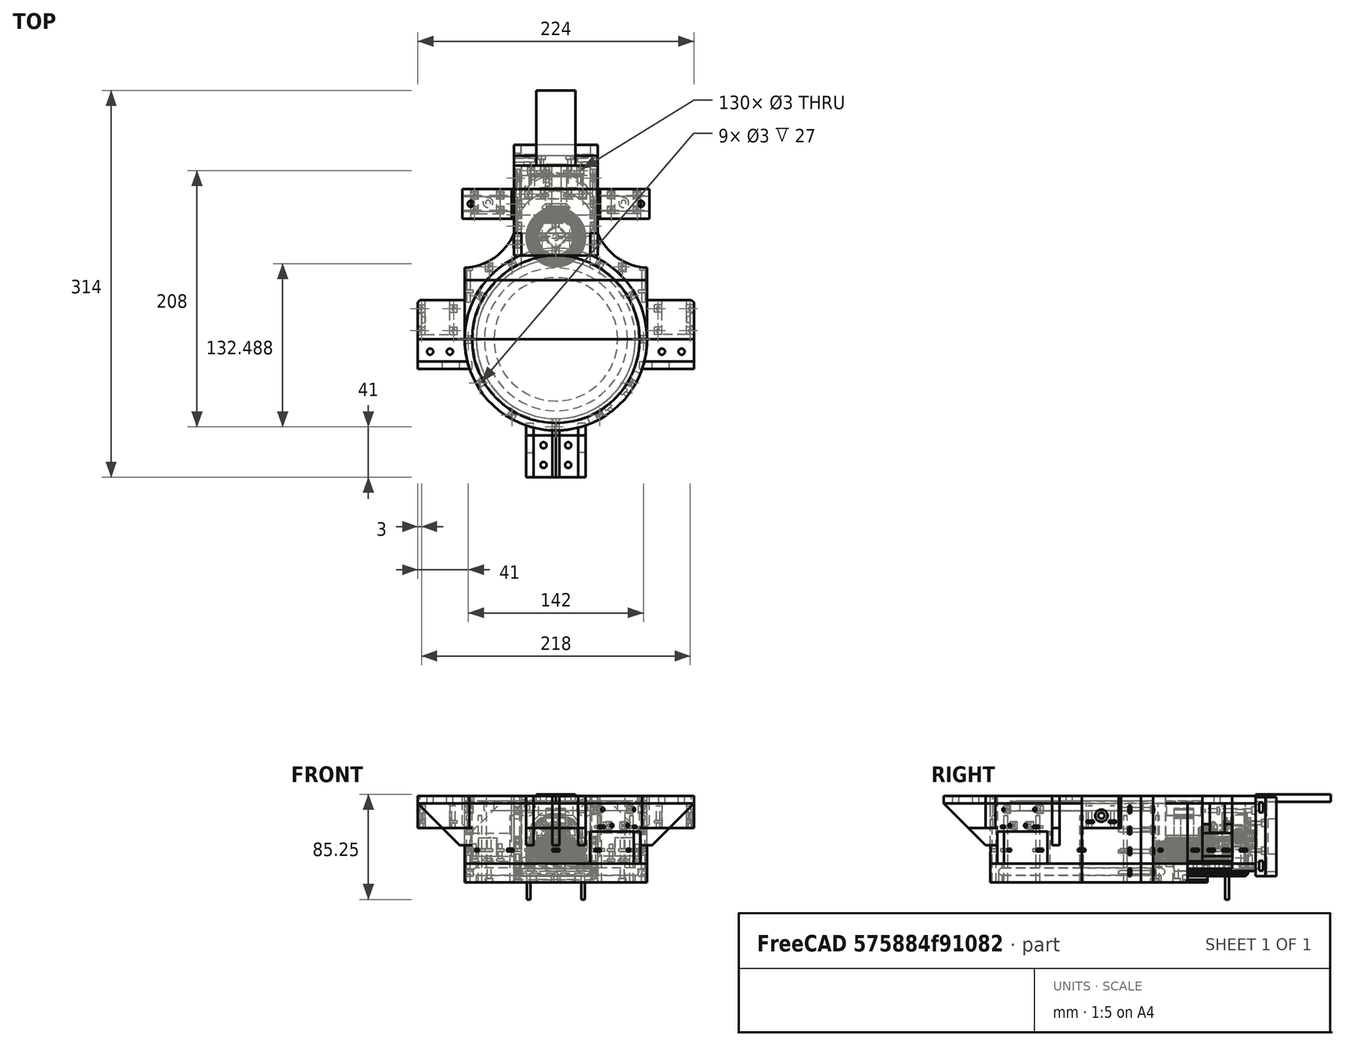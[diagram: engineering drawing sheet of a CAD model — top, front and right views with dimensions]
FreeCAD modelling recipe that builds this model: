
FCSTD DOCUMENT  (FreeCAD 0.19R24276 (Git))
Label: bazovina-part-I_rear-gearbox_027
License: All rights reserved
LicenseURL: http://en.wikipedia.org/wiki/All_rights_reserved
objects: Part::Cylinder×416, Part::Cut×219, Part::Box×206, Part::Compound×198, Part::FeaturePython×26, Part::Chamfer×25, Sketcher::SketchObject×8, PartDesign::Revolution×8, PartDesign::Body×8, Part::Common×6, Mesh::Feature×5, Part::Mirroring×4, Part::MultiFuse×3, Part::Torus×1
note: 1136 computed .brp shape members not serialized (recipe doc carries the construction recipe); baked Part::Feature solids carry a one-line shape summary decoded from their .brp

FEATURE [Part::Box] Box234  label="Krychle234"
  AttacherType = Attacher::AttachEngine3D
  Height = 2
  Length = 6
  Placement = pos=(-27,107,39) rot=(0,0,1;1.5708rad)
  Width = 8
FEATURE [Part::Box] Box235  label="Krychle235"
  AttacherType = Attacher::AttachEngine3D
  Height = 2
  Length = 6
  Placement = pos=(35,89,39) rot=(0,0,1;1.5708rad)
  Width = 8
FEATURE [Part::Box] Box236  label="Krychle236"
  AttacherType = Attacher::AttachEngine3D
  Height = 2
  Length = 6
  Placement = pos=(35,107,39) rot=(0,0,1;1.5708rad)
  Width = 8
FEATURE [Part::Box] Box233  label="Krychle233"
  AttacherType = Attacher::AttachEngine3D
  Height = 2
  Length = 6
  Placement = pos=(-27,89,39) rot=(0,0,1;1.5708rad)
  Width = 8
FEATURE [Part::Box] Box232  label="Krychle232"
  AttacherType = Attacher::AttachEngine3D
  Height = 6
  Length = 49
  Placement = pos=(28,86,78) rot=(0,1,0;1.5708rad)
  Width = 36
FEATURE [Part::Cylinder] Cylinder607  label="Válec607"
  Angle = 360
  AttacherType = Attacher::AttachEngine3D
  Height = 50
  Placement = pos=(-31,92,0) rot=(0,0,1;0.785398rad)
  Radius = 1.5
FEATURE [Part::Cylinder] Cylinder608  label="Válec608"
  Angle = 360
  AttacherType = Attacher::AttachEngine3D
  Height = 50
  Placement = pos=(-31,110,0) rot=(0,0,1;0.785398rad)
  Radius = 1.5
FEATURE [Part::Box] Box179  label="Krychle179"
  AttacherType = Attacher::AttachEngine3D
  Height = 55
  Length = 56
  Placement = pos=(-28,0,29) rot=(0,0,1;0rad)
  Width = 200
FEATURE [Part::Box] Box172  label="Krychle172"
  AttacherType = Attacher::AttachEngine3D
  Height = 55
  Length = 148
  Placement = pos=(-74,48,29) rot=(0,0,1;0rad)
  Width = 38
FEATURE [Part::Cylinder] Cylinder480  label="Válec480"
  Angle = 360
  AttacherType = Attacher::AttachEngine3D
  Height = 55
  Placement = pos=(-76.3,104,29) rot=(0,0,1;0rad)
  Radius = 46
FEATURE [Part::Cylinder] Cylinder481  label="Válec481"
  Angle = 360
  AttacherType = Attacher::AttachEngine3D
  Height = 55
  Placement = pos=(76.3,104,29) rot=(0,0,1;0rad)
  Radius = 46
FEATURE [Part::Cylinder] Cylinder487  label="Válec487"
  Angle = 360
  AttacherType = Attacher::AttachEngine3D
  Height = 55
  Placement = pos=(0,0,29) rot=(0,0,1;0rad)
  Radius = 74
FEATURE [Part::Cut] Cut179
  Base = -> Box172
  Tool = -> Cylinder480
FEATURE [Part::Cut] Cut180
  Base = -> Cut179
  Tool = -> Cylinder481
FEATURE [Part::Cut] Cut191
  Base = -> Cut180
  Tool = -> Box179
FEATURE [Part::Cut] Cut192
  Base = -> Cut191
  Tool = -> Cylinder487
FEATURE [Part::Box] Box240  label="Krychle240"
  AttacherType = Attacher::AttachEngine3D
  Height = 6
  Length = 8
  Placement = pos=(-19,116,46) rot=(0,0,1;0rad)
  Width = 2
FEATURE [Part::Cylinder] Cylinder543  label="Válec543"
  Angle = 360
  AttacherType = Attacher::AttachEngine3D
  Height = 50
  Placement = pos=(-71,80,39) rot=(1,0,0;1.5708rad)
  Radius = 1.5
FEATURE [Part::Cylinder] Cylinder544  label="Válec544"
  Angle = 360
  AttacherType = Attacher::AttachEngine3D
  Height = 50
  Placement = pos=(71,80,39) rot=(1,0,0;1.5708rad)
  Radius = 1.5
FEATURE [Part::Cylinder] Cylinder549  label="Válec549"
  Angle = 360
  AttacherType = Attacher::AttachEngine3D
  Height = 50
  Placement = pos=(71,106,73) rot=(1,0,0;1.5708rad)
  Radius = 3
FEATURE [Part::Cylinder] Cylinder547  label="Válec547"
  Angle = 360
  AttacherType = Attacher::AttachEngine3D
  Height = 50
  Placement = pos=(-71,106,39) rot=(1,0,0;1.5708rad)
  Radius = 3
FEATURE [Part::Cylinder] Cylinder548  label="Válec548"
  Angle = 360
  AttacherType = Attacher::AttachEngine3D
  Height = 50
  Placement = pos=(71,106,39) rot=(1,0,0;1.5708rad)
  Radius = 3
FEATURE [Part::Cylinder] Cylinder546  label="Válec546"
  Angle = 360
  AttacherType = Attacher::AttachEngine3D
  Height = 50
  Placement = pos=(71,80,73) rot=(1,0,0;1.5708rad)
  Radius = 1.5
FEATURE [Part::Cylinder] Cylinder545  label="Válec545"
  Angle = 360
  AttacherType = Attacher::AttachEngine3D
  Height = 50
  Placement = pos=(-71,80,73) rot=(1,0,0;1.5708rad)
  Radius = 1.5
FEATURE [Part::Cylinder] Cylinder550  label="Válec550"
  Angle = 360
  AttacherType = Attacher::AttachEngine3D
  Height = 50
  Placement = pos=(-71,106,73) rot=(1,0,0;1.5708rad)
  Radius = 3
FEATURE [Part::Box] Box241  label="Krychle241"
  AttacherType = Attacher::AttachEngine3D
  Height = 6
  Length = 8
  Placement = pos=(11,116,46) rot=(0,0,1;0rad)
  Width = 2
FEATURE [Part::Cylinder] Cylinder624  label="Válec624"
  Angle = 360
  AttacherType = Attacher::AttachEngine3D
  Height = 6
  Placement = pos=(0,83,68) rot=(0,0,1;0rad)
  Radius = 8
FEATURE [Part::Compound] Compound375
  Links = -> [Cylinder608,Cylinder607]
FEATURE [Part::Compound] Compound373
  Links = -> [Box235,Box236]
FEATURE [Part::Compound] Compound374
  Links = -> [Box233,Box234]
FEATURE [Part::Cylinder] Cylinder587  label="Válec587"
  Angle = 360
  AttacherType = Attacher::AttachEngine3D
  Height = 12
  Placement = pos=(0,83,68) rot=(0,0,1;0rad)
  Radius = 14
FEATURE [Part::Cut] Cut245
  Base = -> Cylinder587
  Tool = -> Cylinder624
FEATURE [Part::Cylinder] Cylinder615  label="Válec615"
  Angle = 360
  AttacherType = Attacher::AttachEngine3D
  Height = 40
  Placement = pos=(16,140,49) rot=(1,0,0;1.5708rad)
  Radius = 1.5
FEATURE [Part::Box] Box237  label="Krychle237"
  AttacherType = Attacher::AttachEngine3D
  Height = 49
  Length = 56
  Placement = pos=(-28,114,29) rot=(0,0,1;0rad)
  Width = 8
FEATURE [Part::Cylinder] Cylinder609  label="Válec609"
  Angle = 360
  AttacherType = Attacher::AttachEngine3D
  Height = 50
  Placement = pos=(31,110,0) rot=(0,0,1;0.785398rad)
  Radius = 1.5
FEATURE [Part::Cylinder] Cylinder610  label="Válec610"
  Angle = 360
  AttacherType = Attacher::AttachEngine3D
  Height = 50
  Placement = pos=(31,92,0) rot=(0,0,1;0.785398rad)
  Radius = 1.5
FEATURE [Part::Box] Box230  label="Krychle230"
  AttacherType = Attacher::AttachEngine3D
  Height = 6
  Length = 49
  Placement = pos=(-34,86,78) rot=(0,1,0;1.5708rad)
  Width = 36
FEATURE [Part::Cut] Cut238
  Base = -> Box230
  Tool = -> Compound374
FEATURE [Part::Cut] Cut239
  Base = -> Cut238
  Tool = -> Compound375
FEATURE [Part::Box] Box231  label="Krychle231"
  AttacherType = Attacher::AttachEngine3D
  Height = 6
  Length = 68
  Placement = pos=(-34,68,78) rot=(0,0,1;0rad)
  Width = 54
FEATURE [Part::Cylinder] Cylinder617  label="Válec617"
  Angle = 360
  AttacherType = Attacher::AttachEngine3D
  Height = 40
  Placement = pos=(-16,140,49) rot=(1,0,0;1.5708rad)
  Radius = 1.5
FEATURE [Part::Cylinder] Cylinder618  label="Válec618"
  Angle = 360
  AttacherType = Attacher::AttachEngine3D
  Height = 40
  Placement = pos=(0,140,33) rot=(1,0,0;1.5708rad)
  Radius = 1.5
FEATURE [Part::Cylinder] Cylinder619  label="Válec619"
  Angle = 360
  AttacherType = Attacher::AttachEngine3D
  Height = 20
  Placement = pos=(0,124,49) rot=(1,0,0;1.5708rad)
  Radius = 12
FEATURE [Part::Box] Box238  label="Krychle238"
  AttacherType = Attacher::AttachEngine3D
  Height = 8
  Length = 6
  Placement = pos=(-3,116,60) rot=(0,0,1;0rad)
  Width = 2
FEATURE [Part::Cylinder] Cylinder616  label="Válec616"
  Angle = 360
  AttacherType = Attacher::AttachEngine3D
  Height = 40
  Placement = pos=(0,140,65) rot=(1,0,0;1.5708rad)
  Radius = 1.5
FEATURE [Part::Box] Box239  label="Krychle239"
  AttacherType = Attacher::AttachEngine3D
  Height = 8
  Length = 6
  Placement = pos=(-3,116,30) rot=(0,0,1;0rad)
  Width = 2
FEATURE [Part::Compound] Compound378
  Links = -> [Box238,Box239,Box240,Box241]
  Placement = pos=(-34.6482,0,14.3518) rot=(0,1,0;0.785398rad)
FEATURE [Part::FeaturePython] Tube031  # WARN: FeaturePython — macro-defined, semantics opaque (R4)
  AttacherType = Attacher::AttachEngine3D
  Height = 1
  InnerRadius = 7
  OuterRadius = 8
  Placement = pos=(0,83,73) rot=(0,0,1;0rad)
FEATURE [Part::Compound] Compound383
  Links = -> [Cut245,Tube031]
FEATURE [Part::Compound] Compound377
  Links = -> [Cylinder616,Cylinder615,Cylinder617,Cylinder618]
  Placement = pos=(-34.6482,0,14.3518) rot=(0,1,0;0.785398rad)
FEATURE [Part::Cut] Cut242
  Base = -> Box237
  Tool = -> Compound377
FEATURE [Part::Cut] Cut243
  Base = -> Cut242
  Tool = -> Cylinder619
FEATURE [Part::Cut] Cut244
  Base = -> Cut243
  Tool = -> Compound378
FEATURE [Part::Compound] Compound372
  Links = -> [Cylinder609,Cylinder610]
FEATURE [Part::Cut] Cut240
  Base = -> Box232
  Tool = -> Compound372
FEATURE [Part::Cut] Cut241
  Base = -> Cut240
  Tool = -> Compound373
FEATURE [Part::Compound] Compound380
  Links = -> [Cut244,Cut239,Cut241]
FEATURE [Part::FeaturePython] Tube032  # WARN: FeaturePython — macro-defined, semantics opaque (R4)
  AttacherType = Attacher::AttachEngine3D
  Height = 1
  InnerRadius = 7
  OuterRadius = 8
  Placement = pos=(0,83,73) rot=(0,0,1;0rad)
FEATURE [Part::Torus] Torus004  label="Anuloid004"
  Angle1 = -180
  Angle2 = 180
  Angle3 = 360
  AttacherType = Attacher::AttachEngine3D
  Placement = pos=(0,0,24.5) rot=(0,0,1;0rad)
  Radius1 = 64.2
  Radius2 = 3.1
FEATURE [Part::FeaturePython] Tube026  # WARN: FeaturePython — macro-defined, semantics opaque (R4)
  AttacherType = Attacher::AttachEngine3D
  Height = 15
  InnerRadius = 64.5
  OuterRadius = 74
  Placement = pos=(0,0,16) rot=(0,0,1;0rad)
FEATURE [Part::Cylinder] Cylinder973  label="Válec973"
  Angle = 360
  AttacherType = Attacher::AttachEngine3D
  Height = 60
  Placement = pos=(0,-71,0) rot=(0,0,1;0rad)
  Radius = 1.5
FEATURE [Part::Cylinder] Cylinder974  label="Válec974"
  Angle = 360
  AttacherType = Attacher::AttachEngine3D
  Height = 60
  Placement = pos=(35.5,-61.4878,0) rot=(0,0,1;0.523599rad)
  Radius = 1.5
FEATURE [Part::Cylinder] Cylinder982  label="Válec982"
  Angle = 360
  AttacherType = Attacher::AttachEngine3D
  Height = 60
  Placement = pos=(-71,2.7e-14,0) rot=(0,0,-1;1.5708rad)
  Radius = 1.5
FEATURE [Part::Cylinder] Cylinder977  label="Válec977"
  Angle = 360
  AttacherType = Attacher::AttachEngine3D
  Height = 60
  Placement = pos=(61.4878,35.5,0) rot=(0,0,1;2.0944rad)
  Radius = 1.5
FEATURE [Part::Cylinder] Cylinder981  label="Válec981"
  Angle = 360
  AttacherType = Attacher::AttachEngine3D
  Height = 60
  Placement = pos=(-61.4878,35.5,0) rot=(0,0,1;4.18879rad)
  Radius = 1.5
FEATURE [Part::Cylinder] Cylinder551  label="Válec551"
  Angle = 360
  AttacherType = Attacher::AttachEngine3D
  Height = 50
  Placement = pos=(-71,80,24) rot=(1,0,0;1.5708rad)
  Radius = 1.5
FEATURE [Part::Cylinder] Cylinder983  label="Válec983"
  Angle = 360
  AttacherType = Attacher::AttachEngine3D
  Height = 15
  Placement = pos=(0,0,16) rot=(0,0,1;0rad)
  Radius = 74
FEATURE [Part::Box] Box176  label="Krychle176"
  AttacherType = Attacher::AttachEngine3D
  Height = 15
  Length = 148
  Placement = pos=(-74,0,16) rot=(0,0,1;0rad)
  Width = 48
FEATURE [Part::Cylinder] Cylinder984  label="Válec984"
  Angle = 360
  AttacherType = Attacher::AttachEngine3D
  Height = 20
  Placement = pos=(0,-63.8,4.5) rot=(0,0,1;0rad)
  Radius = 3.5
FEATURE [Part::Box] Box209  label="Krychle209"
  AttacherType = Attacher::AttachEngine3D
  Height = 6
  Length = 8
  Placement = pos=(-75,38,21) rot=(0,0,1;0rad)
  Width = 2
FEATURE [Part::Cylinder] Cylinder552  label="Válec552"
  Angle = 360
  AttacherType = Attacher::AttachEngine3D
  Height = 50
  Placement = pos=(71,80,24) rot=(1,0,0;1.5708rad)
  Radius = 1.5
FEATURE [Part::Compound] Compound339
  Links = -> [Cylinder552,Cylinder551]
FEATURE [Part::Box] Box208  label="Krychle208"
  AttacherType = Attacher::AttachEngine3D
  Height = 6
  Length = 8
  Placement = pos=(67,38,21) rot=(0,0,1;0rad)
  Width = 2
FEATURE [Part::Compound] Compound338
  Links = -> [Box208,Box209]
FEATURE [Part::Cylinder] Cylinder985  label="Válec985"
  Angle = 360
  AttacherType = Attacher::AttachEngine3D
  Height = 15
  Placement = pos=(0,0,16) rot=(0,0,1;0rad)
  Radius = 74
FEATURE [Part::Box] Box242  label="Krychle242"
  AttacherType = Attacher::AttachEngine3D
  Height = 47
  Length = 56
  Placement = pos=(-28,0,29) rot=(0,0,1;0rad)
  Width = 200
FEATURE [Part::Cylinder] Cylinder976  label="Válec976"
  Angle = 360
  AttacherType = Attacher::AttachEngine3D
  Height = 60
  Placement = pos=(71,-1.8e-14,0) rot=(0,0,1;1.5708rad)
  Radius = 1.5
FEATURE [Part::Cylinder] Cylinder975  label="Válec975"
  Angle = 360
  AttacherType = Attacher::AttachEngine3D
  Height = 60
  Placement = pos=(61.4878,-35.5,0) rot=(0,0,1;1.0472rad)
  Radius = 1.5
FEATURE [Part::Cylinder] Cylinder978  label="Válec978"
  Angle = 360
  AttacherType = Attacher::AttachEngine3D
  Height = 60
  Placement = pos=(35.5,61.4878,0) rot=(0,0,1;2.61799rad)
  Radius = 1.5
FEATURE [Part::Cylinder] Cylinder980  label="Válec980"
  Angle = 360
  AttacherType = Attacher::AttachEngine3D
  Height = 60
  Placement = pos=(-35.5,61.4878,0) rot=(0,0,1;3.66519rad)
  Radius = 1.5
FEATURE [Part::Cylinder] Cylinder986  label="Válec986"
  Angle = 360
  AttacherType = Attacher::AttachEngine3D
  Height = 60
  Placement = pos=(-35.5,-61.4878,0) rot=(0,0,-1;0.523599rad)
  Radius = 1.5
FEATURE [Part::Cylinder] Cylinder987  label="Válec987"
  Angle = 360
  AttacherType = Attacher::AttachEngine3D
  Height = 60
  Placement = pos=(-61.4878,-35.5,0) rot=(0,0,-1;1.0472rad)
  Radius = 1.5
FEATURE [Part::Compound] Compound525
  Links = -> [Cylinder973,Cylinder974,Cylinder975,Cylinder976,Cylinder977,Cylinder978,Cylinder980,Cylinder981,Cylinder982,Cylinder987,Cylinder986]
FEATURE [Part::Cut] Cut206
  Base = -> Tube026
  Tool = -> Torus004
FEATURE [Part::Cut] Cut202
  Base = -> Cut206
  Tool = -> Cylinder984
FEATURE [Part::Cut] Cut196
  Base = -> Box176
  Tool = -> Cylinder985
FEATURE [Part::Cut] Cut207
  Base = -> Cut196
  Tool = -> Cylinder983
FEATURE [Part::Compound] Compound340
  Links = -> [Cut207,Cut202]
FEATURE [Part::Cut] Cut201
  Base = -> Compound340
  Tool = -> Compound338
FEATURE [Part::Cut] Cut205
  Base = -> Cut201
  Tool = -> Compound339
FEATURE [Part::Cut] Cut203
  Base = -> Cut205
  Tool = -> Box242
FEATURE [Part::Cut] Cut204  label="bazovina_part-E_lozo-okruh-novo"
  Base = -> Cut203
  Placement = pos=(0,0,-2) rot=(0,0,1;0rad)
  Tool = -> Compound525
FEATURE [Part::Box] Box486  label="Krychle486"
  AttacherType = Attacher::AttachEngine3D
  Height = 55
  Length = 148
  Placement = pos=(-74,68,29) rot=(0,0,1;0rad)
  Width = 26
FEATURE [Part::Box] Box485  label="Krychle485"
  AttacherType = Attacher::AttachEngine3D
  Height = 49
  Length = 56
  Placement = pos=(-28,35,29) rot=(0,0,1;0rad)
  Width = 200
FEATURE [Part::FeaturePython] Tube035  # WARN: FeaturePython — macro-defined, semantics opaque (R4)
  AttacherType = Attacher::AttachEngine3D
  Height = 55
  InnerRadius = 68
  OuterRadius = 74
  Placement = pos=(0,0,29) rot=(0,0,1;0rad)
FEATURE [Part::FeaturePython] Tube036  # WARN: FeaturePython — macro-defined, semantics opaque (R4)
  AttacherType = Attacher::AttachEngine3D
  Height = 8
  InnerRadius = 50.1
  OuterRadius = 58
  Placement = pos=(0,0,72) rot=(0,0,1;0rad)
FEATURE [Part::Cut] Cut455
  Base = -> Tube035
  Tool = -> Box485
FEATURE [Part::Cut] Cut454
  Base = -> Cut455
  Tool = -> Box486
FEATURE [Part::Box] Box483  label="Krychle483"
  AttacherType = Attacher::AttachEngine3D
  Height = 34
  Length = 148
  Placement = pos=(-74,68,38) rot=(0,0,1;0rad)
  Width = 20
FEATURE [Part::Box] Box647  label="Krychle647"
  AttacherType = Attacher::AttachEngine3D
  Height = 60
  Length = 200
  Placement = pos=(70.7107,70.7107,-5) rot=(0,0,1;3.92699rad)
  Width = 120
FEATURE [Part::Cylinder] Cylinder971  label="Válec971"
  Angle = 360
  AttacherType = Attacher::AttachEngine3D
  Height = 6
  Placement = pos=(0,0,65) rot=(0,0,1;0rad)
  Radius = 74
FEATURE [Part::Cut] Cut453
  Base = -> Cylinder971
  Placement = pos=(0,0,13) rot=(0,0,1;0rad)
  Tool = -> Box483
FEATURE [Part::Box] Box648  label="Krychle648"
  AttacherType = Attacher::AttachEngine3D
  Height = 60
  Length = 200
  Placement = pos=(0,0,-5) rot=(0,0,-1;0.383972rad)
  Width = 200
FEATURE [Part::Cut] Cut464
  Base = -> Box647
  Tool = -> Box648
FEATURE [Part::Box] Box649  label="Krychle649"
  AttacherType = Attacher::AttachEngine3D
  Height = 60
  Length = 200
  Placement = pos=(0,0,-5) rot=(0,0,1;3.52556rad)
  Width = 200
FEATURE [Part::Cut] Cut465
  Base = -> Cut464
  Tool = -> Box649
FEATURE [Part::Cut] Cut
  Base = -> Cut454
  Tool = -> Cut465
FEATURE [Part::Box] Box491  label="Krychle491"
  AttacherType = Attacher::AttachEngine3D
  Height = 2
  Length = 6
  Placement = pos=(75,-3,39) rot=(0,0,1;1.5708rad)
  Width = 8
FEATURE [Part::Box] Box493  label="Krychle493"
  AttacherType = Attacher::AttachEngine3D
  Height = 2
  Length = 6
  Placement = pos=(40.0981,63.4519,39) rot=(0,0,1;2.61799rad)
  Width = 8
FEATURE [Part::Box] Box489  label="Krychle489"
  AttacherType = Attacher::AttachEngine3D
  Height = 2
  Length = 6
  Placement = pos=(34.9,-66.45,58) rot=(0,0,1;0.523599rad)
  Width = 8
FEATURE [Part::Box] Box488  label="Krychle488"
  AttacherType = Attacher::AttachEngine3D
  Height = 2
  Length = 6
  Placement = pos=(-3,-75,39) rot=(0,0,1;0rad)
  Width = 8
FEATURE [Part::Box] Box495  label="Krychle495"
  AttacherType = Attacher::AttachEngine3D
  Height = 2
  Length = 6
  Placement = pos=(-34.9019,66.4519,39) rot=(0,0,1;3.66519rad)
  Width = 8
FEATURE [Part::Box] Box497  label="Krychle497"
  AttacherType = Attacher::AttachEngine3D
  Height = 2
  Length = 6
  Placement = pos=(-75,3,39) rot=(0,0,-1;1.5708rad)
  Width = 8
FEATURE [Part::Box] Box490  label="Krychle490"
  AttacherType = Attacher::AttachEngine3D
  Height = 2
  Length = 6
  Placement = pos=(63.45,-40.1,58) rot=(0,0,1;1.0472rad)
  Width = 8
FEATURE [Part::Box] Box498  label="Krychle498"
  AttacherType = Attacher::AttachEngine3D
  Height = 2
  Length = 6
  Placement = pos=(-66.4519,-34.9019,39) rot=(0,0,-1;1.0472rad)
  Width = 8
FEATURE [Part::Box] Box499  label="Krychle499"
  AttacherType = Attacher::AttachEngine3D
  Height = 2
  Length = 6
  Placement = pos=(-40.0981,-63.4519,39) rot=(0,0,-1;0.523599rad)
  Width = 8
FEATURE [Part::Cylinder] Cylinder1629  label="Válec1629"
  Angle = 360
  AttacherType = Attacher::AttachEngine3D
  Height = 72
  Placement = pos=(71,-1.8e-14,0) rot=(0,0,1;1.5708rad)
  Radius = 1.5
FEATURE [Part::Cylinder] Cylinder1630  label="Válec1630"
  Angle = 360
  AttacherType = Attacher::AttachEngine3D
  Height = 72
  Placement = pos=(35.5,61.4878,0) rot=(0,0,1;2.61799rad)
  Radius = 1.5
FEATURE [Part::Box] Box496  label="Krychle496"
  AttacherType = Attacher::AttachEngine3D
  Height = 2
  Length = 6
  Placement = pos=(-63.4519,40.0981,39) rot=(0,0,1;4.18879rad)
  Width = 8
FEATURE [Part::Cylinder] Cylinder1631  label="Válec1631"
  Angle = 360
  AttacherType = Attacher::AttachEngine3D
  Height = 72
  Placement = pos=(61.4878,-35.5,0) rot=(0,0,1;1.0472rad)
  Radius = 1.5
FEATURE [Part::Box] Box492  label="Krychle492"
  AttacherType = Attacher::AttachEngine3D
  Height = 2
  Length = 6
  Placement = pos=(66.4519,34.9019,39) rot=(0,0,1;2.0944rad)
  Width = 8
FEATURE [Part::Box] Box494  label="Krychle494"
  AttacherType = Attacher::AttachEngine3D
  Height = 2
  Length = 6
  Placement = pos=(3,75,39) rot=(0,0,1;3.14159rad)
  Width = 8
FEATURE [Part::Compound] Compound528
  Links = -> [Box488,Box489,Box490,Box491,Box492,Box493,Box494,Box495,Box496,Box497,Box498,Box499]
FEATURE [Part::Cut] Cut467
  Base = -> Cut
  Tool = -> Compound528
FEATURE [Part::Cylinder] Cylinder1635  label="Válec1635"
  Angle = 360
  AttacherType = Attacher::AttachEngine3D
  Height = 72
  Placement = pos=(-61.4878,-35.5,0) rot=(0,0,-1;1.0472rad)
  Radius = 1.5
FEATURE [Part::Cylinder] Cylinder1637  label="Válec1637"
  Angle = 360
  AttacherType = Attacher::AttachEngine3D
  Height = 72
  Placement = pos=(0,-71,0) rot=(0,0,1;0rad)
  Radius = 1.5
FEATURE [Part::Cylinder] Cylinder1638  label="Válec1638"
  Angle = 360
  AttacherType = Attacher::AttachEngine3D
  Height = 72
  Placement = pos=(-35.5,61.4878,0) rot=(0,0,1;3.66519rad)
  Radius = 1.5
FEATURE [Part::Cylinder] Cylinder1633  label="Válec1633"
  Angle = 360
  AttacherType = Attacher::AttachEngine3D
  Height = 72
  Placement = pos=(-35.5,-61.4878,0) rot=(0,0,-1;0.523599rad)
  Radius = 1.5
FEATURE [Part::Cylinder] Cylinder1634  label="Válec1634"
  Angle = 360
  AttacherType = Attacher::AttachEngine3D
  Height = 72
  Placement = pos=(-71,2.7e-14,0) rot=(0,0,-1;1.5708rad)
  Radius = 1.5
FEATURE [Part::Cylinder] Cylinder1639  label="Válec1639"
  Angle = 360
  AttacherType = Attacher::AttachEngine3D
  Height = 72
  Placement = pos=(-61.4878,35.5,0) rot=(0,0,1;4.18879rad)
  Radius = 1.5
FEATURE [Part::Cylinder] Cylinder1632  label="Válec1632"
  Angle = 360
  AttacherType = Attacher::AttachEngine3D
  Height = 72
  Placement = pos=(35.5,-61.4878,0) rot=(0,0,1;0.523599rad)
  Radius = 1.5
FEATURE [Part::Cylinder] Cylinder1636  label="Válec1636"
  Angle = 360
  AttacherType = Attacher::AttachEngine3D
  Height = 72
  Placement = pos=(61.4878,35.5,0) rot=(0,0,1;2.0944rad)
  Radius = 1.5
FEATURE [Part::Cylinder] Cylinder1640  label="Válec1640"
  Angle = 360
  AttacherType = Attacher::AttachEngine3D
  Height = 72
  Placement = pos=(3.1e-14,71,0) rot=(0,0,1;3.14159rad)
  Radius = 1.5
FEATURE [Part::Compound] Compound529
  Links = -> [Cylinder1637,Cylinder1632,Cylinder1631,Cylinder1629,Cylinder1636,Cylinder1630,Cylinder1640,Cylinder1638,Cylinder1639,Cylinder1634,Cylinder1635,Cylinder1633]
  Placement = pos=(0,0,-4) rot=(0,0,1;0rad)
FEATURE [Part::Cut] Cut468
  Base = -> Cut467
  Tool = -> Compound529
FEATURE [Part::Box] Box687  label="Krychle687"
  AttacherType = Attacher::AttachEngine3D
  Height = 6
  Length = 6
  Placement = pos=(-21,64,-50) rot=(0,0,1;0rad)
  Width = 4
FEATURE [Part::Cylinder] Cylinder1722  label="Válec1722"
  Angle = 360
  AttacherType = Attacher::AttachEngine3D
  Height = 50
  Placement = pos=(-18,100,72) rot=(1,0,0;1.5708rad)
  Radius = 1.5
FEATURE [Part::Compound] Compound863
  Links = -> [Cylinder1722]
  Placement = pos=(0,0,0) rot=(0,0,1;3.92699rad)
FEATURE [Part::Box] Box686  label="Krychle686"
  AttacherType = Attacher::AttachEngine3D
  Height = 6
  Length = 6
  Placement = pos=(15,64,-50) rot=(0,0,1;0rad)
  Width = 4
FEATURE [Part::Compound] Compound866
  Links = -> [Box687,Box686]
  Placement = pos=(0,0,120) rot=(0,0,1;3.92699rad)
FEATURE [Part::Cylinder] Cylinder1723  label="Válec1723"
  Angle = 360
  AttacherType = Attacher::AttachEngine3D
  Height = 50
  Placement = pos=(18,100,72) rot=(1,0,0;1.5708rad)
  Radius = 1.5
FEATURE [Part::Compound] Compound864
  Links = -> [Cylinder1723]
  Placement = pos=(0,0,0) rot=(0,0,1;3.92699rad)
FEATURE [Part::Compound] Compound865
  Links = -> [Compound863,Compound864]
  Placement = pos=(0,0,1) rot=(0,0,1;0rad)
FEATURE [Part::Cut] Cut500
  Base = -> Cut468
  Tool = -> Compound865
FEATURE [Part::Cut] Cut501
  Base = -> Cut500
  Tool = -> Compound866
FEATURE [Part::Cylinder] Cylinder1738  label="Válec1738"
  Angle = 360
  AttacherType = Attacher::AttachEngine3D
  Height = 50
  Placement = pos=(9,100,59) rot=(1,0,0;1.5708rad)
  Radius = 1.5
FEATURE [Part::Compound] Compound878
  Links = -> [Cylinder1738]
  Placement = pos=(0,0,0) rot=(0,0,1;3.92699rad)
FEATURE [Part::Box] Box692  label="Krychle692"
  AttacherType = Attacher::AttachEngine3D
  Height = 6
  Length = 6
  Placement = pos=(-12,66,-63) rot=(0,0,1;0rad)
  Width = 4
FEATURE [Part::Box] Box691  label="Krychle691"
  AttacherType = Attacher::AttachEngine3D
  Height = 6
  Length = 6
  Placement = pos=(6,66,-63) rot=(0,0,1;0rad)
  Width = 4
FEATURE [Part::Cylinder] Cylinder1737  label="Válec1737"
  Angle = 360
  AttacherType = Attacher::AttachEngine3D
  Height = 50
  Placement = pos=(-9,100,59) rot=(1,0,0;1.5708rad)
  Radius = 1.5
FEATURE [Part::Compound] Compound879
  Links = -> [Cylinder1737]
  Placement = pos=(0,0,0) rot=(0,0,1;3.92699rad)
FEATURE [Part::Compound] Compound877
  Links = -> [Compound879,Compound878]
  Placement = pos=(0,0,1) rot=(0,0,1;0rad)
FEATURE [Part::Cut] Cut508
  Base = -> Cut501
  Tool = -> Compound877
FEATURE [Part::Compound] Compound880
  Links = -> [Box692,Box691]
  Placement = pos=(0,0,120) rot=(0,0,1;3.92699rad)
FEATURE [Part::Cut] Cut509
  Base = -> Cut508
  Tool = -> Compound880
FEATURE [Part::Box] Box482  label="Krychle482"
  AttacherType = Attacher::AttachEngine3D
  Height = 55
  Length = 148
  Placement = pos=(-74,0,29) rot=(0,0,1;0rad)
  Width = 74
FEATURE [Part::Cylinder] Cylinder1758  label="Válec1758"
  Angle = 360
  AttacherType = Attacher::AttachEngine3D
  Height = 50
  Placement = pos=(71,80,56) rot=(1,0,0;1.5708rad)
  Radius = 1.5
FEATURE [Part::Cylinder] Cylinder1757  label="Válec1757"
  Angle = 360
  AttacherType = Attacher::AttachEngine3D
  Height = 50
  Placement = pos=(-71,80,56) rot=(1,0,0;1.5708rad)
  Radius = 1.5
FEATURE [Part::Box] Box512  label="Krychle512"
  AttacherType = Attacher::AttachEngine3D
  Height = 6
  Length = 8
  Placement = pos=(-75,38,36) rot=(0,0,1;0rad)
  Width = 2
FEATURE [Part::Box] Box700  label="Krychle700"
  AttacherType = Attacher::AttachEngine3D
  Height = 2
  Length = 6
  Placement = pos=(34.9019,-66.4519,39) rot=(0,0,1;0.523599rad)
  Width = 8
FEATURE [Part::Box] Box702  label="Krychle702"
  AttacherType = Attacher::AttachEngine3D
  Height = 2
  Length = 6
  Placement = pos=(75,-3,39) rot=(0,0,1;1.5708rad)
  Width = 8
FEATURE [Part::Box] Box704  label="Krychle704"
  AttacherType = Attacher::AttachEngine3D
  Height = 2
  Length = 6
  Placement = pos=(40.0981,63.4519,39) rot=(0,0,1;2.61799rad)
  Width = 8
FEATURE [Part::Box] Box484  label="Krychle484"
  AttacherType = Attacher::AttachEngine3D
  Height = 55
  Length = 148
  Placement = pos=(-74,48,29) rot=(0,0,1;0rad)
  Width = 26
FEATURE [Part::Cylinder] Cylinder1755  label="Válec1755"
  Angle = 360
  AttacherType = Attacher::AttachEngine3D
  Height = 50
  Placement = pos=(-71,80,39) rot=(1,0,0;1.5708rad)
  Radius = 1.5
FEATURE [Part::Cylinder] Cylinder1754  label="Válec1754"
  Angle = 360
  AttacherType = Attacher::AttachEngine3D
  Height = 50
  Placement = pos=(71,80,39) rot=(1,0,0;1.5708rad)
  Radius = 1.5
FEATURE [Part::Cylinder] Cylinder1756  label="Válec1756"
  Angle = 360
  AttacherType = Attacher::AttachEngine3D
  Height = 50
  Placement = pos=(71,80,73) rot=(1,0,0;1.5708rad)
  Radius = 1.5
FEATURE [Part::Cylinder] Cylinder1753  label="Válec1753"
  Angle = 360
  AttacherType = Attacher::AttachEngine3D
  Height = 50
  Placement = pos=(-71,80,73) rot=(1,0,0;1.5708rad)
  Radius = 1.5
FEATURE [Part::Compound] Compound887
  Links = -> [Cylinder1753,Cylinder1754,Cylinder1755,Cylinder1756,Cylinder1757,Cylinder1758]
FEATURE [Part::Cylinder] Cylinder972  label="Válec972"
  Angle = 360
  AttacherType = Attacher::AttachEngine3D
  Height = 51
  Placement = pos=(0,0,29) rot=(0,0,1;0rad)
  Radius = 74
FEATURE [Part::Cut] Cut451
  Base = -> Box482
  Tool = -> Cylinder972
FEATURE [Part::Cut] Cut452
  Base = -> Cut451
  Tool = -> Box484
FEATURE [Part::Cut] Cut518
  Base = -> Cut452
  Tool = -> Compound887
FEATURE [Part::Box] Box514  label="Krychle514"
  AttacherType = Attacher::AttachEngine3D
  Height = 6
  Length = 8
  Placement = pos=(67,38,70) rot=(0,0,1;0rad)
  Width = 2
FEATURE [Part::Box] Box513  label="Krychle513"
  AttacherType = Attacher::AttachEngine3D
  Height = 6
  Length = 8
  Placement = pos=(67,38,36) rot=(0,0,1;0rad)
  Width = 2
FEATURE [Part::Box] Box515  label="Krychle515"
  AttacherType = Attacher::AttachEngine3D
  Height = 6
  Length = 8
  Placement = pos=(-75,38,70) rot=(0,0,1;0rad)
  Width = 2
FEATURE [Part::Box] Box516  label="Krychle516"
  AttacherType = Attacher::AttachEngine3D
  Height = 6
  Length = 8
  Placement = pos=(-75,38,53) rot=(0,0,1;0rad)
  Width = 2
FEATURE [Part::Box] Box517  label="Krychle517"
  AttacherType = Attacher::AttachEngine3D
  Height = 6
  Length = 8
  Placement = pos=(67,38,53) rot=(0,0,1;0rad)
  Width = 2
FEATURE [Part::Box] Box699  label="Krychle699"
  AttacherType = Attacher::AttachEngine3D
  Height = 2
  Length = 6
  Placement = pos=(-3,-75,39) rot=(0,0,1;0rad)
  Width = 8
FEATURE [Part::Box] Box701  label="Krychle701"
  AttacherType = Attacher::AttachEngine3D
  Height = 2
  Length = 6
  Placement = pos=(63.4519,-40.0981,39) rot=(0,0,1;1.0472rad)
  Width = 8
FEATURE [Part::Box] Box703  label="Krychle703"
  AttacherType = Attacher::AttachEngine3D
  Height = 2
  Length = 6
  Placement = pos=(66.4519,34.9019,39) rot=(0,0,1;2.0944rad)
  Width = 8
FEATURE [Part::Box] Box425  label="Krychle425"
  AttacherType = Attacher::AttachEngine3D
  Height = 2
  Length = 6
  Placement = pos=(-112,4,60) rot=(0,0,1;0rad)
  Width = 6
FEATURE [Part::Box] Box426  label="Krychle426"
  AttacherType = Attacher::AttachEngine3D
  Height = 20
  Length = 20
  Placement = pos=(-106,4,56) rot=(0,0,1;0rad)
  Width = 80
FEATURE [Part::Box] Box706  label="Krychle706"
  AttacherType = Attacher::AttachEngine3D
  Height = 2
  Length = 6
  Placement = pos=(-34.9019,66.4519,39) rot=(0,0,1;3.66519rad)
  Width = 8
FEATURE [Part::Box] Box707  label="Krychle707"
  AttacherType = Attacher::AttachEngine3D
  Height = 2
  Length = 6
  Placement = pos=(-63.4519,40.0981,39) rot=(0,0,1;4.18879rad)
  Width = 8
FEATURE [Part::Box] Box708  label="Krychle708"
  AttacherType = Attacher::AttachEngine3D
  Height = 2
  Length = 6
  Placement = pos=(-75,3,39) rot=(0,0,-1;1.5708rad)
  Width = 8
FEATURE [Part::Box] Box709  label="Krychle709"
  AttacherType = Attacher::AttachEngine3D
  Height = 2
  Length = 6
  Placement = pos=(-66.4519,-34.9019,39) rot=(0,0,-1;1.0472rad)
  Width = 8
FEATURE [Part::Box] Box710  label="Krychle710"
  AttacherType = Attacher::AttachEngine3D
  Height = 2
  Length = 6
  Placement = pos=(-40.0981,-63.4519,39) rot=(0,0,-1;0.523599rad)
  Width = 8
FEATURE [Part::Box] Box705  label="Krychle705"
  AttacherType = Attacher::AttachEngine3D
  Height = 2
  Length = 6
  Placement = pos=(3,75,39) rot=(0,0,1;3.14159rad)
  Width = 8
FEATURE [Part::Compound] Compound530
  Links = -> [Box512,Box513,Box514,Box515,Box516,Box517]
FEATURE [Part::Compound] Compound888
  Links = -> [Box699,Box700,Box701,Box702,Box703,Box704,Box705,Box706,Box707,Box708,Box709,Box710]
FEATURE [Part::Cut] Cut519
  Base = -> Cut518
  Tool = -> Compound530
FEATURE [Part::Cut] Cut520
  Base = -> Cut519
  Tool = -> Compound888
FEATURE [Part::Box] Box427  label="Krychle427"
  AttacherType = Attacher::AttachEngine3D
  Height = 2
  Length = 6
  Placement = pos=(-112,22,60) rot=(0,0,1;0rad)
  Width = 6
FEATURE [Part::Box] Box431  label="Krychle431"
  AttacherType = Attacher::AttachEngine3D
  Height = 6
  Length = 51
  Placement = pos=(-112,-24,76) rot=(0,0,1;0rad)
  Width = 24
FEATURE [Part::Box] Box521  label="Krychle521"
  AttacherType = Attacher::AttachEngine3D
  Height = 14
  Length = 24
  Placement = pos=(-92,-24,44) rot=(0,0,1;0rad)
  Width = 6
FEATURE [Part::Chamfer] Chamfer016
  Base = -> Box521
  Edges = 1 edges r=13.99: [Edge4]
FEATURE [Part::Box] Box417  label="Krychle417"
  AttacherType = Attacher::AttachEngine3D
  Height = 20
  Length = 20
  Placement = pos=(-106,4,56) rot=(0,0,1;0rad)
  Width = 80
FEATURE [Part::Cylinder] Cylinder899  label="Válec899"
  Angle = 360
  AttacherType = Attacher::AttachEngine3D
  Height = 20
  Placement = pos=(-83,25,54) rot=(0,0,1;0rad)
  Radius = 1.5
FEATURE [Part::Cylinder] Cylinder900  label="Válec900"
  Angle = 360
  AttacherType = Attacher::AttachEngine3D
  Height = 20
  Placement = pos=(-83,7,54) rot=(0,0,1;0rad)
  Radius = 1.5
FEATURE [Part::Box] Box429  label="Krychle429"
  AttacherType = Attacher::AttachEngine3D
  Height = 2
  Length = 6
  Placement = pos=(-86,4,60) rot=(0,0,1;0rad)
  Width = 6
FEATURE [Part::Cylinder] Cylinder901  label="Válec901"
  Angle = 360
  AttacherType = Attacher::AttachEngine3D
  Height = 20
  Placement = pos=(-109,7,54) rot=(0,0,1;0rad)
  Radius = 1.5
FEATURE [Part::Cylinder] Cylinder903  label="Válec903"
  Angle = 360
  AttacherType = Attacher::AttachEngine3D
  Height = 3
  Placement = pos=(-112,16,66) rot=(0,1,0;1.5708rad)
  Radius = 5
FEATURE [Part::Box] Box430  label="Krychle430"
  AttacherType = Attacher::AttachEngine3D
  Height = 26
  Length = 38
  Placement = pos=(-112,0,56) rot=(0,0,1;0rad)
  Width = 32
FEATURE [Part::Cut] Cut409
  Base = -> Box430
  Tool = -> Box426
FEATURE [Part::Cylinder] Cylinder904  label="Válec904"
  Angle = 360
  AttacherType = Attacher::AttachEngine3D
  Height = 20
  Placement = pos=(-117,16,66) rot=(0,1,0;1.5708rad)
  Radius = 2.5
FEATURE [Part::Cylinder] Cylinder905  label="Válec905"
  Angle = 360
  AttacherType = Attacher::AttachEngine3D
  Height = 10
  Placement = pos=(0,0,72) rot=(0,0,1;0rad)
  Radius = 74
FEATURE [Part::Cut] Cut408
  Base = -> Box431
  Tool = -> Cylinder905
FEATURE [Part::Cylinder] Cylinder906  label="Válec906"
  Angle = 360
  AttacherType = Attacher::AttachEngine3D
  Height = 32
  Placement = pos=(0,0,50) rot=(0,0,1;0rad)
  Radius = 74
FEATURE [Part::Box] Box432  label="Krychle432"
  AttacherType = Attacher::AttachEngine3D
  Height = 26
  Length = 50
  Placement = pos=(-112,-24,56) rot=(0,0,1;0rad)
  Width = 6
FEATURE [Part::Cut] Cut406
  Base = -> Box432
  Tool = -> Cylinder906
FEATURE [Part::Chamfer] Chamfer003
  Base = -> Cut406
  Edges = 1 edges r=20: [Edge4]
FEATURE [Part::Cylinder] Cylinder908  label="Válec908"
  Angle = 360
  AttacherType = Attacher::AttachEngine3D
  Height = 20
  Placement = pos=(-102,-10,66) rot=(0,0,1;0rad)
  Radius = 2.5
FEATURE [Part::Cylinder] Cylinder902  label="Válec902"
  Angle = 360
  AttacherType = Attacher::AttachEngine3D
  Height = 20
  Placement = pos=(-109,25,54) rot=(0,0,1;0rad)
  Radius = 1.5
FEATURE [Part::Compound] Compound496
  Links = -> [Cylinder900,Cylinder899,Cylinder901,Cylinder902]
FEATURE [Part::Box] Box428  label="Krychle428"
  AttacherType = Attacher::AttachEngine3D
  Height = 2
  Length = 6
  Placement = pos=(-86,22,60) rot=(0,0,1;0rad)
  Width = 6
FEATURE [Part::Compound] Compound495
  Links = -> [Box425,Box427,Box429,Box428]
FEATURE [Part::Cut] Cut410
  Base = -> Cut409
  Tool = -> Compound495
FEATURE [Part::Cut] Cut403
  Base = -> Cut410
  Tool = -> Compound496
FEATURE [Part::Cut] Cut404
  Base = -> Cut403
  Tool = -> Cylinder904
FEATURE [Part::Cut] Cut405
  Base = -> Cut404
  Tool = -> Cylinder903
FEATURE [Part::Chamfer] Chamfer004
  Base = -> Cut405
  Edges = 1 edges r=2: [Edge4]
FEATURE [Part::Cylinder] Cylinder907  label="Válec907"
  Angle = 360
  AttacherType = Attacher::AttachEngine3D
  Height = 20
  Placement = pos=(-86,-10,66) rot=(0,0,1;0rad)
  Radius = 2.5
FEATURE [Part::Compound] Compound498
  Links = -> [Cylinder908,Cylinder907]
FEATURE [Part::Cut] Cut407
  Base = -> Cut408
  Tool = -> Compound498
FEATURE [Part::Compound] Compound497  label="stabilo_holdo_left"
  Links = -> [Chamfer003,Cut407,Chamfer004]
  Placement = pos=(0,0,2) rot=(0,0,1;0rad)
FEATURE [Part::Compound] Compound531  label="stabilo_holdo_left_silo"
  Links = -> [Compound497,Chamfer016]
FEATURE [Part::Box] Box416  label="Krychle416"
  AttacherType = Attacher::AttachEngine3D
  Height = 26
  Length = 38
  Placement = pos=(-112,0,56) rot=(0,0,1;0rad)
  Width = 32
FEATURE [Part::Box] Box421  label="Krychle421"
  AttacherType = Attacher::AttachEngine3D
  Height = 2
  Length = 6
  Placement = pos=(-86,22,60) rot=(0,0,1;0rad)
  Width = 6
FEATURE [Part::Box] Box420  label="Krychle420"
  AttacherType = Attacher::AttachEngine3D
  Height = 2
  Length = 6
  Placement = pos=(-86,4,60) rot=(0,0,1;0rad)
  Width = 6
FEATURE [Part::Cylinder] Cylinder1759  label="Válec1759"
  Angle = 360
  AttacherType = Attacher::AttachEngine3D
  Height = 20
  Placement = pos=(-83,7,54) rot=(0,0,1;0rad)
  Radius = 1.5
FEATURE [Part::Cylinder] Cylinder876  label="Válec876"
  Angle = 360
  AttacherType = Attacher::AttachEngine3D
  Height = 20
  Placement = pos=(-109,7,54) rot=(0,0,1;0rad)
  Radius = 1.5
FEATURE [Part::Cylinder] Cylinder877  label="Válec877"
  Angle = 360
  AttacherType = Attacher::AttachEngine3D
  Height = 20
  Placement = pos=(-109,25,54) rot=(0,0,1;0rad)
  Radius = 1.5
FEATURE [Part::Box] Box423  label="Krychle423"
  AttacherType = Attacher::AttachEngine3D
  Height = 6
  Length = 51
  Placement = pos=(-112,-24,76) rot=(0,0,1;0rad)
  Width = 24
FEATURE [Part::Cylinder] Cylinder875  label="Válec875"
  Angle = 360
  AttacherType = Attacher::AttachEngine3D
  Height = 20
  Placement = pos=(-83,25,54) rot=(0,0,1;0rad)
  Radius = 1.5
FEATURE [Part::Cylinder] Cylinder893  label="Válec893"
  Angle = 360
  AttacherType = Attacher::AttachEngine3D
  Height = 3
  Placement = pos=(-112,16,66) rot=(0,1,0;1.5708rad)
  Radius = 5
FEATURE [Part::Box] Box418  label="Krychle418"
  AttacherType = Attacher::AttachEngine3D
  Height = 2
  Length = 6
  Placement = pos=(-112,4,60) rot=(0,0,1;0rad)
  Width = 6
FEATURE [Part::Box] Box424  label="Krychle424"
  AttacherType = Attacher::AttachEngine3D
  Height = 26
  Length = 50
  Placement = pos=(-112,-24,56) rot=(0,0,1;0rad)
  Width = 6
FEATURE [Part::Cylinder] Cylinder892  label="Válec892"
  Angle = 360
  AttacherType = Attacher::AttachEngine3D
  Height = 20
  Placement = pos=(-117,16,66) rot=(0,1,0;1.5708rad)
  Radius = 2.5
FEATURE [Part::Cylinder] Cylinder894  label="Válec894"
  Angle = 360
  AttacherType = Attacher::AttachEngine3D
  Height = 10
  Placement = pos=(0,0,72) rot=(0,0,1;0rad)
  Radius = 74
FEATURE [Part::Cylinder] Cylinder895  label="Válec895"
  Angle = 360
  AttacherType = Attacher::AttachEngine3D
  Height = 20
  Placement = pos=(-102,-10,66) rot=(0,0,1;0rad)
  Radius = 2.5
FEATURE [Part::Box] Box419  label="Krychle419"
  AttacherType = Attacher::AttachEngine3D
  Height = 2
  Length = 6
  Placement = pos=(-112,22,60) rot=(0,0,1;0rad)
  Width = 6
FEATURE [Part::Compound] Compound488
  Links = -> [Box418,Box419,Box420,Box421]
FEATURE [Part::Compound] Compound489
  Links = -> [Cylinder1759,Cylinder875,Cylinder876,Cylinder877]
FEATURE [Part::Cut] Cut400
  Base = -> Box423
  Tool = -> Cylinder894
FEATURE [Part::Cut] Cut521
  Base = -> Box416
  Tool = -> Box417
FEATURE [Part::Cut] Cut392
  Base = -> Cut521
  Tool = -> Compound488
FEATURE [Part::Cut] Cut393
  Base = -> Cut392
  Tool = -> Compound489
FEATURE [Part::Cut] Cut398
  Base = -> Cut393
  Tool = -> Cylinder892
FEATURE [Part::Cut] Cut399
  Base = -> Cut398
  Tool = -> Cylinder893
FEATURE [Part::Chamfer] Chamfer002
  Base = -> Cut399
  Edges = 1 edges r=2: [Edge4]
FEATURE [Part::Box] Box478  label="Krychle478"
  AttacherType = Attacher::AttachEngine3D
  Height = 26
  Length = 50
  Placement = pos=(-112,-24,56) rot=(0,0,1;0rad)
  Width = 6
FEATURE [Part::Cylinder] Cylinder961  label="Válec961"
  Angle = 360
  AttacherType = Attacher::AttachEngine3D
  Height = 20
  Placement = pos=(-102,-10,66) rot=(0,0,1;0rad)
  Radius = 2.5
FEATURE [Part::Cylinder] Cylinder962  label="Válec962"
  Angle = 360
  AttacherType = Attacher::AttachEngine3D
  Height = 10
  Placement = pos=(0,0,72) rot=(0,0,1;0rad)
  Radius = 74
FEATURE [Part::Box] Box477  label="Krychle477"
  AttacherType = Attacher::AttachEngine3D
  Height = 6
  Length = 51
  Placement = pos=(-112,-24,76) rot=(0,0,1;0rad)
  Width = 24
FEATURE [Part::Cylinder] Cylinder897  label="Válec897"
  Angle = 360
  AttacherType = Attacher::AttachEngine3D
  Height = 32
  Placement = pos=(0,0,50) rot=(0,0,1;0rad)
  Radius = 74
FEATURE [Part::Cut] Cut401
  Base = -> Box424
  Tool = -> Cylinder897
FEATURE [Part::Chamfer] Chamfer057
  Base = -> Cut401
  Edges = 1 edges r=20: [Edge4]
FEATURE [Part::Box] Box476  label="Krychle476"
  AttacherType = Attacher::AttachEngine3D
  Height = 26
  Length = 50
  Placement = pos=(-112,-24,56) rot=(0,0,1;0rad)
  Width = 6
FEATURE [Part::Box] Box522  label="Krychle522"
  AttacherType = Attacher::AttachEngine3D
  Height = 14
  Length = 24
  Placement = pos=(68,-24,44) rot=(0,0,1;0rad)
  Width = 6
FEATURE [Part::Chamfer] Chamfer017
  Base = -> Box522
  Edges = 1 edges r=13.99: [Edge8]
FEATURE [Part::Cylinder] Cylinder966  label="Válec966"
  Angle = 360
  AttacherType = Attacher::AttachEngine3D
  Height = 32
  Placement = pos=(0,0,50) rot=(0,0,1;0rad)
  Radius = 74
FEATURE [Part::Cylinder] Cylinder964  label="Válec964"
  Angle = 360
  AttacherType = Attacher::AttachEngine3D
  Height = 32
  Placement = pos=(0,0,50) rot=(0,0,1;0rad)
  Radius = 74
FEATURE [Part::Cut] Cut443
  Base = -> Box476
  Placement = pos=(0,0,0) rot=(0,0,1;1.5708rad)
  Tool = -> Cylinder964
FEATURE [Part::Cylinder] Cylinder965  label="Válec965"
  Angle = 360
  AttacherType = Attacher::AttachEngine3D
  Height = 20
  Placement = pos=(-102,-10,66) rot=(0,0,1;0rad)
  Radius = 2.5
FEATURE [Part::Box] Box479  label="Krychle479"
  AttacherType = Attacher::AttachEngine3D
  Height = 6
  Length = 51
  Placement = pos=(-112,-24,76) rot=(0,0,1;0rad)
  Width = 24
FEATURE [Part::Box] Box480  label="Krychle480"
  AttacherType = Attacher::AttachEngine3D
  Height = 26
  Length = 50
  Placement = pos=(3,-112,56) rot=(0,0,1;1.5708rad)
  Width = 6
FEATURE [Part::Cylinder] Cylinder898  label="Válec898"
  Angle = 360
  AttacherType = Attacher::AttachEngine3D
  Height = 20
  Placement = pos=(-86,-10,66) rot=(0,0,1;0rad)
  Radius = 2.5
FEATURE [Part::Compound] Compound493
  Links = -> [Cylinder895,Cylinder898]
FEATURE [Part::Cut] Cut402
  Base = -> Cut400
  Tool = -> Compound493
FEATURE [Part::Compound] Compound494  label="stabilo_holdo_left1"
  Links = -> [Chamfer057,Cut402,Chamfer002]
FEATURE [Part::Mirroring] mirror  label="stabilo_holdo_right"
  Base = (0,0,0)
  Normal = (1,0,0)
  Placement = pos=(0,0,2) rot=(0,0,1;0rad)
  Source = -> Compound494
FEATURE [Part::Compound] Compound532  label="stabilo_holdo_right_silo"
  Links = -> [Chamfer017,mirror]
FEATURE [Part::Cylinder] Cylinder963  label="Válec963"
  Angle = 360
  AttacherType = Attacher::AttachEngine3D
  Height = 20
  Placement = pos=(-86,-10,66) rot=(0,0,1;0rad)
  Radius = 2.5
FEATURE [Part::Compound] Compound519
  Links = -> [Cylinder961,Cylinder963]
FEATURE [Part::Cylinder] Cylinder969  label="Válec969"
  Angle = 360
  AttacherType = Attacher::AttachEngine3D
  Height = 40
  Placement = pos=(0,0,42) rot=(0,0,1;0rad)
  Radius = 74
FEATURE [Part::Cylinder] Cylinder967  label="Válec967"
  Angle = 360
  AttacherType = Attacher::AttachEngine3D
  Height = 10
  Placement = pos=(0,0,72) rot=(0,0,1;0rad)
  Radius = 74
FEATURE [Part::Cylinder] Cylinder970  label="Válec970"
  Angle = 360
  AttacherType = Attacher::AttachEngine3D
  Height = 40
  Placement = pos=(0,0,42) rot=(0,0,1;0rad)
  Radius = 74
FEATURE [Part::Box] Box520  label="Krychle520"
  AttacherType = Attacher::AttachEngine3D
  Height = 14
  Length = 24
  Placement = pos=(3,-92,44) rot=(0,0,1;1.5708rad)
  Width = 6
FEATURE [Part::Box] Box481  label="Krychle481"
  AttacherType = Attacher::AttachEngine3D
  Height = 26
  Length = 8
  Placement = pos=(24,-78,56) rot=(0,0,1;1.5708rad)
  Width = 48
FEATURE [Part::Cylinder] Cylinder968  label="Válec968"
  Angle = 360
  AttacherType = Attacher::AttachEngine3D
  Height = 20
  Placement = pos=(-86,-10,66) rot=(0,0,1;0rad)
  Radius = 2.5
FEATURE [Part::Box] Box518  label="Krychle518"
  AttacherType = Attacher::AttachEngine3D
  Height = 14
  Length = 18
  Placement = pos=(3,-92,44) rot=(0,0,1;1.5708rad)
  Width = 6
FEATURE [Part::Box] Box519  label="Krychle519"
  AttacherType = Attacher::AttachEngine3D
  Height = 14
  Length = 24
  Placement = pos=(3,-92,44) rot=(0,0,1;1.5708rad)
  Width = 6
FEATURE [Part::Cut] Cut445
  Base = -> Box477
  Tool = -> Cylinder962
FEATURE [Part::Cut] Cut444
  Base = -> Cut445
  Placement = pos=(0,0,0) rot=(0,0,1;1.5708rad)
  Tool = -> Compound519
FEATURE [Part::Compound] Compound520
  Links = -> [Cut443,Cut444]
FEATURE [Part::Cut] Cut447
  Base = -> Box479
  Tool = -> Cylinder967
FEATURE [Part::Cut] Cut449
  Base = -> Box480
  Tool = -> Cylinder969
FEATURE [Part::Cut] Cut446
  Base = -> Box478
  Placement = pos=(0,0,0) rot=(0,0,1;1.5708rad)
  Tool = -> Cylinder966
FEATURE [Part::Cut] Cut450
  Base = -> Box481
  Tool = -> Cylinder970
FEATURE [Part::Compound] Compound522
  Links = -> [Cylinder965,Cylinder968]
FEATURE [Part::Cut] Cut448
  Base = -> Cut447
  Placement = pos=(0,0,0) rot=(0,0,1;1.5708rad)
  Tool = -> Compound522
FEATURE [Part::Compound] Compound521
  Links = -> [Cut446,Cut448]
FEATURE [Part::Chamfer] Chamfer011
  Base = -> Cut449
  Edges = 1 edges r=20: [Edge4]
FEATURE [Part::Chamfer] Chamfer012
  Base = -> Compound520
  Edges = 1 edges r=20: [Edge4]
FEATURE [Part::Chamfer] Chamfer013
  Base = -> Box518
  Edges = 1 edges r=13.99: [Edge4]
FEATURE [Part::Chamfer] Chamfer015
  Base = -> Box520
  Edges = 1 edges r=13.99: [Edge4]
  Placement = pos=(21,0,0) rot=(0,0,1;0rad)
FEATURE [Part::Chamfer] Chamfer014
  Base = -> Box519
  Edges = 1 edges r=13.99: [Edge4]
  Placement = pos=(-21,0,0) rot=(0,0,1;0rad)
FEATURE [Part::Mirroring] mirror003  label="Compound521 (mirrored)"
  Base = (0,0,0)
  Normal = (1,0,0)
  Source = -> Compound521
FEATURE [Part::Chamfer] Chamfer010
  Base = -> mirror003
  Edges = 1 edges r=20: [Edge4]
FEATURE [Part::Compound] Compound523  label="stabilo_front"
  Links = -> [Chamfer012,Chamfer011,Chamfer010,Cut450]
  Placement = pos=(0,0,2) rot=(0,0,1;0rad)
FEATURE [Part::Compound] Compound533  label="stabilo_front_silo"
  Links = -> [Compound523,Chamfer013,Chamfer014,Chamfer015]
FEATURE [Part::Compound] Compound889  label="Base_turret-hole"
  Links = -> [Cut453,Tube036,Cut509,Cut520,Compound531,Compound532,Compound533]
FEATURE [Part::FeaturePython] Tube  label="6203-RS"  # WARN: FeaturePython — macro-defined, semantics opaque (R4)
  AttacherType = Attacher::AttachEngine3D
  Height = 12
  InnerRadius = 8.5
  OuterRadius = 20
  Placement = pos=(0,134,49) rot=(1,0,0;1.5708rad)
FEATURE [Part::FeaturePython] Tube037  label="6004-2RS"  # WARN: FeaturePython — macro-defined, semantics opaque (R4)
  AttacherType = Attacher::AttachEngine3D
  Height = 12
  InnerRadius = 10
  OuterRadius = 21
  Placement = pos=(0,134,49) rot=(1,0,0;1.5708rad)
FEATURE [Part::FeaturePython] Tube038  label="6003-2RS"  # WARN: FeaturePython — macro-defined, semantics opaque (R4)
  AttacherType = Attacher::AttachEngine3D
  Height = 10
  InnerRadius = 8.5
  OuterRadius = 17.5
  Placement = pos=(0,132,51) rot=(1,0,0;1.5708rad)
FEATURE [Part::Cylinder] Cylinder1760  label="Válec1760"
  Angle = 360
  AttacherType = Attacher::AttachEngine3D
  Height = 50
  Placement = pos=(-71,80,56) rot=(1,0,0;1.5708rad)
  Radius = 1.5
FEATURE [Part::Cylinder] Cylinder1761  label="Válec1761"
  Angle = 360
  AttacherType = Attacher::AttachEngine3D
  Height = 50
  Placement = pos=(71,80,57) rot=(1,0,0;1.5708rad)
  Radius = 1.5
FEATURE [Part::Compound] Compound350
  Links = -> [Cylinder543,Cylinder544,Cylinder545,Cylinder546,Cylinder1760,Cylinder1761]
FEATURE [Part::Cut] Cut211
  Base = -> Cut192
  Tool = -> Compound350
FEATURE [Part::Cylinder] Cylinder1762  label="Válec1762"
  Angle = 360
  AttacherType = Attacher::AttachEngine3D
  Height = 50
  Placement = pos=(71,106,57) rot=(1,0,0;1.5708rad)
  Radius = 3
FEATURE [Part::Cylinder] Cylinder1763  label="Válec1763"
  Angle = 360
  AttacherType = Attacher::AttachEngine3D
  Height = 50
  Placement = pos=(-71,106,56) rot=(1,0,0;1.5708rad)
  Radius = 3
FEATURE [Part::Compound] Compound351
  Links = -> [Cylinder547,Cylinder548,Cylinder550,Cylinder549,Cylinder1762,Cylinder1763]
FEATURE [Part::Cut] Cut212
  Base = -> Cut211
  Tool = -> Compound351
FEATURE [Part::Compound] Compound381
  Links = -> [Cut212,Compound380]
FEATURE [Part::Compound] Compound382
  Links = -> [Box231,Compound381]
FEATURE [Part::Compound] Compound384  label="bazovina-part-I"
  Links = -> [Compound382,Compound383]
FEATURE [Part::Cylinder] Cylinder1764  label="Válec1764"
  Angle = 360
  AttacherType = Attacher::AttachEngine3D
  Height = 50
  Placement = pos=(-31,150,48) rot=(1,0,0;1.5708rad)
  Radius = 1.5
FEATURE [Part::Cylinder] Cylinder1765  label="Válec1765"
  Angle = 360
  AttacherType = Attacher::AttachEngine3D
  Height = 50
  Placement = pos=(-31,150,72) rot=(1,0,0;1.5708rad)
  Radius = 1.5
FEATURE [Part::Box] Box711  label="Krychle711"
  AttacherType = Attacher::AttachEngine3D
  Height = 2
  Length = 6
  Placement = pos=(-27,74,39) rot=(0,0,1;1.5708rad)
  Width = 8
FEATURE [Part::Box] Box712  label="Krychle712"
  AttacherType = Attacher::AttachEngine3D
  Height = 6
  Length = 2
  Placement = pos=(-28,110,45) rot=(0,0,1;1.5708rad)
  Width = 6
FEATURE [Part::Box] Box713  label="Krychle713"
  AttacherType = Attacher::AttachEngine3D
  Height = 6
  Length = 2
  Placement = pos=(-28,110,69) rot=(0,0,1;1.5708rad)
  Width = 6
FEATURE [Part::Box] Box714  label="Krychle714"
  AttacherType = Attacher::AttachEngine3D
  Height = 6
  Length = 2
  Placement = pos=(34,110,45) rot=(0,0,1;1.5708rad)
  Width = 6
FEATURE [Part::Box] Box715  label="Krychle715"
  AttacherType = Attacher::AttachEngine3D
  Height = 6
  Length = 2
  Placement = pos=(34,110,69) rot=(0,0,1;1.5708rad)
  Width = 6
FEATURE [Part::Compound] Compound
  Links = -> [Box712,Box713,Box714,Box715]
FEATURE [Part::Cylinder] Cylinder1766  label="Válec1766"
  Angle = 360
  AttacherType = Attacher::AttachEngine3D
  Height = 50
  Placement = pos=(31,150,48) rot=(1,0,0;1.5708rad)
  Radius = 1.5
FEATURE [Part::Cylinder] Cylinder1767  label="Válec1767"
  Angle = 360
  AttacherType = Attacher::AttachEngine3D
  Height = 50
  Placement = pos=(31,150,72) rot=(1,0,0;1.5708rad)
  Radius = 1.5
FEATURE [Part::Compound] Compound890
  Links = -> [Cylinder1764,Cylinder1765,Cylinder1766,Cylinder1767]
FEATURE [Part::Cylinder] Cylinder1768  label="Válec1768"
  Angle = 360
  AttacherType = Attacher::AttachEngine3D
  Height = 50
  Placement = pos=(-31,101,0) rot=(0,0,1;0.785398rad)
  Radius = 1.5
FEATURE [Part::Box] Box717  label="Krychle717"
  AttacherType = Attacher::AttachEngine3D
  Height = 2
  Length = 6
  Placement = pos=(-27,98,39) rot=(0,0,1;1.5708rad)
  Width = 8
FEATURE [Part::Box] Box718  label="Krychle718"
  AttacherType = Attacher::AttachEngine3D
  Height = 6
  Length = 8
  Placement = pos=(-19,116,46) rot=(0,0,1;0rad)
  Width = 2
FEATURE [Part::Box] Box719  label="Krychle719"
  AttacherType = Attacher::AttachEngine3D
  Height = 6
  Length = 49
  Placement = pos=(28,86,78) rot=(0,1,0;1.5708rad)
  Width = 36
FEATURE [Part::Box] Box721  label="Krychle721"
  AttacherType = Attacher::AttachEngine3D
  Height = 2
  Length = 6
  Placement = pos=(35,98,39) rot=(0,0,1;1.5708rad)
  Width = 8
FEATURE [Part::Compound] Compound893
  Links = -> [Box721]
FEATURE [Part::Compound] Compound896
  Links = -> [Cylinder1768]
FEATURE [Part::Compound] Compound897
  Links = -> [Box717]
FEATURE [Part::Cylinder] Cylinder1770  label="Válec1770"
  Angle = 360
  AttacherType = Attacher::AttachEngine3D
  Height = 50
  Placement = pos=(31,101,0) rot=(0,0,1;0.785398rad)
  Radius = 1.5
FEATURE [Part::Compound] Compound892
  Links = -> [Cylinder1770]
FEATURE [Part::Box] Box722  label="Krychle722"
  AttacherType = Attacher::AttachEngine3D
  Height = 49
  Length = 56
  Placement = pos=(-28,114,29) rot=(0,0,1;0rad)
  Width = 8
FEATURE [Part::Box] Box723  label="Krychle723"
  AttacherType = Attacher::AttachEngine3D
  Height = 6
  Length = 49
  Placement = pos=(-34,86,78) rot=(0,1,0;1.5708rad)
  Width = 36
FEATURE [Part::Box] Box724  label="Krychle724"
  AttacherType = Attacher::AttachEngine3D
  Height = 6
  Length = 8
  Placement = pos=(11,116,46) rot=(0,0,1;0rad)
  Width = 2
FEATURE [Part::Cylinder] Cylinder1772  label="Válec1772"
  Angle = 360
  AttacherType = Attacher::AttachEngine3D
  Height = 40
  Placement = pos=(16,140,49) rot=(1,0,0;1.5708rad)
  Radius = 1.5
FEATURE [Part::Cut] Cut522
  Base = -> Box723
  Tool = -> Compound897
FEATURE [Part::Cut] Cut524
  Base = -> Box719
  Tool = -> Compound892
FEATURE [Part::Cut] Cut525
  Base = -> Cut524
  Tool = -> Compound893
FEATURE [Part::Cut] Cut526
  Base = -> Cut522
  Tool = -> Compound896
FEATURE [Part::Cylinder] Cylinder1773  label="Válec1773"
  Angle = 360
  AttacherType = Attacher::AttachEngine3D
  Height = 40
  Placement = pos=(-16,140,49) rot=(1,0,0;1.5708rad)
  Radius = 1.5
FEATURE [Part::Box] Box725  label="Krychle725"
  AttacherType = Attacher::AttachEngine3D
  Height = 8
  Length = 6
  Placement = pos=(-3,116,30) rot=(0,0,1;0rad)
  Width = 2
FEATURE [Part::Cylinder] Cylinder1774  label="Válec1774"
  Angle = 360
  AttacherType = Attacher::AttachEngine3D
  Height = 20
  Placement = pos=(0,124,51) rot=(1,0,0;1.5708rad)
  Radius = 12
FEATURE [Part::Cylinder] Cylinder1775  label="Válec1775"
  Angle = 360
  AttacherType = Attacher::AttachEngine3D
  Height = 40
  Placement = pos=(0,140,65) rot=(1,0,0;1.5708rad)
  Radius = 1.5
FEATURE [Part::Cylinder] Cylinder1776  label="Válec1776"
  Angle = 360
  AttacherType = Attacher::AttachEngine3D
  Height = 40
  Placement = pos=(0,140,33) rot=(1,0,0;1.5708rad)
  Radius = 1.5
FEATURE [Part::Compound] Compound891
  Links = -> [Cylinder1775,Cylinder1772,Cylinder1773,Cylinder1776]
  Placement = pos=(-34.65,0,16.35) rot=(0,1,0;0.785398rad)
FEATURE [Part::Cut] Cut523
  Base = -> Box722
  Tool = -> Compound891
FEATURE [Part::Box] Box726  label="Krychle726"
  AttacherType = Attacher::AttachEngine3D
  Height = 8
  Length = 6
  Placement = pos=(-3,116,60) rot=(0,0,1;0rad)
  Width = 2
FEATURE [Part::Compound] Compound895
  Links = -> [Box726,Box725,Box718,Box724]
  Placement = pos=(-34.65,0,16.35) rot=(0,1,0;0.785398rad)
FEATURE [Part::Cut] Cut528
  Base = -> Cut523
  Tool = -> Cylinder1774
FEATURE [Part::Cut] Cut527
  Base = -> Cut528
  Tool = -> Compound895
FEATURE [Part::Compound] Compound894
  Links = -> [Cut527,Cut526,Cut525]
FEATURE [Part::Cut] Cut529
  Base = -> Compound894
  Tool = -> Compound890
FEATURE [Part::Cut] Cut530
  Base = -> Cut529
  Tool = -> Compound
FEATURE [Part::Cylinder] Cylinder1777  label="Válec1777"
  Angle = 360
  AttacherType = Attacher::AttachEngine3D
  Height = 55
  Placement = pos=(-76.3,104,29) rot=(0,0,1;0rad)
  Radius = 46
FEATURE [Part::Box] Box727  label="Krychle727"
  AttacherType = Attacher::AttachEngine3D
  Height = 55
  Length = 148
  Placement = pos=(-74,48,29) rot=(0,0,1;0rad)
  Width = 38
FEATURE [Part::Cylinder] Cylinder1778  label="Válec1778"
  Angle = 360
  AttacherType = Attacher::AttachEngine3D
  Height = 55
  Placement = pos=(76.3,104,29) rot=(0,0,1;0rad)
  Radius = 46
FEATURE [Part::Cylinder] Cylinder1779  label="Válec1779"
  Angle = 360
  AttacherType = Attacher::AttachEngine3D
  Height = 55
  Placement = pos=(0,0,29) rot=(0,0,1;0rad)
  Radius = 74
FEATURE [Part::Box] Box728  label="Krychle728"
  AttacherType = Attacher::AttachEngine3D
  Height = 55
  Length = 56
  Placement = pos=(-28,0,29) rot=(0,0,1;0rad)
  Width = 200
FEATURE [Part::Cut] Cut536
  Base = -> Box727
  Tool = -> Cylinder1777
FEATURE [Part::Cut] Cut531
  Base = -> Cut536
  Tool = -> Cylinder1778
FEATURE [Part::Cut] Cut534
  Base = -> Cut531
  Tool = -> Box728
FEATURE [Part::Cut] Cut535
  Base = -> Cut534
  Tool = -> Cylinder1779
FEATURE [Part::Cylinder] Cylinder1780  label="Válec1780"
  Angle = 360
  AttacherType = Attacher::AttachEngine3D
  Height = 50
  Placement = pos=(-71,80,73) rot=(1,0,0;1.5708rad)
  Radius = 1.5
FEATURE [Part::Cylinder] Cylinder1781  label="Válec1781"
  Angle = 360
  AttacherType = Attacher::AttachEngine3D
  Height = 50
  Placement = pos=(-71,106,73) rot=(1,0,0;1.5708rad)
  Radius = 3
FEATURE [Part::Cylinder] Cylinder1782  label="Válec1782"
  Angle = 360
  AttacherType = Attacher::AttachEngine3D
  Height = 50
  Placement = pos=(-71,106,39) rot=(1,0,0;1.5708rad)
  Radius = 3
FEATURE [Part::Cylinder] Cylinder1783  label="Válec1783"
  Angle = 360
  AttacherType = Attacher::AttachEngine3D
  Height = 50
  Placement = pos=(71,106,73) rot=(1,0,0;1.5708rad)
  Radius = 3
FEATURE [Part::Cylinder] Cylinder1784  label="Válec1784"
  Angle = 360
  AttacherType = Attacher::AttachEngine3D
  Height = 50
  Placement = pos=(-71,80,39) rot=(1,0,0;1.5708rad)
  Radius = 1.5
FEATURE [Part::Cylinder] Cylinder1785  label="Válec1785"
  Angle = 360
  AttacherType = Attacher::AttachEngine3D
  Height = 50
  Placement = pos=(71,106,39) rot=(1,0,0;1.5708rad)
  Radius = 3
FEATURE [Part::Cylinder] Cylinder1786  label="Válec1786"
  Angle = 360
  AttacherType = Attacher::AttachEngine3D
  Height = 50
  Placement = pos=(71,80,39) rot=(1,0,0;1.5708rad)
  Radius = 1.5
FEATURE [Part::Cylinder] Cylinder1787  label="Válec1787"
  Angle = 360
  AttacherType = Attacher::AttachEngine3D
  Height = 50
  Placement = pos=(71,80,73) rot=(1,0,0;1.5708rad)
  Radius = 1.5
FEATURE [Part::Cylinder] Cylinder1788  label="Válec1788"
  Angle = 360
  AttacherType = Attacher::AttachEngine3D
  Height = 50
  Placement = pos=(-71,80,56) rot=(1,0,0;1.5708rad)
  Radius = 1.5
FEATURE [Part::Cylinder] Cylinder1789  label="Válec1789"
  Angle = 360
  AttacherType = Attacher::AttachEngine3D
  Height = 50
  Placement = pos=(71,80,57) rot=(1,0,0;1.5708rad)
  Radius = 1.5
FEATURE [Part::Compound] Compound899
  Links = -> [Cylinder1784,Cylinder1786,Cylinder1780,Cylinder1787,Cylinder1788,Cylinder1789]
FEATURE [Part::Cut] Cut532
  Base = -> Cut535
  Tool = -> Compound899
FEATURE [Part::Cylinder] Cylinder1790  label="Válec1790"
  Angle = 360
  AttacherType = Attacher::AttachEngine3D
  Height = 50
  Placement = pos=(71,106,57) rot=(1,0,0;1.5708rad)
  Radius = 3
FEATURE [Part::Cylinder] Cylinder1791  label="Válec1791"
  Angle = 360
  AttacherType = Attacher::AttachEngine3D
  Height = 50
  Placement = pos=(-71,106,56) rot=(1,0,0;1.5708rad)
  Radius = 3
FEATURE [Part::Compound] Compound898
  Links = -> [Cylinder1782,Cylinder1785,Cylinder1781,Cylinder1783,Cylinder1790,Cylinder1791]
FEATURE [Part::Cut] Cut533
  Base = -> Cut532
  Tool = -> Compound898
FEATURE [Part::Box] Box729  label="Krychle729"
  AttacherType = Attacher::AttachEngine3D
  Height = 2
  Length = 6
  Placement = pos=(35,74,39) rot=(0,0,1;1.5708rad)
  Width = 8
FEATURE [Part::Cylinder] Cylinder1792  label="Válec1792"
  Angle = 360
  AttacherType = Attacher::AttachEngine3D
  Height = 12
  Placement = pos=(0,83,68) rot=(0,0,1;0rad)
  Radius = 14
FEATURE [Part::Cylinder] Cylinder1793  label="Válec1793"
  Angle = 360
  AttacherType = Attacher::AttachEngine3D
  Height = 6
  Placement = pos=(0,83,68) rot=(0,0,1;0rad)
  Radius = 8
FEATURE [Part::Cut] Cut537
  Base = -> Cylinder1792
  Tool = -> Cylinder1793
FEATURE [Part::FeaturePython] Tube039  # WARN: FeaturePython — macro-defined, semantics opaque (R4)
  AttacherType = Attacher::AttachEngine3D
  Height = 1
  InnerRadius = 7
  OuterRadius = 8
  Placement = pos=(0,83,73) rot=(0,0,1;0rad)
FEATURE [Part::Compound] Compound900
  Links = -> [Cut537,Tube039]
FEATURE [Part::Cylinder] Cylinder1794  label="Válec1794"
  Angle = 360
  AttacherType = Attacher::AttachEngine3D
  Height = 50
  Placement = pos=(31,77,0) rot=(0,0,1;0.785398rad)
  Radius = 1.5
FEATURE [Part::Cylinder] Cylinder1795  label="Válec1795"
  Angle = 360
  AttacherType = Attacher::AttachEngine3D
  Height = 50
  Placement = pos=(-31,77,0) rot=(0,0,1;0.785398rad)
  Radius = 1.5
FEATURE [Part::Compound] Compound901
  Links = -> [Box729,Box711]
FEATURE [Part::Compound] Compound902
  Links = -> [Cylinder1794,Cylinder1795]
FEATURE [Part::Cut] Cut538
  Base = -> Cut533
  Tool = -> Compound901
FEATURE [Part::Cut] Cut539
  Base = -> Cut538
  Tool = -> Compound902
FEATURE [Part::Box] Box730  label="Krychle730"
  AttacherType = Attacher::AttachEngine3D
  Height = 6
  Length = 68
  Placement = pos=(-34,68,78) rot=(0,0,1;0rad)
  Width = 54
FEATURE [Part::Cylinder] Cylinder1796  label="Válec1796"
  Angle = 360
  AttacherType = Attacher::AttachEngine3D
  Height = 50
  Placement = pos=(-22,118,0) rot=(0,0,1;0.785398rad)
  Radius = 1.5
FEATURE [Part::Box] Box731  label="Krychle731"
  AttacherType = Attacher::AttachEngine3D
  Height = 2
  Length = 8
  Placement = pos=(25,114,39) rot=(0,0,1;1.5708rad)
  Width = 6
FEATURE [Part::Cylinder] Cylinder1797  label="Válec1797"
  Angle = 360
  AttacherType = Attacher::AttachEngine3D
  Height = 50
  Placement = pos=(22,118,0) rot=(0,0,1;0.785398rad)
  Radius = 1.5
FEATURE [Part::Box] Box732  label="Krychle732"
  AttacherType = Attacher::AttachEngine3D
  Height = 2
  Length = 8
  Placement = pos=(-19,114,39) rot=(0,0,1;1.5708rad)
  Width = 6
FEATURE [Part::Compound] Compound903
  Links = -> [Cylinder1796,Cylinder1797]
FEATURE [Part::Compound] Compound904
  Links = -> [Box731,Box732]
FEATURE [Part::Cut] Cut540
  Base = -> Cut530
  Tool = -> Compound903
FEATURE [Part::Cut] Cut541
  Base = -> Cut540
  Tool = -> Compound904
FEATURE [Mesh::Feature] Mesh  label="Base_rear-gearbox (Meshed)"
FEATURE [Part::Cylinder] Cylinder1798  label="Válec1798"
  Angle = 360
  AttacherType = Attacher::AttachEngine3D
  Height = 20
  Placement = pos=(-84,-12,66) rot=(0,0,1;0rad)
  Radius = 2.5
FEATURE [Part::Box] Box733  label="Krychle733"
  AttacherType = Attacher::AttachEngine3D
  Height = 2
  Length = 6
  Placement = pos=(-67,102,35) rot=(0,0,1;0rad)
  Width = 6
FEATURE [Part::Box] Box734  label="Krychle734"
  AttacherType = Attacher::AttachEngine3D
  Height = 2
  Length = 6
  Placement = pos=(-46,102,35) rot=(0,0,1;0rad)
  Width = 6
FEATURE [Part::Cylinder] Cylinder1799  label="Válec1799"
  Angle = 360
  AttacherType = Attacher::AttachEngine3D
  Height = 16
  Placement = pos=(-43,117,25) rot=(0,0,1;0rad)
  Radius = 1.5
FEATURE [Part::Cylinder] Cylinder1800  label="Válec1800"
  Angle = 360
  AttacherType = Attacher::AttachEngine3D
  Height = 16
  Placement = pos=(-64,117,25) rot=(0,0,1;0rad)
  Radius = 1.5
FEATURE [Part::Box] Box735  label="Krychle735"
  AttacherType = Attacher::AttachEngine3D
  Height = 15
  Length = 15
  Placement = pos=(-61,102,41) rot=(0,0,1;0rad)
  Width = 80
FEATURE [Part::Box] Box736  label="Krychle736"
  AttacherType = Attacher::AttachEngine3D
  Height = 24
  Length = 33
  Placement = pos=(-67,98,50) rot=(0,0,1;0rad)
  Width = 24
FEATURE [Part::Chamfer] Chamfer
  Base = -> Box736
  Edges = 1 edges r=23.9: [Edge2]
FEATURE [Part::Box] Box248  label="Krychle248"
  AttacherType = Attacher::AttachEngine3D
  Height = 19
  Length = 33
  Placement = pos=(-67,98,41) rot=(0,0,1;0rad)
  Width = 24
FEATURE [Part::Box] Box737  label="Krychle737"
  AttacherType = Attacher::AttachEngine3D
  Height = 15
  Length = 15
  Placement = pos=(-61,102,41) rot=(0,0,1;0rad)
  Width = 80
FEATURE [Part::Cut] Cut543
  Base = -> Box248
  Placement = pos=(0,0,-10) rot=(0,0,1;0rad)
  Tool = -> Box737
FEATURE [Part::Box] Box738  label="Krychle738"
  AttacherType = Attacher::AttachEngine3D
  Height = 24
  Length = 40
  Placement = pos=(-74,116,50) rot=(0,0,1;0rad)
  Width = 6
FEATURE [Part::Chamfer] Chamfer001
  Base = -> Box738
  Edges = 1 edges r=7: [Edge4]
FEATURE [Part::Box] Box739  label="Krychle739"
  AttacherType = Attacher::AttachEngine3D
  Height = 6
  Length = 40
  Placement = pos=(-101,-24,76) rot=(0,0,1;0rad)
  Width = 24
FEATURE [Part::Cylinder] Cylinder1801  label="Válec1801"
  Angle = 360
  AttacherType = Attacher::AttachEngine3D
  Height = 20
  Placement = pos=(-102,-16,66) rot=(0,0,1;0rad)
  Radius = 2.5
FEATURE [Part::Box] Box740  label="Krychle740"
  AttacherType = Attacher::AttachEngine3D
  Height = 24
  Length = 40
  Placement = pos=(-74,98,50) rot=(0,0,1;0rad)
  Width = 6
FEATURE [Part::Chamfer] Chamfer058
  Base = -> Box740
  Edges = 1 edges r=7: [Edge4]
FEATURE [Part::Box] Box741  label="Krychle741"
  AttacherType = Attacher::AttachEngine3D
  Height = 2
  Length = 6
  Placement = pos=(-67,114,35) rot=(0,0,1;0rad)
  Width = 6
FEATURE [Part::Box] Box487  label="Krychle487"
  AttacherType = Attacher::AttachEngine3D
  Height = 2
  Length = 6
  Placement = pos=(-46,114,35) rot=(0,0,1;0rad)
  Width = 6
FEATURE [Part::Cylinder] Cylinder1802  label="Válec1802"
  Angle = 360
  AttacherType = Attacher::AttachEngine3D
  Height = 16
  Placement = pos=(-43,105,25) rot=(0,0,1;0rad)
  Radius = 1.5
FEATURE [Part::Cylinder] Cylinder1803  label="Válec1803"
  Angle = 360
  AttacherType = Attacher::AttachEngine3D
  Height = 16
  Placement = pos=(-64,105,25) rot=(0,0,1;0rad)
  Radius = 1.5
FEATURE [Part::Cylinder] Cylinder1804  label="Válec1804"
  Angle = 360
  AttacherType = Attacher::AttachEngine3D
  Height = 20
  Placement = pos=(-102,-16,66) rot=(0,0,1;0rad)
  Radius = 2.5
FEATURE [Part::Box] Box742  label="Krychle742"
  AttacherType = Attacher::AttachEngine3D
  Height = 6
  Length = 40
  Placement = pos=(-101,-24,76) rot=(0,0,1;0rad)
  Width = 24
FEATURE [Part::Box] Box743  label="Krychle743"
  AttacherType = Attacher::AttachEngine3D
  Height = 2
  Length = 6
  Placement = pos=(-46,114,35) rot=(0,0,1;0rad)
  Width = 6
FEATURE [Part::Box] Box744  label="Krychle744"
  AttacherType = Attacher::AttachEngine3D
  Height = 24
  Length = 40
  Placement = pos=(-74,116,50) rot=(0,0,1;0rad)
  Width = 6
FEATURE [Part::Chamfer] Chamfer060
  Base = -> Box744
  Edges = 1 edges r=7: [Edge4]
FEATURE [Part::Box] Box745  label="Krychle745"
  AttacherType = Attacher::AttachEngine3D
  Height = 2
  Length = 6
  Placement = pos=(-67,114,35) rot=(0,0,1;0rad)
  Width = 6
FEATURE [Part::Cylinder] Cylinder1805  label="Válec1805"
  Angle = 360
  AttacherType = Attacher::AttachEngine3D
  Height = 20
  Placement = pos=(-84,-12,66) rot=(0,0,1;0rad)
  Radius = 2.5
FEATURE [Part::Box] Box746  label="Krychle746"
  AttacherType = Attacher::AttachEngine3D
  Height = 24
  Length = 40
  Placement = pos=(-74,98,50) rot=(0,0,1;0rad)
  Width = 6
FEATURE [Part::Chamfer] Chamfer005
  Base = -> Box746
  Edges = 1 edges r=7: [Edge4]
FEATURE [Part::Box] Box747  label="Krychle747"
  AttacherType = Attacher::AttachEngine3D
  Height = 19
  Length = 33
  Placement = pos=(-67,98,41) rot=(0,0,1;0rad)
  Width = 24
FEATURE [Part::Box] Box748  label="Krychle748"
  AttacherType = Attacher::AttachEngine3D
  Height = 24
  Length = 33
  Placement = pos=(-67,98,50) rot=(0,0,1;0rad)
  Width = 24
FEATURE [Part::Chamfer] Chamfer059
  Base = -> Box748
  Edges = 1 edges r=23.9: [Edge2]
FEATURE [Part::Compound] Compound906
  Links = -> [Cylinder1801,Cylinder1798]
  Placement = pos=(-10,0,0) rot=(0,0,1;0rad)
FEATURE [Part::Cut] Cut542
  Base = -> Box739
  Placement = pos=(27,122,-2) rot=(0,0,1;0rad)
  Tool = -> Compound906
FEATURE [Part::Compound] Compound908
  Links = -> [Cylinder1799,Cylinder1802,Cylinder1800,Cylinder1803]
FEATURE [Part::Cut] Cut544
  Base = -> Cut543
  Tool = -> Compound908
FEATURE [Part::Compound] Compound909
  Links = -> [Box733,Box741,Box734,Box487]
FEATURE [Part::Compound] Compound524
  Links = -> [Cylinder1804,Cylinder1805]
  Placement = pos=(-10,0,0) rot=(0,0,1;0rad)
FEATURE [Part::Cut] Cut545
  Base = -> Box742
  Placement = pos=(27,122,-2) rot=(0,0,1;0rad)
  Tool = -> Compound524
FEATURE [Part::Cut] Cut547
  Base = -> Box747
  Placement = pos=(0,0,-10) rot=(0,0,1;0rad)
  Tool = -> Box735
FEATURE [Part::Cut] Cut549
  Base = -> Cut544
  Tool = -> Compound909
FEATURE [Part::Compound] Compound910  label="stabilo_left_back"
  Links = -> [Chamfer058,Chamfer001,Chamfer,Cut542,Cut549]
  Placement = pos=(-2,0,4) rot=(0,0,1;0rad)
FEATURE [Part::Box] Box749  label="Krychle749"
  AttacherType = Attacher::AttachEngine3D
  Height = 2
  Length = 6
  Placement = pos=(-67,102,35) rot=(0,0,1;0rad)
  Width = 6
FEATURE [Part::Cylinder] Cylinder1806  label="Válec1806"
  Angle = 360
  AttacherType = Attacher::AttachEngine3D
  Height = 16
  Placement = pos=(-43,105,25) rot=(0,0,1;0rad)
  Radius = 1.5
FEATURE [Part::Cylinder] Cylinder1807  label="Válec1807"
  Angle = 360
  AttacherType = Attacher::AttachEngine3D
  Height = 16
  Placement = pos=(-43,117,25) rot=(0,0,1;0rad)
  Radius = 1.5
FEATURE [Part::Cylinder] Cylinder1808  label="Válec1808"
  Angle = 360
  AttacherType = Attacher::AttachEngine3D
  Height = 16
  Placement = pos=(-64,105,25) rot=(0,0,1;0rad)
  Radius = 1.5
FEATURE [Part::Box] Box750  label="Krychle750"
  AttacherType = Attacher::AttachEngine3D
  Height = 2
  Length = 6
  Placement = pos=(-46,102,35) rot=(0,0,1;0rad)
  Width = 6
FEATURE [Part::Compound] Compound527
  Links = -> [Box749,Box745,Box750,Box743]
FEATURE [Part::Cylinder] Cylinder1809  label="Válec1809"
  Angle = 360
  AttacherType = Attacher::AttachEngine3D
  Height = 16
  Placement = pos=(-64,117,25) rot=(0,0,1;0rad)
  Radius = 1.5
FEATURE [Part::Compound] Compound526
  Links = -> [Cylinder1807,Cylinder1806,Cylinder1809,Cylinder1808]
FEATURE [Part::Cut] Cut546
  Base = -> Cut547
  Tool = -> Compound526
FEATURE [Part::Cut] Cut548
  Base = -> Cut546
  Tool = -> Compound527
FEATURE [Part::Compound] Compound907  label="stabilo_left_back001"
  Links = -> [Chamfer005,Chamfer060,Chamfer059,Cut545,Cut548]
FEATURE [Part::Mirroring] mirror004  label="stabilo_right_back"
  Base = (0,0,0)
  Normal = (1,0,0)
  Placement = pos=(2,0,4) rot=(0,0,1;0rad)
  Source = -> Compound907
FEATURE [Part::Box] Box  label="Krychle"
  AttacherType = Attacher::AttachEngine3D
  Height = 49
  Length = 2
  Placement = pos=(34,98,35) rot=(0,0,1;0rad)
  Width = 24
FEATURE [Part::Box] Box751  label="Krychle751"
  AttacherType = Attacher::AttachEngine3D
  Height = 49
  Length = 2
  Placement = pos=(-36,98,35) rot=(0,0,1;0rad)
  Width = 24
FEATURE [Part::Cylinder] Cylinder665  label="Válec665"
  Angle = 360
  AttacherType = Attacher::AttachEngine3D
  Height = 36
  Placement = pos=(76.3,104,16) rot=(0,0,1;0rad)
  Radius = 46
FEATURE [Part::Cylinder] Cylinder666  label="Válec666"
  Angle = 360
  AttacherType = Attacher::AttachEngine3D
  Height = 36
  Placement = pos=(-76.3,104,16) rot=(0,0,1;0rad)
  Radius = 46
FEATURE [Part::Box] Box752  label="Krychle752"
  AttacherType = Attacher::AttachEngine3D
  Height = 15
  Length = 148
  Placement = pos=(-74,48,16) rot=(0,0,1;0rad)
  Width = 38
FEATURE [Part::Cut] Cut269
  Base = -> Box752
  Tool = -> Cylinder666
FEATURE [Part::Cut] Cut270
  Base = -> Cut269
  Tool = -> Cylinder665
FEATURE [Part::Cylinder] Cylinder672  label="Válec672"
  Angle = 360
  AttacherType = Attacher::AttachEngine3D
  Height = 50
  Placement = pos=(31,110,0) rot=(0,0,1;0.785398rad)
  Radius = 1.5
FEATURE [Part::Cylinder] Cylinder673  label="Válec673"
  Angle = 360
  AttacherType = Attacher::AttachEngine3D
  Height = 50
  Placement = pos=(-31,110,0) rot=(0,0,1;0.785398rad)
  Radius = 1.5
FEATURE [Part::Cylinder] Cylinder674  label="Válec674"
  Angle = 360
  AttacherType = Attacher::AttachEngine3D
  Height = 6
  Placement = pos=(0,86,16) rot=(0,0,1;0rad)
  Radius = 16
FEATURE [Part::Cylinder] Cylinder675  label="Válec675"
  Angle = 360
  AttacherType = Attacher::AttachEngine3D
  Height = 50
  Placement = pos=(-31,110,0) rot=(0,0,1;0.785398rad)
  Radius = 1.5
FEATURE [Part::Cylinder] Cylinder676  label="Válec676"
  Angle = 360
  AttacherType = Attacher::AttachEngine3D
  Height = 3
  Placement = pos=(31,92,21) rot=(0,0,1;0.785398rad)
  Radius = 3
FEATURE [Part::Cylinder] Cylinder677  label="Válec677"
  Angle = 360
  AttacherType = Attacher::AttachEngine3D
  Height = 50
  Placement = pos=(-71,106,24) rot=(1,0,0;1.5708rad)
  Radius = 3
FEATURE [Part::Cylinder] Cylinder678  label="Válec678"
  Angle = 360
  AttacherType = Attacher::AttachEngine3D
  Height = 50
  Placement = pos=(71,106,24) rot=(1,0,0;1.5708rad)
  Radius = 3
FEATURE [Part::Cylinder] Cylinder679  label="Válec679"
  Angle = 360
  AttacherType = Attacher::AttachEngine3D
  Height = 50
  Placement = pos=(71,80,24) rot=(1,0,0;1.5708rad)
  Radius = 1.5
FEATURE [Part::Compound] Compound398
  Links = -> [Cylinder678,Cylinder677]
FEATURE [Part::Cylinder] Cylinder671  label="Válec671"
  Angle = 360
  AttacherType = Attacher::AttachEngine3D
  Height = 6
  Placement = pos=(0,86,21) rot=(0,0,1;0rad)
  Radius = 34
FEATURE [Part::Box] Box249  label="Krychle249"
  AttacherType = Attacher::AttachEngine3D
  Height = 4
  Length = 68
  Placement = pos=(-34,86,27) rot=(0,0,1;0rad)
  Width = 36
FEATURE [Part::Box] Box250  label="Krychle250"
  AttacherType = Attacher::AttachEngine3D
  Height = 40
  Length = 148
  Placement = pos=(-74,46,16) rot=(0,0,1;0rad)
  Width = 40
FEATURE [Part::Cut] Cut271
  Base = -> Cylinder671
  Tool = -> Box250
FEATURE [Part::Cylinder] Cylinder668  label="Válec668"
  Angle = 360
  AttacherType = Attacher::AttachEngine3D
  Height = 3
  Placement = pos=(31,110,0) rot=(0,0,1;0.785398rad)
  Radius = 3
FEATURE [Part::Cylinder] Cylinder667  label="Válec667"
  Angle = 360
  AttacherType = Attacher::AttachEngine3D
  Height = 15
  Placement = pos=(0,0,16) rot=(0,0,1;0rad)
  Radius = 74
FEATURE [Part::Cut] Cut267
  Base = -> Cut270
  Tool = -> Cylinder667
FEATURE [Part::Box] Box251  label="Krychle251"
  AttacherType = Attacher::AttachEngine3D
  Height = 40
  Length = 148
  Placement = pos=(-74,42,16) rot=(0,0,1;0rad)
  Width = 40
FEATURE [Part::Cut] Cut268
  Base = -> Cylinder674
  Tool = -> Box251
FEATURE [Part::Cylinder] Cylinder669  label="Válec669"
  Angle = 360
  AttacherType = Attacher::AttachEngine3D
  Height = 50
  Placement = pos=(-31,92,0) rot=(0,0,1;0.785398rad)
  Radius = 1.5
FEATURE [Part::Cylinder] Cylinder670  label="Válec670"
  Angle = 360
  AttacherType = Attacher::AttachEngine3D
  Height = 50
  Placement = pos=(-71,80,24) rot=(1,0,0;1.5708rad)
  Radius = 1.5
FEATURE [Part::Compound] Compound395
  Links = -> [Cylinder679,Cylinder670]
FEATURE [Part::Cut] Cut272
  Base = -> Cut267
  Tool = -> Compound395
FEATURE [Part::Cut] Cut273
  Base = -> Cut272
  Tool = -> Compound398
FEATURE [Part::Cylinder] Cylinder685  label="Válec685"
  Angle = 360
  AttacherType = Attacher::AttachEngine3D
  Height = 50
  Placement = pos=(31,92,0) rot=(0,0,1;0.785398rad)
  Radius = 1.5
FEATURE [Part::Cylinder] Cylinder683  label="Válec683"
  Angle = 360
  AttacherType = Attacher::AttachEngine3D
  Height = 3
  Placement = pos=(-31,110,0) rot=(0,0,1;0.785398rad)
  Radius = 3
FEATURE [Part::Cylinder] Cylinder681  label="Válec681"
  Angle = 360
  AttacherType = Attacher::AttachEngine3D
  Height = 50
  Placement = pos=(-31,92,0) rot=(0,0,1;0.785398rad)
  Radius = 1.5
FEATURE [Part::Cylinder] Cylinder682  label="Válec682"
  Angle = 360
  AttacherType = Attacher::AttachEngine3D
  Height = 6
  Placement = pos=(0,83,25) rot=(0,0,1;0rad)
  Radius = 8
FEATURE [Part::Cylinder] Cylinder684  label="Válec684"
  Angle = 360
  AttacherType = Attacher::AttachEngine3D
  Height = 6
  Placement = pos=(0,83,25) rot=(0,0,1;0rad)
  Radius = 8
FEATURE [Part::Cut] Cut278
  Base = -> Cut273
  Tool = -> Cylinder684
FEATURE [Part::Cylinder] Cylinder680  label="Válec680"
  Angle = 360
  AttacherType = Attacher::AttachEngine3D
  Height = 50
  Placement = pos=(31,92,0) rot=(0,0,1;0.785398rad)
  Radius = 1.5
FEATURE [Part::Compound] Compound397
  Links = -> [Cylinder673,Cylinder669,Cylinder672,Cylinder680]
FEATURE [Part::Cut] Cut276
  Base = -> Box249
  Tool = -> Compound397
FEATURE [Part::Cut] Cut266
  Base = -> Cut276
  Tool = -> Cylinder682
FEATURE [Part::Cylinder] Cylinder687  label="Válec687"
  Angle = 360
  AttacherType = Attacher::AttachEngine3D
  Height = 6
  Placement = pos=(0,83,25) rot=(0,0,1;0rad)
  Radius = 8
FEATURE [Part::Cylinder] Cylinder688  label="Válec688"
  Angle = 360
  AttacherType = Attacher::AttachEngine3D
  Height = 3
  Placement = pos=(-31,92,21) rot=(0,0,1;0.785398rad)
  Radius = 3
FEATURE [Part::Compound] Compound400
  Links = -> [Cylinder683,Cylinder688,Cylinder668,Cylinder676]
FEATURE [Part::Cylinder] Cylinder686  label="Válec686"
  Angle = 360
  AttacherType = Attacher::AttachEngine3D
  Height = 50
  Placement = pos=(31,110,0) rot=(0,0,1;0.785398rad)
  Radius = 1.5
FEATURE [Part::Compound] Compound396
  Links = -> [Cylinder675,Cylinder681,Cylinder686,Cylinder685]
FEATURE [Part::Cut] Cut277
  Base = -> Cut271
  Tool = -> Compound396
FEATURE [Part::Cut] Cut275
  Base = -> Cut277
  Tool = -> Compound400
FEATURE [Part::Cut] Cut274
  Base = -> Cut275
  Tool = -> Cylinder687
FEATURE [Part::Compound] Compound399  label="Base_rear-gearbox-cover1"
  Links = -> [Cut278,Cut266,Cut274,Cut268]
  Placement = pos=(0,0,-2) rot=(0,0,1;0rad)
FEATURE [Sketcher::SketchObject] Sketch007
  FullyConstrained = false
  MapMode = 5
  Placement = pos=(0,0,0) rot=(1,0,0;1.5708rad)
  Support = -> [XZ_Plane007]
  sketch-geometry (31):
    g0: LineSegment StartX=0 StartY=-49.2912 StartZ=0 EndX=22.5 EndY=-49.2912 EndZ=0
    g1: LineSegment StartX=22.5 StartY=-49.2912 StartZ=0 EndX=22.5 EndY=-53.2912 EndZ=0
    g2: LineSegment StartX=22.5 StartY=-53.2912 StartZ=0 EndX=0 EndY=-53.2912 EndZ=0
    g3: LineSegment StartX=0 StartY=-53.2912 StartZ=0 EndX=0 EndY=-49.2912 EndZ=0
    g4: LineSegment StartX=22.5 StartY=-49.2912 StartZ=0 EndX=26.5 EndY=-49.2912 EndZ=0
    g5: LineSegment StartX=26.5 StartY=-49.2912 StartZ=0 EndX=26.5 EndY=-44.2912 EndZ=0
    g6: LineSegment StartX=26.5 StartY=-44.2912 StartZ=0 EndX=22.5 EndY=-44.2912 EndZ=0
    g7: LineSegment StartX=22.5 StartY=-44.2912 StartZ=0 EndX=22.5 EndY=-49.2912 EndZ=0
    g8: LineSegment StartX=22.5 StartY=-49.2912 StartZ=0 EndX=0 EndY=-49.2912 EndZ=0
    g9: LineSegment StartX=0 StartY=-49.2912 StartZ=0 EndX=0 EndY=-44.2912 EndZ=0
    g10: LineSegment StartX=0 StartY=-44.2912 StartZ=0 EndX=22.5 EndY=-44.2912 EndZ=0
    g11: LineSegment StartX=22.5 StartY=-44.2912 StartZ=0 EndX=22.5 EndY=-49.2912 EndZ=0
    g12: LineSegment StartX=0 StartY=-44.2912 StartZ=0 EndX=22.5 EndY=-49.2912 EndZ=0
    g13: LineSegment StartX=22.5 StartY=-49.2912 StartZ=0 EndX=22.0661 EndY=-51.2436 EndZ=0
    g14: LineSegment StartX=22.5 StartY=-49.2912 StartZ=0 EndX=22.9339 EndY=-47.3388 EndZ=0
    g15: LineSegment StartX=22.9339 StartY=-47.3388 StartZ=0 EndX=0 EndY=-44.2912 EndZ=0
    g16: LineSegment StartX=22.0661 StartY=-51.2436 StartZ=0 EndX=0 EndY=-44.2912 EndZ=0
    g17: LineSegment StartX=22.9339 StartY=-47.3388 StartZ=0 EndX=15.0036 EndY=-46.285 EndZ=0
    g18: LineSegment StartX=15.0036 StartY=-46.285 StartZ=0 EndX=14.3355 EndY=-49.2912 EndZ=0
    g19: LineSegment StartX=15.0036 StartY=-44.2912 StartZ=0 EndX=15.0036 EndY=-46.285 EndZ=0
    g20: LineSegment StartX=22.0661 StartY=-51.2436 StartZ=0 EndX=22.0661 EndY=-53.2912 EndZ=0
    g21: LineSegment StartX=22.9339 StartY=-47.3388 StartZ=0 EndX=26.5 EndY=-47.3388 EndZ=0
    g22: LineSegment StartX=15.0036 StartY=-44.2912 StartZ=0 EndX=15.0036 EndY=-46.5552 EndZ=0
    g23: LineSegment StartX=15.0036 StartY=-46.5552 StartZ=0 EndX=14.3773 EndY=-49.1034 EndZ=0
    g24: LineSegment StartX=14.3773 StartY=-49.1034 StartZ=0 EndX=22.0661 EndY=-51.2436 EndZ=0
    g25: LineSegment StartX=22.0661 StartY=-51.2436 StartZ=0 EndX=22.5 EndY=-49.2912 EndZ=0
    g26: LineSegment StartX=22.5 StartY=-49.2912 StartZ=0 EndX=26.5 EndY=-49.2912 EndZ=0
    g27: LineSegment StartX=26.5 StartY=-49.2912 StartZ=0 EndX=26.5 EndY=-44.2912 EndZ=0
    g28: LineSegment StartX=26.5 StartY=-44.2912 StartZ=0 EndX=15.0036 EndY=-44.2912 EndZ=0
    g29: LineSegment StartX=22.0661 StartY=-51.2436 StartZ=0 EndX=25.8788 EndY=-52.4534 EndZ=0
    g30: LineSegment StartX=25.8788 StartY=-52.4534 StartZ=0 EndX=26.5 EndY=-49.2912 EndZ=0
  constraints (81):
    c: Coincident(g0,g1)
    c: Coincident(g1,g2)
    c: Coincident(g2,g3)
    c: Coincident(g3,g0)
    c: Horizontal(g0)
    c: Horizontal(g2)
    c: Vertical(g1)
    c: Vertical(g3)
    c: PointOnObject(g0,g-2)
    c: Distance(g0) = 22.5
    c: Distance(g1) = 4
    c: Coincident(g4,g5)
    c: Coincident(g5,g6)
    c: Coincident(g6,g7)
    c: Coincident(g7,g4)
    c: Horizontal(g4)
    c: Horizontal(g6)
    c: Vertical(g5)
    c: Vertical(g7)
    c: Coincident(g4,g0)
    c: Distance(g7) = 5
    c: Distance(g6) = 4
    c: Coincident(g8,g9)
    c: Coincident(g9,g10)
    c: Coincident(g10,g11)
    c: Coincident(g11,g8)
    c: Horizontal(g8)
    c: Horizontal(g10)
    c: Vertical(g9)
    c: Vertical(g11)
    c: Coincident(g8,g0)
    c: PointOnObject(g9,g-2)
    c: Distance(g9) = 5
    c: Coincident(g12,g9)
    c: Coincident(g12,g0)
    c: Coincident(g13,g0)
    c: Perpendicular(g13,g12)
    c: Distance(g13) = 2
    c: Coincident(g14,g0)
    c: Distance(g14) = 2
    c: Perpendicular(g14,g12)
    c: Coincident(g15,g14)
    c: Coincident(g15,g9)
    c: Coincident(g16,g13)
    c: Coincident(g16,g9)
    c: Coincident(g17,g14)
    c: PointOnObject(g17,g15)
    c: Distance(g17) = 8
    c: Coincident(g18,g17)
    c: PointOnObject(g18,g0)
    c: Perpendicular(g18,g12)
    c: PointOnObject(g19,g10)
    c: Coincident(g19,g17)
    c: Vertical(g19)
    c: Coincident(g20,g13)
    c: PointOnObject(g20,g2)
    c: Vertical(g20)
    c: Coincident(g21,g14)
    c: PointOnObject(g21,g5)
    c: Horizontal(g21)
    c: Coincident(g19,g22)
    c: Coincident(g23,g22)
    c: PointOnObject(g23,g18)
    c: Coincident(g24,g23)
    c: Coincident(g24,g13)
    c: Coincident(g25,g24)
    c: Coincident(g25,g0)
    c: Coincident(g26,g25)
    c: Coincident(g26,g4)
    c: Coincident(g27,g26)
    c: Coincident(g27,g5)
    c: Coincident(g28,g27)
    c: Coincident(g28,g22)
    c: Vertical(g22)
    c: Angle(g15,g10) = 0.132114
    c: Angle(g12,g10) = 0.218669
    c: Angle(g9,g12) = 1.35213
    c: Coincident(g29,g24)
    c: Distance(g29) = 4
    c: Coincident(g30,g29)
    c: Coincident(g30,g26)
FEATURE [Part::Box] Box247  label="Krychle247"
  AttacherType = Attacher::AttachEngine3D
  Height = 40
  Length = 40
  Placement = pos=(-20,98,30) rot=(0,0,1;0rad)
  Width = 20
FEATURE [Part::Box] Box753  label="Krychle753"
  AttacherType = Attacher::AttachEngine3D
  Height = 40
  Length = 40
  Placement = pos=(-20,88,30) rot=(0,0,1;0rad)
  Width = 20
FEATURE [Part::FeaturePython] bevelgear007  # WARN: FeaturePython — macro-defined, semantics opaque (R4)
  AttacherType = Attacher::AttachEngine3D
  Placement = pos=(26,0,-244) rot=(0,-1,0;1.5708rad)
  backlash = 0.1
  beta = 12
  clearance = 0.1
  height = 25
  module = 1.5
  numpoints = 6
  pitch_angle = 12.53
  pressure_angle = 25
  reset_origin = true
  teeth = 8
  version = 0.0.3
FEATURE [PartDesign::Revolution] Revolution007
  Angle = 360
  Axis = (22.5,0,0)
  Base = (0,9.8e-15,-44.2912)
  Placement = pos=(0,0,0) rot=(1,0,0;1.5708rad)
  Profile = -> Sketch007
  ReferenceAxis = -> Sketch007 [Axis10]
  Reversed = true
FEATURE [PartDesign::Body] Body007
  Group = -> [Sketch007,Revolution007]
  Origin = -> Origin007
  Placement = pos=(0,0,-199.6) rot=(0,0,1;0rad)
  Tip = -> Revolution007
FEATURE [Part::Common] Common009
  Base = -> Body007
  Placement = pos=(0,84,294) rot=(0,0,1;1.5708rad)
  Tool = -> bevelgear007
FEATURE [Part::Compound] Compound912  label="bazovina-prevod-C1"
  Links = -> [Common009]
  Placement = pos=(0,-2,0) rot=(0,0,1;0rad)
FEATURE [Part::Box] Box754  label="Krychle754"
  AttacherType = Attacher::AttachEngine3D
  Height = 26
  Length = 2
  Placement = pos=(194.5,-4,4) rot=(0,0,1;0rad)
  Width = 8
FEATURE [Part::Cylinder] Cylinder650  label="Válec650"
  Angle = 360
  AttacherType = Attacher::AttachEngine3D
  Height = 10
  Placement = pos=(0,118,50) rot=(1,0,0;1.5708rad)
  Radius = 4.1
FEATURE [Part::Cylinder] Cylinder651  label="Válec651"
  Angle = 360
  AttacherType = Attacher::AttachEngine3D
  Height = 100
  Placement = pos=(100,0,21) rot=(0.57735,0.57735,0.57735;2.0944rad)
  Radius = 1.5
FEATURE [Part::Box] Box252  label="Krychle252"
  AttacherType = Attacher::AttachEngine3D
  Height = 40
  Length = 40
  Placement = pos=(-20,110,30) rot=(0,0,1;0rad)
  Width = 20
FEATURE [Part::Cylinder] Cylinder649  label="Válec649"
  Angle = 360
  AttacherType = Attacher::AttachEngine3D
  Height = 8
  Placement = pos=(0,114,50) rot=(1,0,0;1.5708rad)
  Radius = 8
FEATURE [Part::Box] Box755  label="Krychle755"
  AttacherType = Attacher::AttachEngine3D
  Height = 6
  Length = 6
  Placement = pos=(196.5,-3,12) rot=(0,0,1;1.5708rad)
  Width = 2
FEATURE [Part::Cylinder] Cylinder652  label="Válec652"
  Angle = 360
  AttacherType = Attacher::AttachEngine3D
  Height = 100
  Placement = pos=(100,0,15) rot=(0.57735,0.57735,0.57735;2.0944rad)
  Radius = 1.5
FEATURE [Part::Compound] Compound028
  Links = -> [Cylinder651,Cylinder652]
  Placement = pos=(0,0,-20) rot=(0,0,1;0rad)
FEATURE [Part::Box] Box756  label="Krychle756"
  AttacherType = Attacher::AttachEngine3D
  Height = 6
  Length = 6
  Placement = pos=(196.5,-3,18) rot=(0,0,1;1.5708rad)
  Width = 2
FEATURE [Part::Compound] Compound027
  Links = -> [Box756,Box755]
  Placement = pos=(0,0,-20) rot=(0,0,1;0rad)
FEATURE [Part::FeaturePython] Tube006  # WARN: FeaturePython — macro-defined, semantics opaque (R4)
  AttacherType = Attacher::AttachEngine3D
  Height = 32
  InnerRadius = 4.1
  OuterRadius = 8.5
  Placement = pos=(200,0,-8) rot=(0,0,1;0rad)
FEATURE [Part::MultiFuse] Fusion002
  Shapes = -> [Tube006,Box754]
FEATURE [Part::Cut] Cut257
  Base = -> Fusion002
  Tool = -> Compound027
FEATURE [Part::Cut] Cut259  label="super_spojka002"
  Base = -> Cut257
  Placement = pos=(-200,132,50) rot=(1,0,0;1.5708rad)
  Tool = -> Compound028
FEATURE [Part::Cut] Cut258
  Base = -> Cut259
  Tool = -> Box753
FEATURE [Part::Cut] Cut550
  Base = -> Cut258
  Placement = pos=(0,-8,0) rot=(0,0,1;0rad)
  Tool = -> Box247
FEATURE [Part::Cut] Cut255
  Base = -> Cylinder649
  Tool = -> Cylinder650
FEATURE [Part::Cut] Cut260
  Base = -> Cut255
  Tool = -> Box252
FEATURE [Part::Cylinder] Cylinder653  label="Válec653"
  Angle = 360
  AttacherType = Attacher::AttachEngine3D
  Height = 8
  Placement = pos=(0,98,50) rot=(1,0,0;1.5708rad)
  Radius = 7
FEATURE [Part::Cut] Cut261
  Base = -> Compound912
  Tool = -> Cylinder653
FEATURE [Part::Compound] Compound029  label="bazovina-prevod-C"
  Links = -> [Cut550,Cut260,Cut261]
  Placement = pos=(0,0,-1) rot=(0,0,1;0rad)
FEATURE [Sketcher::SketchObject] Sketch010
  FullyConstrained = false
  MapMode = 5
  Placement = pos=(0,0,0) rot=(1,0,0;1.5708rad)
  Support = -> [XZ_Plane010]
  sketch-geometry (29):
    g0: LineSegment StartX=0 StartY=-63.0008 StartZ=0 EndX=22.5 EndY=-63.0008 EndZ=0
    g1: LineSegment StartX=22.5 StartY=-63.0008 StartZ=0 EndX=22.5 EndY=-67.0008 EndZ=0
    g2: LineSegment StartX=22.5 StartY=-67.0008 StartZ=0 EndX=0 EndY=-67.0008 EndZ=0
    g3: LineSegment StartX=0 StartY=-67.0008 StartZ=0 EndX=0 EndY=-63.0008 EndZ=0
    g4: LineSegment StartX=22.5 StartY=-63.0008 StartZ=0 EndX=26.5 EndY=-63.0008 EndZ=0
    g5: LineSegment StartX=26.5 StartY=-63.0008 StartZ=0 EndX=26.5 EndY=-58.0008 EndZ=0
    g6: LineSegment StartX=26.5 StartY=-58.0008 StartZ=0 EndX=22.5 EndY=-58.0008 EndZ=0
    g7: LineSegment StartX=22.5 StartY=-58.0008 StartZ=0 EndX=22.5 EndY=-63.0008 EndZ=0
    g8: LineSegment StartX=22.5 StartY=-63.0008 StartZ=0 EndX=0 EndY=-63.0008 EndZ=0
    g9: LineSegment StartX=0 StartY=-63.0008 StartZ=0 EndX=0 EndY=-58.0008 EndZ=0
    g10: LineSegment StartX=0 StartY=-58.0008 StartZ=0 EndX=22.5 EndY=-58.0008 EndZ=0
    g11: LineSegment StartX=22.5 StartY=-58.0008 StartZ=0 EndX=22.5 EndY=-63.0008 EndZ=0
    g12: LineSegment StartX=0 StartY=-58.0008 StartZ=0 EndX=22.5 EndY=-63.0008 EndZ=0
    g13: LineSegment StartX=22.5 StartY=-63.0008 StartZ=0 EndX=22.0661 EndY=-64.9532 EndZ=0
    g14: LineSegment StartX=22.5 StartY=-63.0008 StartZ=0 EndX=22.9339 EndY=-61.0485 EndZ=0
    g15: LineSegment StartX=22.9339 StartY=-61.0485 StartZ=0 EndX=0 EndY=-58.0008 EndZ=0
    g16: LineSegment StartX=22.0661 StartY=-64.9532 StartZ=0 EndX=0 EndY=-58.0008 EndZ=0
    g17: LineSegment StartX=22.9339 StartY=-61.0485 StartZ=0 EndX=15.0036 EndY=-59.9946 EndZ=0
    g18: LineSegment StartX=15.0036 StartY=-59.9946 StartZ=0 EndX=14.3355 EndY=-63.0008 EndZ=0
    g19: LineSegment StartX=15.0036 StartY=-58.0008 StartZ=0 EndX=15.0036 EndY=-59.9946 EndZ=0
    g20: LineSegment StartX=22.0661 StartY=-64.9532 StartZ=0 EndX=22.0661 EndY=-67.0008 EndZ=0
    g21: LineSegment StartX=22.9339 StartY=-61.0485 StartZ=0 EndX=26.5 EndY=-61.0485 EndZ=0
    g22: LineSegment StartX=22.0661 StartY=-67.0008 StartZ=0 EndX=22.0661 EndY=-64.9532 EndZ=0
    g23: LineSegment StartX=22.0661 StartY=-64.9532 StartZ=0 EndX=22.9339 EndY=-61.0485 EndZ=0
    g24: LineSegment StartX=22.9339 StartY=-61.0485 StartZ=0 EndX=15.0036 EndY=-59.9946 EndZ=0
    g25: LineSegment StartX=15.0036 StartY=-59.9946 StartZ=0 EndX=14.3355 EndY=-63.0008 EndZ=0
    g26: LineSegment StartX=14.3355 StartY=-63.0008 StartZ=0 EndX=0 EndY=-63.0008 EndZ=0
    g27: LineSegment StartX=0 StartY=-63.0008 StartZ=0 EndX=0 EndY=-67.0008 EndZ=0
    g28: LineSegment StartX=0 StartY=-67.0008 StartZ=0 EndX=22.0661 EndY=-67.0008 EndZ=0
  constraints (77):
    c: Coincident(g0,g1)
    c: Coincident(g1,g2)
    c: Coincident(g2,g3)
    c: Coincident(g3,g0)
    c: Horizontal(g0)
    c: Horizontal(g2)
    c: Vertical(g1)
    c: Vertical(g3)
    c: PointOnObject(g0,g-2)
    c: Distance(g0) = 22.5
    c: Distance(g1) = 4
    c: Coincident(g4,g5)
    c: Coincident(g5,g6)
    c: Coincident(g6,g7)
    c: Coincident(g7,g4)
    c: Horizontal(g4)
    c: Horizontal(g6)
    c: Vertical(g5)
    c: Vertical(g7)
    c: Coincident(g4,g0)
    c: Distance(g7) = 5
    c: Distance(g6) = 4
    c: Coincident(g8,g9)
    c: Coincident(g9,g10)
    c: Coincident(g10,g11)
    c: Coincident(g11,g8)
    c: Horizontal(g8)
    c: Horizontal(g10)
    c: Vertical(g9)
    c: Vertical(g11)
    c: Coincident(g8,g0)
    c: PointOnObject(g9,g-2)
    c: Distance(g9) = 5
    c: Coincident(g12,g9)
    c: Coincident(g12,g0)
    c: Coincident(g13,g0)
    c: Perpendicular(g13,g12)
    c: Distance(g13) = 2
    c: Coincident(g14,g0)
    c: Distance(g14) = 2
    c: Perpendicular(g14,g12)
    c: Coincident(g15,g14)
    c: Coincident(g15,g9)
    c: Coincident(g16,g13)
    c: Coincident(g16,g9)
    c: Coincident(g17,g14)
    c: PointOnObject(g17,g15)
    c: Distance(g17) = 8
    c: Coincident(g18,g17)
    c: PointOnObject(g18,g0)
    c: Perpendicular(g18,g12)
    c: PointOnObject(g19,g10)
    c: Coincident(g19,g17)
    c: Vertical(g19)
    c: Coincident(g20,g13)
    c: PointOnObject(g20,g2)
    c: Vertical(g20)
    c: Coincident(g21,g14)
    c: PointOnObject(g21,g5)
    c: Horizontal(g21)
    c: Angle(g15,g10) = 0.132114
    c: Angle(g12,g10) = 0.218669
    c: Angle(g9,g12) = 1.35213
    c: Coincident(g22,g20)
    c: Coincident(g22,g13)
    c: Coincident(g22,g23)
    c: Coincident(g23,g14)
    c: Coincident(g23,g24)
    c: Coincident(g24,g17)
    c: Coincident(g24,g25)
    c: Coincident(g25,g18)
    c: Coincident(g26,g25)
    c: Coincident(g26,g0)
    c: Coincident(g27,g26)
    c: Coincident(g27,g2)
    c: Coincident(g28,g27)
    c: Coincident(g28,g22)
FEATURE [Part::Cylinder] Cylinder571  label="Válec571"
  Angle = 360
  AttacherType = Attacher::AttachEngine3D
  Height = 30
  Placement = pos=(0,83,232) rot=(0,0,1;0rad)
  Radius = 2.65
FEATURE [Part::Cylinder] Cylinder572  label="Válec572"
  Angle = 360
  AttacherType = Attacher::AttachEngine3D
  Height = 30
  Placement = pos=(0,94,232) rot=(0,0,1;0rad)
  Radius = 1.5
FEATURE [Part::Cylinder] Cylinder575  label="Válec575"
  Angle = 360
  AttacherType = Attacher::AttachEngine3D
  Height = 30
  Placement = pos=(-11,83,232) rot=(0,0,1;0rad)
  Radius = 1.5
FEATURE [Part::FeaturePython] bevelgear010  # WARN: FeaturePython — macro-defined, semantics opaque (R4)
  AttacherType = Attacher::AttachEngine3D
  Placement = pos=(0,0,-256) rot=(1,0,0;3.14159rad)
  backlash = 0
  beta = 12
  clearance = 0.1
  height = 16
  module = 0.11
  numpoints = 6
  pitch_angle = 77.47
  pressure_angle = 21
  reset_origin = true
  teeth = 36
  version = 0.0.3
FEATURE [PartDesign::Revolution] Revolution010
  Angle = 360
  Axis = (0,-9e-16,4)
  Base = (0,1.49e-14,-67.0008)
  Placement = pos=(0,0,0) rot=(1,0,0;1.5708rad)
  Profile = -> Sketch010
  ReferenceAxis = -> Sketch010 [Axis3]
  Reversed = true
FEATURE [PartDesign::Body] Body010
  Group = -> [Sketch010,Revolution010]
  Origin = -> Origin010
  Placement = pos=(0,0,-199.6) rot=(0,0,1;0rad)
  Tip = -> Revolution010
FEATURE [Part::Common] Common012
  Base = -> Body010
  Placement = pos=(0,83,507) rot=(0,0,1;0.087266rad)
  Tool = -> bevelgear010
FEATURE [Part::Cylinder] Cylinder580  label="Válec580"
  Angle = 360
  AttacherType = Attacher::AttachEngine3D
  Height = 30
  Placement = pos=(11,83,232) rot=(0,0,1;0rad)
  Radius = 1.5
FEATURE [Part::Cylinder] Cylinder570  label="Válec570"
  Angle = 360
  AttacherType = Attacher::AttachEngine3D
  Height = 30
  Placement = pos=(11,83,232) rot=(0,0,1;0rad)
  Radius = 1.5
FEATURE [Part::Cylinder] Cylinder579  label="Válec579"
  Angle = 360
  AttacherType = Attacher::AttachEngine3D
  Height = 6
  Placement = pos=(0,83,236) rot=(0,0,1;0rad)
  Radius = 30
FEATURE [Part::Cut] Cut224
  Base = -> Common012
  Tool = -> Cylinder579
FEATURE [Part::Cylinder] Cylinder574  label="Válec574"
  Angle = 360
  AttacherType = Attacher::AttachEngine3D
  Height = 30
  Placement = pos=(0,72,232) rot=(0,0,1;0rad)
  Radius = 1.5
FEATURE [Part::Compound] Compound360
  Links = -> [Cylinder575,Cylinder570,Cylinder574,Cylinder572]
FEATURE [Part::Cut] Cut225
  Base = -> Cut224
  Tool = -> Compound360
FEATURE [Part::Cut] Cut222
  Base = -> Cut225
  Tool = -> Cylinder571
FEATURE [Part::Cylinder] Cylinder586  label="Válec586"
  Angle = 360
  AttacherType = Attacher::AttachEngine3D
  Height = 30
  Placement = pos=(0,83,232) rot=(0,0,1;0rad)
  Radius = 2.65
FEATURE [Part::Cylinder] Cylinder582  label="Válec582"
  Angle = 360
  AttacherType = Attacher::AttachEngine3D
  Height = 3
  Placement = pos=(0,94,232) rot=(0,0,1;0rad)
  Radius = 3
FEATURE [Part::Cylinder] Cylinder585  label="Válec585"
  Angle = 360
  AttacherType = Attacher::AttachEngine3D
  Height = 30
  Placement = pos=(-11,83,232) rot=(0,0,1;0rad)
  Radius = 1.5
FEATURE [Part::Cylinder] Cylinder581  label="Válec581"
  Angle = 360
  AttacherType = Attacher::AttachEngine3D
  Height = 40
  Placement = pos=(0,83,232) rot=(0,0,1;0rad)
  Radius = 2.65
FEATURE [Part::Cylinder] Cylinder578  label="Válec578"
  Angle = 360
  AttacherType = Attacher::AttachEngine3D
  Height = 3
  Placement = pos=(-11,83,232) rot=(0,0,1;0rad)
  Radius = 3
FEATURE [Part::Cylinder] Cylinder577  label="Válec577"
  Angle = 360
  AttacherType = Attacher::AttachEngine3D
  Height = 17
  Placement = pos=(0,83,252) rot=(0,0,1;0rad)
  Radius = 8
FEATURE [Part::Cut] Cut220
  Base = -> Cylinder577
  Tool = -> Cylinder581
FEATURE [Part::Cylinder] Cylinder583  label="Válec583"
  Angle = 360
  AttacherType = Attacher::AttachEngine3D
  Height = 30
  Placement = pos=(0,94,232) rot=(0,0,1;0rad)
  Radius = 1.5
FEATURE [Part::Cylinder] Cylinder576  label="Válec576"
  Angle = 360
  AttacherType = Attacher::AttachEngine3D
  Height = 3
  Placement = pos=(11,83,232) rot=(0,0,1;0rad)
  Radius = 3
FEATURE [Part::Cylinder] Cylinder569  label="Válec569"
  Angle = 360
  AttacherType = Attacher::AttachEngine3D
  Height = 10
  Placement = pos=(0,83,242) rot=(0,0,1;0rad)
  Radius = 15.1
FEATURE [Part::Cylinder] Cylinder573  label="Válec573"
  Angle = 360
  AttacherType = Attacher::AttachEngine3D
  Height = 3
  Placement = pos=(0,72,232) rot=(0,0,1;0rad)
  Radius = 3
FEATURE [Part::Compound] Compound359
  Links = -> [Cylinder578,Cylinder576,Cylinder573,Cylinder582]
  Placement = pos=(0,0,17) rot=(0,0,1;0rad)
FEATURE [Part::Cylinder] Cylinder584  label="Válec584"
  Angle = 360
  AttacherType = Attacher::AttachEngine3D
  Height = 30
  Placement = pos=(0,72,232) rot=(0,0,1;0rad)
  Radius = 1.5
FEATURE [Part::Compound] Compound358
  Links = -> [Cylinder585,Cylinder580,Cylinder584,Cylinder583]
FEATURE [Part::Cut] Cut221
  Base = -> Cylinder569
  Tool = -> Compound358
FEATURE [Part::Cut] Cut223
  Base = -> Cut221
  Tool = -> Compound359
FEATURE [Part::Cut] Cut226
  Base = -> Cut223
  Tool = -> Cylinder586
FEATURE [Part::Compound] Compound357  label="bazovina-prevod-A"
  Links = -> [Cut222,Cut226,Cut220]
  Placement = pos=(0,0,-203) rot=(0,0,1;0rad)
FEATURE [Part::Cylinder] Cylinder1810  label="Válec1810"
  Angle = 360
  AttacherType = Attacher::AttachEngine3D
  Height = 30
  Placement = pos=(-11,83,15) rot=(0,0,1;0rad)
  Radius = 1.5
FEATURE [Part::FeaturePython] wormgear026  # WARN: FeaturePython — macro-defined, semantics opaque (R4)
  AttacherType = Attacher::AttachEngine3D
  Placement = pos=(0,83,37) rot=(0,0,1;0.191986rad)
  beta = 33.1113
  clearance = 0.25
  diameter = 46
  head = 0
  height = 5
  module = 1
  pressure_angle = 20
  reverse_pitch = true
  teeth = 30
  version = 0.0.3
FEATURE [Part::FeaturePython] wormgear027  # WARN: FeaturePython — macro-defined, semantics opaque (R4)
  AttacherType = Attacher::AttachEngine3D
  Placement = pos=(0,83,32) rot=(0,0,1;0.069813rad)
  beta = 33.1113
  clearance = 0.25
  diameter = 46
  head = 0
  height = 5
  module = 1
  pressure_angle = 20
  reverse_pitch = false
  teeth = 30
  version = 0.0.3
FEATURE [Part::Box] Box001  label="Krychle001"
  AttacherType = Attacher::AttachEngine3D
  Height = 20
  Length = 6
  Placement = pos=(-14,80,38) rot=(0,0,1;0rad)
  Width = 6
FEATURE [Part::Cylinder] Cylinder593  label="Válec593"
  Angle = 360
  AttacherType = Attacher::AttachEngine3D
  Height = 30
  Placement = pos=(11,83,15) rot=(0,0,1;0rad)
  Radius = 1.5
FEATURE [Part::Cylinder] Cylinder591  label="Válec591"
  Angle = 360
  AttacherType = Attacher::AttachEngine3D
  Height = 40
  Placement = pos=(0,83,15) rot=(0,0,1;0rad)
  Radius = 2.65
FEATURE [Part::Cylinder] Cylinder590  label="Válec590"
  Angle = 360
  AttacherType = Attacher::AttachEngine3D
  Height = 30
  Placement = pos=(0,94,15) rot=(0,0,1;0rad)
  Radius = 1.5
FEATURE [Part::Cylinder] Cylinder588  label="Válec588"
  Angle = 360
  AttacherType = Attacher::AttachEngine3D
  Height = 30
  Placement = pos=(11,83,15) rot=(0,0,1;0rad)
  Radius = 1.5
FEATURE [Part::Cylinder] Cylinder592  label="Válec592"
  Angle = 360
  AttacherType = Attacher::AttachEngine3D
  Height = 30
  Placement = pos=(-11,83,15) rot=(0,0,1;0rad)
  Radius = 1.5
FEATURE [Part::Cylinder] Cylinder596  label="Válec596"
  Angle = 360
  AttacherType = Attacher::AttachEngine3D
  Height = 40
  Placement = pos=(0,83,15) rot=(0,0,1;0rad)
  Radius = 2.65
FEATURE [Part::Box] Box757  label="Krychle757"
  AttacherType = Attacher::AttachEngine3D
  Height = 20
  Length = 6
  Placement = pos=(8,80,38) rot=(0,0,1;0rad)
  Width = 6
FEATURE [Part::Cylinder] Cylinder594  label="Válec594"
  Angle = 360
  AttacherType = Attacher::AttachEngine3D
  Height = 30
  Placement = pos=(0,72,15) rot=(0,0,1;0rad)
  Radius = 1.5
FEATURE [Part::Box] Box003  label="Krychle003"
  AttacherType = Attacher::AttachEngine3D
  Height = 20
  Length = 6
  Placement = pos=(-3,91,38) rot=(0,0,1;0rad)
  Width = 6
FEATURE [Part::Cylinder] Cylinder595  label="Válec595"
  Angle = 360
  AttacherType = Attacher::AttachEngine3D
  Height = 30
  Placement = pos=(0,94,15) rot=(0,0,1;0rad)
  Radius = 1.5
FEATURE [Part::Compound] Compound913
  Links = -> [Cylinder592,Cylinder593,Cylinder594,Cylinder595]
FEATURE [Part::Cylinder] Cylinder589  label="Válec589"
  Angle = 360
  AttacherType = Attacher::AttachEngine3D
  Height = 30
  Placement = pos=(0,72,15) rot=(0,0,1;0rad)
  Radius = 1.5
FEATURE [Part::Compound] Compound361
  Links = -> [Cylinder1810,Cylinder588,Cylinder589,Cylinder590]
FEATURE [Part::Box] Box002  label="Krychle002"
  AttacherType = Attacher::AttachEngine3D
  Height = 20
  Length = 6
  Placement = pos=(-3,69,38) rot=(0,0,1;0rad)
  Width = 6
FEATURE [Part::Compound] Compound362
  Links = -> [Box757,Box001,Box002,Box003]
FEATURE [Part::Cut] Cut551
  Base = -> wormgear026
  Tool = -> Compound361
FEATURE [Part::Cut] Cut227
  Base = -> wormgear027
  Tool = -> Compound913
FEATURE [Part::Cut] Cut229
  Base = -> Cut227
  Tool = -> Cylinder591
FEATURE [Part::Cut] Cut228
  Base = -> Cut551
  Tool = -> Cylinder596
FEATURE [Part::Cut] Cut230
  Base = -> Cut228
  Tool = -> Compound362
FEATURE [Part::Compound] Compound363  label="bazovina-prevod-B"
  Links = -> [Cut229,Cut230]
  Placement = pos=(0,0,-2) rot=(0,0,1;0rad)
FEATURE [Sketcher::SketchObject] Sketch011
  FullyConstrained = false
  MapMode = 5
  Placement = pos=(0,0,0) rot=(1,0,0;1.5708rad)
  Support = -> [XZ_Plane013]
  sketch-geometry (29):
    g0: LineSegment StartX=0 StartY=-49.6356 StartZ=0 EndX=22.5 EndY=-49.6356 EndZ=0
    g1: LineSegment StartX=22.5 StartY=-49.6356 StartZ=0 EndX=22.5 EndY=-53.6356 EndZ=0
    g2: LineSegment StartX=22.5 StartY=-53.6356 StartZ=0 EndX=0 EndY=-53.6356 EndZ=0
    g3: LineSegment StartX=0 StartY=-53.6356 StartZ=0 EndX=0 EndY=-49.6356 EndZ=0
    g4: LineSegment StartX=22.5 StartY=-49.6356 StartZ=0 EndX=26.5 EndY=-49.6356 EndZ=0
    g5: LineSegment StartX=26.5 StartY=-49.6356 StartZ=0 EndX=26.5 EndY=-42.6356 EndZ=0
    g6: LineSegment StartX=26.5 StartY=-42.6356 StartZ=0 EndX=22.5 EndY=-42.6356 EndZ=0
    g7: LineSegment StartX=22.5 StartY=-42.6356 StartZ=0 EndX=22.5 EndY=-49.6356 EndZ=0
    g8: LineSegment StartX=22.5 StartY=-49.6356 StartZ=0 EndX=0 EndY=-49.6356 EndZ=0
    g9: LineSegment StartX=0 StartY=-49.6356 StartZ=0 EndX=0 EndY=-42.6356 EndZ=0
    g10: LineSegment StartX=0 StartY=-42.6356 StartZ=0 EndX=22.5 EndY=-42.6356 EndZ=0
    g11: LineSegment StartX=22.5 StartY=-42.6356 StartZ=0 EndX=22.5 EndY=-49.6356 EndZ=0
    g12: LineSegment StartX=0 StartY=-42.6356 StartZ=0 EndX=22.5 EndY=-49.6356 EndZ=0
    g13: LineSegment StartX=22.5 StartY=-49.6356 StartZ=0 EndX=21.9059 EndY=-51.5453 EndZ=0
    g14: LineSegment StartX=22.5 StartY=-49.6356 StartZ=0 EndX=23.0941 EndY=-47.7259 EndZ=0
    g15: LineSegment StartX=23.0941 StartY=-47.7259 StartZ=0 EndX=0 EndY=-42.6356 EndZ=0
    g16: LineSegment StartX=21.9059 StartY=-51.5453 StartZ=0 EndX=0 EndY=-42.6356 EndZ=0
    g17: LineSegment StartX=23.0941 StartY=-47.7259 StartZ=0 EndX=15.2817 EndY=-46.0039 EndZ=0
    g18: LineSegment StartX=15.2817 StartY=-46.0039 StartZ=0 EndX=14.1518 EndY=-49.6356 EndZ=0
    g19: LineSegment StartX=15.2817 StartY=-42.6356 StartZ=0 EndX=15.2817 EndY=-46.0039 EndZ=0
    g20: LineSegment StartX=21.9059 StartY=-51.5453 StartZ=0 EndX=21.9059 EndY=-53.6356 EndZ=0
    g21: LineSegment StartX=23.0941 StartY=-47.7259 StartZ=0 EndX=26.5 EndY=-47.7259 EndZ=0
    g22: LineSegment StartX=15.2817 StartY=-42.6356 StartZ=0 EndX=15.2817 EndY=-46.5709 EndZ=0
    g23: LineSegment StartX=15.2817 StartY=-46.5709 StartZ=0 EndX=14.4998 EndY=-48.5171 EndZ=0
    g24: LineSegment StartX=14.4998 StartY=-48.5171 StartZ=0 EndX=21.9059 EndY=-51.5453 EndZ=0
    g25: LineSegment StartX=26.275 StartY=-49.2912 StartZ=0 EndX=26.5 EndY=-42.6356 EndZ=0
    g26: LineSegment StartX=26.5 StartY=-42.6356 StartZ=0 EndX=15.2817 EndY=-42.6356 EndZ=0
    g27: LineSegment StartX=26.275 StartY=-49.2912 StartZ=0 EndX=26.275 EndY=-53.3318 EndZ=0
    g28: LineSegment StartX=21.9059 StartY=-51.5453 StartZ=0 EndX=26.275 EndY=-53.3318 EndZ=0
  constraints (77):
    c: Coincident(g0,g1)
    c: Coincident(g1,g2)
    c: Coincident(g2,g3)
    c: Coincident(g3,g0)
    c: Horizontal(g0)
    c: Horizontal(g2)
    c: Vertical(g1)
    c: Vertical(g3)
    c: PointOnObject(g0,g-2)
    c: Distance(g0) = 22.5
    c: Distance(g1) = 4
    c: Coincident(g4,g5)
    c: Coincident(g5,g6)
    c: Coincident(g6,g7)
    c: Coincident(g7,g4)
    c: Horizontal(g4)
    c: Horizontal(g6)
    c: Vertical(g5)
    c: Vertical(g7)
    c: Coincident(g4,g0)
    c: Distance(g7) = 7
    c: Distance(g6) = 4
    c: Coincident(g8,g9)
    c: Coincident(g9,g10)
    c: Coincident(g10,g11)
    c: Coincident(g11,g8)
    c: Horizontal(g8)
    c: Horizontal(g10)
    c: Vertical(g9)
    c: Vertical(g11)
    c: Coincident(g8,g0)
    c: PointOnObject(g9,g-2)
    c: Distance(g9) = 7
    c: Coincident(g12,g9)
    c: Coincident(g12,g0)
    c: Coincident(g13,g0)
    c: Perpendicular(g13,g12)
    c: Distance(g13) = 2
    c: Coincident(g14,g0)
    c: Distance(g14) = 2
    c: Perpendicular(g14,g12)
    c: Coincident(g15,g14)
    c: Coincident(g15,g9)
    c: Coincident(g16,g13)
    c: Coincident(g16,g9)
    c: Coincident(g17,g14)
    c: PointOnObject(g17,g15)
    c: Distance(g17) = 8
    c: Coincident(g18,g17)
    c: PointOnObject(g18,g0)
    c: Perpendicular(g18,g12)
    c: PointOnObject(g19,g10)
    c: Coincident(g19,g17)
    c: Vertical(g19)
    c: Coincident(g20,g13)
    c: PointOnObject(g20,g2)
    c: Vertical(g20)
    c: Coincident(g21,g14)
    c: PointOnObject(g21,g5)
    c: Horizontal(g21)
    c: Coincident(g19,g22)
    c: Coincident(g23,g22)
    c: PointOnObject(g23,g18)
    c: Coincident(g24,g23)
    c: Coincident(g24,g13)
    c: Coincident(g25,g5)
    c: Coincident(g26,g25)
    c: Coincident(g26,g22)
    c: Vertical(g22)
    c: Angle(g15,g10) = 0.216946
    c: Angle(g12,g10) = 0.301619
    c: Angle(g9,g12) = 1.26918
    c: Coincident(g27,g25)
    c: Vertical(g27)
    c: Coincident(g28,g24)
    c: Coincident(g28,g27)
    c: Parallel(g24,g28)
FEATURE [PartDesign::Revolution] Revolution011
  Angle = 360
  Axis = (22.5,0,0)
  Base = (0,9.5e-15,-42.6356)
  Placement = pos=(0,0,0) rot=(1,0,0;1.5708rad)
  Profile = -> Sketch011
  ReferenceAxis = -> Sketch011 [Axis10]
  Reversed = true
FEATURE [PartDesign::Body] Body009
  Group = -> [Revolution011,Sketch011]
  Origin = -> Origin009
  Placement = pos=(-1.4,0,-201.4) rot=(0,0,1;0rad)
  Tip = -> Revolution011
FEATURE [Sketcher::SketchObject] Sketch012
  FullyConstrained = false
  MapMode = 5
  Placement = pos=(0,0,0) rot=(1,0,0;1.5708rad)
  Support = -> [XZ_Plane012]
  sketch-geometry (29):
    g0: LineSegment StartX=0 StartY=-49.6356 StartZ=0 EndX=22.5 EndY=-49.6356 EndZ=0
    g1: LineSegment StartX=22.5 StartY=-49.6356 StartZ=0 EndX=22.5 EndY=-53.6356 EndZ=0
    g2: LineSegment StartX=22.5 StartY=-53.6356 StartZ=0 EndX=0 EndY=-53.6356 EndZ=0
    g3: LineSegment StartX=0 StartY=-53.6356 StartZ=0 EndX=0 EndY=-49.6356 EndZ=0
    g4: LineSegment StartX=22.5 StartY=-49.6356 StartZ=0 EndX=26.5 EndY=-49.6356 EndZ=0
    g5: LineSegment StartX=26.5 StartY=-49.6356 StartZ=0 EndX=26.5 EndY=-42.6356 EndZ=0
    g6: LineSegment StartX=26.5 StartY=-42.6356 StartZ=0 EndX=22.5 EndY=-42.6356 EndZ=0
    g7: LineSegment StartX=22.5 StartY=-42.6356 StartZ=0 EndX=22.5 EndY=-49.6356 EndZ=0
    g8: LineSegment StartX=22.5 StartY=-49.6356 StartZ=0 EndX=0 EndY=-49.6356 EndZ=0
    g9: LineSegment StartX=0 StartY=-49.6356 StartZ=0 EndX=0 EndY=-42.6356 EndZ=0
    g10: LineSegment StartX=0 StartY=-42.6356 StartZ=0 EndX=22.5 EndY=-42.6356 EndZ=0
    g11: LineSegment StartX=22.5 StartY=-42.6356 StartZ=0 EndX=22.5 EndY=-49.6356 EndZ=0
    g12: LineSegment StartX=0 StartY=-42.6356 StartZ=0 EndX=22.5 EndY=-49.6356 EndZ=0
    g13: LineSegment StartX=22.5 StartY=-49.6356 StartZ=0 EndX=21.9059 EndY=-51.5453 EndZ=0
    g14: LineSegment StartX=22.5 StartY=-49.6356 StartZ=0 EndX=23.0941 EndY=-47.7259 EndZ=0
    g15: LineSegment StartX=23.0941 StartY=-47.7259 StartZ=0 EndX=0 EndY=-42.6356 EndZ=0
    g16: LineSegment StartX=21.9059 StartY=-51.5453 StartZ=0 EndX=0 EndY=-42.6356 EndZ=0
    g17: LineSegment StartX=23.0941 StartY=-47.7259 StartZ=0 EndX=15.2817 EndY=-46.0039 EndZ=0
    g18: LineSegment StartX=15.2817 StartY=-46.0039 StartZ=0 EndX=14.1518 EndY=-49.6356 EndZ=0
    g19: LineSegment StartX=15.2817 StartY=-42.6356 StartZ=0 EndX=15.2817 EndY=-46.0039 EndZ=0
    g20: LineSegment StartX=21.9059 StartY=-51.5453 StartZ=0 EndX=21.9059 EndY=-53.6356 EndZ=0
    g21: LineSegment StartX=23.0941 StartY=-47.7259 StartZ=0 EndX=26.5 EndY=-47.7259 EndZ=0
    g22: LineSegment StartX=15.2817 StartY=-42.6356 StartZ=0 EndX=15.2817 EndY=-46.5709 EndZ=0
    g23: LineSegment StartX=15.2817 StartY=-46.5709 StartZ=0 EndX=14.4998 EndY=-48.5171 EndZ=0
    g24: LineSegment StartX=14.4998 StartY=-48.5171 StartZ=0 EndX=21.9059 EndY=-51.5453 EndZ=0
    g25: LineSegment StartX=26.275 StartY=-49.2912 StartZ=0 EndX=26.5 EndY=-42.6356 EndZ=0
    g26: LineSegment StartX=26.5 StartY=-42.6356 StartZ=0 EndX=15.2817 EndY=-42.6356 EndZ=0
    g27: LineSegment StartX=26.275 StartY=-49.2912 StartZ=0 EndX=26.275 EndY=-53.3318 EndZ=0
    g28: LineSegment StartX=21.9059 StartY=-51.5453 StartZ=0 EndX=26.275 EndY=-53.3318 EndZ=0
  constraints (77):
    c: Coincident(g0,g1)
    c: Coincident(g1,g2)
    c: Coincident(g2,g3)
    c: Coincident(g3,g0)
    c: Horizontal(g0)
    c: Horizontal(g2)
    c: Vertical(g1)
    c: Vertical(g3)
    c: PointOnObject(g0,g-2)
    c: Distance(g0) = 22.5
    c: Distance(g1) = 4
    c: Coincident(g4,g5)
    c: Coincident(g5,g6)
    c: Coincident(g6,g7)
    c: Coincident(g7,g4)
    c: Horizontal(g4)
    c: Horizontal(g6)
    c: Vertical(g5)
    c: Vertical(g7)
    c: Coincident(g4,g0)
    c: Distance(g7) = 7
    c: Distance(g6) = 4
    c: Coincident(g8,g9)
    c: Coincident(g9,g10)
    c: Coincident(g10,g11)
    c: Coincident(g11,g8)
    c: Horizontal(g8)
    c: Horizontal(g10)
    c: Vertical(g9)
    c: Vertical(g11)
    c: Coincident(g8,g0)
    c: PointOnObject(g9,g-2)
    c: Distance(g9) = 7
    c: Coincident(g12,g9)
    c: Coincident(g12,g0)
    c: Coincident(g13,g0)
    c: Perpendicular(g13,g12)
    c: Distance(g13) = 2
    c: Coincident(g14,g0)
    c: Distance(g14) = 2
    c: Perpendicular(g14,g12)
    c: Coincident(g15,g14)
    c: Coincident(g15,g9)
    c: Coincident(g16,g13)
    c: Coincident(g16,g9)
    c: Coincident(g17,g14)
    c: PointOnObject(g17,g15)
    c: Distance(g17) = 8
    c: Coincident(g18,g17)
    c: PointOnObject(g18,g0)
    c: Perpendicular(g18,g12)
    c: PointOnObject(g19,g10)
    c: Coincident(g19,g17)
    c: Vertical(g19)
    c: Coincident(g20,g13)
    c: PointOnObject(g20,g2)
    c: Vertical(g20)
    c: Coincident(g21,g14)
    c: PointOnObject(g21,g5)
    c: Horizontal(g21)
    c: Coincident(g19,g22)
    c: Coincident(g23,g22)
    c: PointOnObject(g23,g18)
    c: Coincident(g24,g23)
    c: Coincident(g24,g13)
    c: Coincident(g25,g5)
    c: Coincident(g26,g25)
    c: Coincident(g26,g22)
    c: Vertical(g22)
    c: Angle(g15,g10) = 0.216946
    c: Angle(g12,g10) = 0.301619
    c: Angle(g9,g12) = 1.26918
    c: Coincident(g27,g25)
    c: Vertical(g27)
    c: Coincident(g28,g24)
    c: Coincident(g28,g27)
    c: Parallel(g24,g28)
FEATURE [PartDesign::Revolution] Revolution012
  Angle = 360
  Axis = (22.5,0,0)
  Base = (0,9.5e-15,-42.6356)
  Placement = pos=(0,0,0) rot=(1,0,0;1.5708rad)
  Profile = -> Sketch012
  ReferenceAxis = -> Sketch012 [Axis10]
  Reversed = true
FEATURE [PartDesign::Body] Body011
  Group = -> [Revolution012,Sketch012]
  Origin = -> Origin011
  Placement = pos=(-12.5,0,-201.4) rot=(0,0,1;0rad)
  Tip = -> Revolution012
FEATURE [Part::Cylinder] Cylinder654  label="Válec654"
  Angle = 360
  AttacherType = Attacher::AttachEngine3D
  Height = 100
  Placement = pos=(100,0,21) rot=(0.57735,0.57735,0.57735;2.0944rad)
  Radius = 1.5
FEATURE [Part::Box] Box253  label="Krychle253"
  AttacherType = Attacher::AttachEngine3D
  Height = 24
  Length = 2
  Placement = pos=(194.5,-4,4) rot=(0,0,1;0rad)
  Width = 8
FEATURE [Part::FeaturePython] Tube007  # WARN: FeaturePython — macro-defined, semantics opaque (R4)
  AttacherType = Attacher::AttachEngine3D
  Height = 32
  InnerRadius = 4.1
  OuterRadius = 8.5
  Placement = pos=(200,0,-8) rot=(0,0,1;0rad)
FEATURE [Part::FeaturePython] bevelgear008  # WARN: FeaturePython — macro-defined, semantics opaque (R4)
  AttacherType = Attacher::AttachEngine3D
  Placement = pos=(26,0,-244) rot=(0,-1,0;1.5708rad)
  backlash = 0.1
  beta = 12
  clearance = 0.1
  height = 30
  module = 2
  numpoints = 6
  pitch_angle = 17.29
  pressure_angle = 25
  reset_origin = true
  teeth = 9
  version = 0.0.3
FEATURE [Part::Common] Common
  Base = -> bevelgear008
  Tool = -> Body009
FEATURE [Part::Cut] Cut262
  Base = -> Common
  Placement = pos=(0,81,294) rot=(0,0,1;1.5708rad)
  Tool = -> Body011
FEATURE [Part::MultiFuse] Fusion003
  Shapes = -> [Tube007,Box253]
FEATURE [Part::Box] Box254  label="Krychle254"
  AttacherType = Attacher::AttachEngine3D
  Height = 6
  Length = 6
  Placement = pos=(196.5,-3,12) rot=(0,0,1;1.5708rad)
  Width = 2
FEATURE [Part::Cylinder] Cylinder656  label="Válec656"
  Angle = 360
  AttacherType = Attacher::AttachEngine3D
  Height = 10
  Placement = pos=(0,118,50) rot=(1,0,0;1.5708rad)
  Radius = 4.1
FEATURE [Part::Box] Box256  label="Krychle256"
  AttacherType = Attacher::AttachEngine3D
  Height = 40
  Length = 40
  Placement = pos=(-20,110,30) rot=(0,0,1;0rad)
  Width = 20
FEATURE [Part::Cylinder] Cylinder655  label="Válec655"
  Angle = 360
  AttacherType = Attacher::AttachEngine3D
  Height = 100
  Placement = pos=(100,0,15) rot=(0.57735,0.57735,0.57735;2.0944rad)
  Radius = 1.5
FEATURE [Part::Compound] Compound031
  Links = -> [Cylinder654,Cylinder655]
  Placement = pos=(0,0,-20) rot=(0,0,1;0rad)
FEATURE [Part::Cylinder] Cylinder657  label="Válec657"
  Angle = 360
  AttacherType = Attacher::AttachEngine3D
  Height = 4
  Placement = pos=(0,110,50) rot=(1,0,0;1.5708rad)
  Radius = 11
FEATURE [Part::Cut] Cut265
  Base = -> Cylinder657
  Tool = -> Cylinder656
FEATURE [Part::Cut] Cut552
  Base = -> Cut265
  Tool = -> Box256
FEATURE [Part::Chamfer] Chamfer061
  Base = -> Cut552
  Edges = 1 edges r=2.5: [Edge3]
FEATURE [Part::Box] Box255  label="Krychle255"
  AttacherType = Attacher::AttachEngine3D
  Height = 6
  Length = 6
  Placement = pos=(196.5,-3,18) rot=(0,0,1;1.5708rad)
  Width = 2
FEATURE [Part::Compound] Compound030
  Links = -> [Box255,Box254]
  Placement = pos=(0,0,-20) rot=(0,0,1;0rad)
FEATURE [Part::Cut] Cut263
  Base = -> Fusion003
  Tool = -> Compound030
FEATURE [Part::Cut] Cut264  label="super_spojka003"
  Base = -> Cut263
  Placement = pos=(-200,134,50) rot=(1,0,0;1.5708rad)
  Tool = -> Compound031
FEATURE [Part::Compound] Compound032  label="Base_rear-gear-small-old"
  Links = -> [Cut262,Cut264,Chamfer061]
  Placement = pos=(0,0,2) rot=(0,0,1;0rad)
FEATURE [Sketcher::SketchObject] Sketch013
  FullyConstrained = false
  MapMode = 5
  Placement = pos=(0,0,0) rot=(1,0,0;1.5708rad)
  Support = -> [XZ_Plane014]
  sketch-geometry (29):
    g0: LineSegment StartX=0 StartY=-49.6356 StartZ=0 EndX=22.5 EndY=-49.6356 EndZ=0
    g1: LineSegment StartX=22.5 StartY=-49.6356 StartZ=0 EndX=22.5 EndY=-53.6356 EndZ=0
    g2: LineSegment StartX=22.5 StartY=-53.6356 StartZ=0 EndX=0 EndY=-53.6356 EndZ=0
    g3: LineSegment StartX=0 StartY=-53.6356 StartZ=0 EndX=0 EndY=-49.6356 EndZ=0
    g4: LineSegment StartX=22.5 StartY=-49.6356 StartZ=0 EndX=26.5 EndY=-49.6356 EndZ=0
    g5: LineSegment StartX=26.5 StartY=-49.6356 StartZ=0 EndX=26.5 EndY=-42.6356 EndZ=0
    g6: LineSegment StartX=26.5 StartY=-42.6356 StartZ=0 EndX=22.5 EndY=-42.6356 EndZ=0
    g7: LineSegment StartX=22.5 StartY=-42.6356 StartZ=0 EndX=22.5 EndY=-49.6356 EndZ=0
    g8: LineSegment StartX=22.5 StartY=-49.6356 StartZ=0 EndX=0 EndY=-49.6356 EndZ=0
    g9: LineSegment StartX=0 StartY=-49.6356 StartZ=0 EndX=0 EndY=-42.6356 EndZ=0
    g10: LineSegment StartX=0 StartY=-42.6356 StartZ=0 EndX=22.5 EndY=-42.6356 EndZ=0
    g11: LineSegment StartX=22.5 StartY=-42.6356 StartZ=0 EndX=22.5 EndY=-49.6356 EndZ=0
    g12: LineSegment StartX=0 StartY=-42.6356 StartZ=0 EndX=22.5 EndY=-49.6356 EndZ=0
    g13: LineSegment StartX=22.5 StartY=-49.6356 StartZ=0 EndX=21.9059 EndY=-51.5453 EndZ=0
    g14: LineSegment StartX=22.5 StartY=-49.6356 StartZ=0 EndX=23.0941 EndY=-47.7259 EndZ=0
    g15: LineSegment StartX=23.0941 StartY=-47.7259 StartZ=0 EndX=0 EndY=-42.6356 EndZ=0
    g16: LineSegment StartX=21.9059 StartY=-51.5453 StartZ=0 EndX=0 EndY=-42.6356 EndZ=0
    g17: LineSegment StartX=23.0941 StartY=-47.7259 StartZ=0 EndX=15.2817 EndY=-46.0039 EndZ=0
    g18: LineSegment StartX=15.2817 StartY=-46.0039 StartZ=0 EndX=14.1518 EndY=-49.6356 EndZ=0
    g19: LineSegment StartX=15.2817 StartY=-42.6356 StartZ=0 EndX=15.2817 EndY=-46.0039 EndZ=0
    g20: LineSegment StartX=21.9059 StartY=-51.5453 StartZ=0 EndX=21.9059 EndY=-53.6356 EndZ=0
    g21: LineSegment StartX=23.0941 StartY=-47.7259 StartZ=0 EndX=26.5 EndY=-47.7259 EndZ=0
    g22: LineSegment StartX=15.2817 StartY=-42.6356 StartZ=0 EndX=15.2817 EndY=-46.5709 EndZ=0
    g23: LineSegment StartX=15.2817 StartY=-46.5709 StartZ=0 EndX=14.4998 EndY=-48.5171 EndZ=0
    g24: LineSegment StartX=14.4998 StartY=-48.5171 StartZ=0 EndX=21.9059 EndY=-51.5453 EndZ=0
    g25: LineSegment StartX=26.275 StartY=-49.2912 StartZ=0 EndX=26.5 EndY=-42.6356 EndZ=0
    g26: LineSegment StartX=26.5 StartY=-42.6356 StartZ=0 EndX=15.2817 EndY=-42.6356 EndZ=0
    g27: LineSegment StartX=26.275 StartY=-49.2912 StartZ=0 EndX=26.275 EndY=-53.3318 EndZ=0
    g28: LineSegment StartX=21.9059 StartY=-51.5453 StartZ=0 EndX=26.275 EndY=-53.3318 EndZ=0
  constraints (77):
    c: Coincident(g0,g1)
    c: Coincident(g1,g2)
    c: Coincident(g2,g3)
    c: Coincident(g3,g0)
    c: Horizontal(g0)
    c: Horizontal(g2)
    c: Vertical(g1)
    c: Vertical(g3)
    c: PointOnObject(g0,g-2)
    c: Distance(g0) = 22.5
    c: Distance(g1) = 4
    c: Coincident(g4,g5)
    c: Coincident(g5,g6)
    c: Coincident(g6,g7)
    c: Coincident(g7,g4)
    c: Horizontal(g4)
    c: Horizontal(g6)
    c: Vertical(g5)
    c: Vertical(g7)
    c: Coincident(g4,g0)
    c: Distance(g7) = 7
    c: Distance(g6) = 4
    c: Coincident(g8,g9)
    c: Coincident(g9,g10)
    c: Coincident(g10,g11)
    c: Coincident(g11,g8)
    c: Horizontal(g8)
    c: Horizontal(g10)
    c: Vertical(g9)
    c: Vertical(g11)
    c: Coincident(g8,g0)
    c: PointOnObject(g9,g-2)
    c: Distance(g9) = 7
    c: Coincident(g12,g9)
    c: Coincident(g12,g0)
    c: Coincident(g13,g0)
    c: Perpendicular(g13,g12)
    c: Distance(g13) = 2
    c: Coincident(g14,g0)
    c: Distance(g14) = 2
    c: Perpendicular(g14,g12)
    c: Coincident(g15,g14)
    c: Coincident(g15,g9)
    c: Coincident(g16,g13)
    c: Coincident(g16,g9)
    c: Coincident(g17,g14)
    c: PointOnObject(g17,g15)
    c: Distance(g17) = 8
    c: Coincident(g18,g17)
    c: PointOnObject(g18,g0)
    c: Perpendicular(g18,g12)
    c: PointOnObject(g19,g10)
    c: Coincident(g19,g17)
    c: Vertical(g19)
    c: Coincident(g20,g13)
    c: PointOnObject(g20,g2)
    c: Vertical(g20)
    c: Coincident(g21,g14)
    c: PointOnObject(g21,g5)
    c: Horizontal(g21)
    c: Coincident(g19,g22)
    c: Coincident(g23,g22)
    c: PointOnObject(g23,g18)
    c: Coincident(g24,g23)
    c: Coincident(g24,g13)
    c: Coincident(g25,g5)
    c: Coincident(g26,g25)
    c: Coincident(g26,g22)
    c: Vertical(g22)
    c: Angle(g15,g10) = 0.216946
    c: Angle(g12,g10) = 0.301619
    c: Angle(g9,g12) = 1.26918
    c: Coincident(g27,g25)
    c: Vertical(g27)
    c: Coincident(g28,g24)
    c: Coincident(g28,g27)
    c: Parallel(g24,g28)
FEATURE [PartDesign::Revolution] Revolution013
  Angle = 360
  Axis = (22.5,0,0)
  Base = (0,9.5e-15,-42.6356)
  Placement = pos=(0,0,0) rot=(1,0,0;1.5708rad)
  Profile = -> Sketch013
  ReferenceAxis = -> Sketch013 [Axis10]
  Reversed = true
FEATURE [PartDesign::Body] Body012
  Group = -> [Revolution013,Sketch013]
  Origin = -> Origin012
  Placement = pos=(-1.4,0,-201.4) rot=(0,0,1;0rad)
  Tip = -> Revolution013
FEATURE [Sketcher::SketchObject] Sketch014
  FullyConstrained = false
  MapMode = 5
  Placement = pos=(0,0,0) rot=(1,0,0;1.5708rad)
  Support = -> [XZ_Plane015]
  sketch-geometry (29):
    g0: LineSegment StartX=0 StartY=-49.6356 StartZ=0 EndX=22.5 EndY=-49.6356 EndZ=0
    g1: LineSegment StartX=22.5 StartY=-49.6356 StartZ=0 EndX=22.5 EndY=-53.6356 EndZ=0
    g2: LineSegment StartX=22.5 StartY=-53.6356 StartZ=0 EndX=0 EndY=-53.6356 EndZ=0
    g3: LineSegment StartX=0 StartY=-53.6356 StartZ=0 EndX=0 EndY=-49.6356 EndZ=0
    g4: LineSegment StartX=22.5 StartY=-49.6356 StartZ=0 EndX=26.5 EndY=-49.6356 EndZ=0
    g5: LineSegment StartX=26.5 StartY=-49.6356 StartZ=0 EndX=26.5 EndY=-42.6356 EndZ=0
    g6: LineSegment StartX=26.5 StartY=-42.6356 StartZ=0 EndX=22.5 EndY=-42.6356 EndZ=0
    g7: LineSegment StartX=22.5 StartY=-42.6356 StartZ=0 EndX=22.5 EndY=-49.6356 EndZ=0
    g8: LineSegment StartX=22.5 StartY=-49.6356 StartZ=0 EndX=0 EndY=-49.6356 EndZ=0
    g9: LineSegment StartX=0 StartY=-49.6356 StartZ=0 EndX=0 EndY=-42.6356 EndZ=0
    g10: LineSegment StartX=0 StartY=-42.6356 StartZ=0 EndX=22.5 EndY=-42.6356 EndZ=0
    g11: LineSegment StartX=22.5 StartY=-42.6356 StartZ=0 EndX=22.5 EndY=-49.6356 EndZ=0
    g12: LineSegment StartX=0 StartY=-42.6356 StartZ=0 EndX=22.5 EndY=-49.6356 EndZ=0
    g13: LineSegment StartX=22.5 StartY=-49.6356 StartZ=0 EndX=21.9059 EndY=-51.5453 EndZ=0
    g14: LineSegment StartX=22.5 StartY=-49.6356 StartZ=0 EndX=23.0941 EndY=-47.7259 EndZ=0
    g15: LineSegment StartX=23.0941 StartY=-47.7259 StartZ=0 EndX=0 EndY=-42.6356 EndZ=0
    g16: LineSegment StartX=21.9059 StartY=-51.5453 StartZ=0 EndX=0 EndY=-42.6356 EndZ=0
    g17: LineSegment StartX=23.0941 StartY=-47.7259 StartZ=0 EndX=15.2817 EndY=-46.0039 EndZ=0
    g18: LineSegment StartX=15.2817 StartY=-46.0039 StartZ=0 EndX=14.1518 EndY=-49.6356 EndZ=0
    g19: LineSegment StartX=15.2817 StartY=-42.6356 StartZ=0 EndX=15.2817 EndY=-46.0039 EndZ=0
    g20: LineSegment StartX=21.9059 StartY=-51.5453 StartZ=0 EndX=21.9059 EndY=-53.6356 EndZ=0
    g21: LineSegment StartX=23.0941 StartY=-47.7259 StartZ=0 EndX=26.5 EndY=-47.7259 EndZ=0
    g22: LineSegment StartX=15.2817 StartY=-42.6356 StartZ=0 EndX=15.2817 EndY=-46.5709 EndZ=0
    g23: LineSegment StartX=15.2817 StartY=-46.5709 StartZ=0 EndX=14.4998 EndY=-48.5171 EndZ=0
    g24: LineSegment StartX=14.4998 StartY=-48.5171 StartZ=0 EndX=21.9059 EndY=-51.5453 EndZ=0
    g25: LineSegment StartX=26.275 StartY=-49.2912 StartZ=0 EndX=26.5 EndY=-42.6356 EndZ=0
    g26: LineSegment StartX=26.5 StartY=-42.6356 StartZ=0 EndX=15.2817 EndY=-42.6356 EndZ=0
    g27: LineSegment StartX=26.275 StartY=-49.2912 StartZ=0 EndX=26.275 EndY=-53.3318 EndZ=0
    g28: LineSegment StartX=21.9059 StartY=-51.5453 StartZ=0 EndX=26.275 EndY=-53.3318 EndZ=0
  constraints (77):
    c: Coincident(g0,g1)
    c: Coincident(g1,g2)
    c: Coincident(g2,g3)
    c: Coincident(g3,g0)
    c: Horizontal(g0)
    c: Horizontal(g2)
    c: Vertical(g1)
    c: Vertical(g3)
    c: PointOnObject(g0,g-2)
    c: Distance(g0) = 22.5
    c: Distance(g1) = 4
    c: Coincident(g4,g5)
    c: Coincident(g5,g6)
    c: Coincident(g6,g7)
    c: Coincident(g7,g4)
    c: Horizontal(g4)
    c: Horizontal(g6)
    c: Vertical(g5)
    c: Vertical(g7)
    c: Coincident(g4,g0)
    c: Distance(g7) = 7
    c: Distance(g6) = 4
    c: Coincident(g8,g9)
    c: Coincident(g9,g10)
    c: Coincident(g10,g11)
    c: Coincident(g11,g8)
    c: Horizontal(g8)
    c: Horizontal(g10)
    c: Vertical(g9)
    c: Vertical(g11)
    c: Coincident(g8,g0)
    c: PointOnObject(g9,g-2)
    c: Distance(g9) = 7
    c: Coincident(g12,g9)
    c: Coincident(g12,g0)
    c: Coincident(g13,g0)
    c: Perpendicular(g13,g12)
    c: Distance(g13) = 2
    c: Coincident(g14,g0)
    c: Distance(g14) = 2
    c: Perpendicular(g14,g12)
    c: Coincident(g15,g14)
    c: Coincident(g15,g9)
    c: Coincident(g16,g13)
    c: Coincident(g16,g9)
    c: Coincident(g17,g14)
    c: PointOnObject(g17,g15)
    c: Distance(g17) = 8
    c: Coincident(g18,g17)
    c: PointOnObject(g18,g0)
    c: Perpendicular(g18,g12)
    c: PointOnObject(g19,g10)
    c: Coincident(g19,g17)
    c: Vertical(g19)
    c: Coincident(g20,g13)
    c: PointOnObject(g20,g2)
    c: Vertical(g20)
    c: Coincident(g21,g14)
    c: PointOnObject(g21,g5)
    c: Horizontal(g21)
    c: Coincident(g19,g22)
    c: Coincident(g23,g22)
    c: PointOnObject(g23,g18)
    c: Coincident(g24,g23)
    c: Coincident(g24,g13)
    c: Coincident(g25,g5)
    c: Coincident(g26,g25)
    c: Coincident(g26,g22)
    c: Vertical(g22)
    c: Angle(g15,g10) = 0.216946
    c: Angle(g12,g10) = 0.301619
    c: Angle(g9,g12) = 1.26918
    c: Coincident(g27,g25)
    c: Vertical(g27)
    c: Coincident(g28,g24)
    c: Coincident(g28,g27)
    c: Parallel(g24,g28)
FEATURE [PartDesign::Revolution] Revolution014
  Angle = 360
  Axis = (22.5,0,0)
  Base = (0,9.5e-15,-42.6356)
  Placement = pos=(0,0,0) rot=(1,0,0;1.5708rad)
  Profile = -> Sketch014
  ReferenceAxis = -> Sketch014 [Axis10]
  Reversed = true
FEATURE [PartDesign::Body] Body013
  Group = -> [Revolution014,Sketch014]
  Origin = -> Origin013
  Placement = pos=(-9.5,0,-201.4) rot=(0,0,1;0rad)
  Tip = -> Revolution014
FEATURE [Part::Cylinder] Cylinder1811  label="Válec1811"
  Angle = 360
  AttacherType = Attacher::AttachEngine3D
  Height = 100
  Placement = pos=(100,0,21) rot=(0.57735,0.57735,0.57735;2.0944rad)
  Radius = 1.5
FEATURE [Part::Box] Box758  label="Krychle758"
  AttacherType = Attacher::AttachEngine3D
  Height = 24
  Length = 2
  Placement = pos=(194.5,-4,4) rot=(0,0,1;0rad)
  Width = 8
FEATURE [Part::FeaturePython] Tube040  # WARN: FeaturePython — macro-defined, semantics opaque (R4)
  AttacherType = Attacher::AttachEngine3D
  Height = 32
  InnerRadius = 4.1
  OuterRadius = 8.5
  Placement = pos=(200,0,-8) rot=(0,0,1;0rad)
FEATURE [Part::FeaturePython] bevelgear011  # WARN: FeaturePython — macro-defined, semantics opaque (R4)
  AttacherType = Attacher::AttachEngine3D
  Placement = pos=(26,0,-244) rot=(0,-1,0;1.5708rad)
  backlash = 0.1
  beta = 12
  clearance = 0.1
  height = 30
  module = 2
  numpoints = 6
  pitch_angle = 17.29
  pressure_angle = 25
  reset_origin = true
  teeth = 9
  version = 0.0.3
FEATURE [Part::Common] Common013
  Base = -> bevelgear011
  Tool = -> Body012
FEATURE [Part::Cut] Cut554
  Base = -> Common013
  Placement = pos=(0,81,294) rot=(0,0,1;1.5708rad)
  Tool = -> Body013
FEATURE [Part::MultiFuse] Fusion004
  Shapes = -> [Tube040,Box758]
FEATURE [Part::Box] Box759  label="Krychle759"
  AttacherType = Attacher::AttachEngine3D
  Height = 6
  Length = 6
  Placement = pos=(196.5,-3,12) rot=(0,0,1;1.5708rad)
  Width = 2
FEATURE [Part::Cylinder] Cylinder1812  label="Válec1812"
  Angle = 360
  AttacherType = Attacher::AttachEngine3D
  Height = 10
  Placement = pos=(0,118,50) rot=(1,0,0;1.5708rad)
  Radius = 4.1
FEATURE [Part::Box] Box760  label="Krychle760"
  AttacherType = Attacher::AttachEngine3D
  Height = 40
  Length = 40
  Placement = pos=(-20,110,30) rot=(0,0,1;0rad)
  Width = 20
FEATURE [Part::Cylinder] Cylinder1813  label="Válec1813"
  Angle = 360
  AttacherType = Attacher::AttachEngine3D
  Height = 100
  Placement = pos=(100,0,15) rot=(0.57735,0.57735,0.57735;2.0944rad)
  Radius = 1.5
FEATURE [Part::Compound] Compound914
  Links = -> [Cylinder1811,Cylinder1813]
  Placement = pos=(0,0,-20) rot=(0,0,1;0rad)
FEATURE [Part::Cylinder] Cylinder1814  label="Válec1814"
  Angle = 360
  AttacherType = Attacher::AttachEngine3D
  Height = 4
  Placement = pos=(0,110,50) rot=(1,0,0;1.5708rad)
  Radius = 11
FEATURE [Part::Cut] Cut556
  Base = -> Cylinder1814
  Tool = -> Cylinder1812
FEATURE [Part::Cut] Cut557
  Base = -> Cut556
  Tool = -> Box760
FEATURE [Part::Chamfer] Chamfer062
  Base = -> Cut557
  Edges = 1 edges r=2.5: [Edge3]
FEATURE [Part::Box] Box761  label="Krychle761"
  AttacherType = Attacher::AttachEngine3D
  Height = 6
  Length = 6
  Placement = pos=(196.5,-3,18) rot=(0,0,1;1.5708rad)
  Width = 2
FEATURE [Part::Compound] Compound915
  Links = -> [Box761,Box759]
  Placement = pos=(0,0,-20) rot=(0,0,1;0rad)
FEATURE [Part::Cut] Cut553
  Base = -> Fusion004
  Tool = -> Compound915
FEATURE [Part::Cut] Cut555  label="super_spojka004"
  Base = -> Cut553
  Placement = pos=(-200,134,50) rot=(1,0,0;1.5708rad)
  Tool = -> Compound914
FEATURE [Part::Compound] Compound916  label="Base_rear-gear-small"
  Links = -> [Cut554,Cut555,Chamfer062]
  Placement = pos=(0,0,1) rot=(0,0,1;0rad)
FEATURE [Part::FeaturePython] bevelgear012  # WARN: FeaturePython — macro-defined, semantics opaque (R4)
  AttacherType = Attacher::AttachEngine3D
  Placement = pos=(0,0,-254.4) rot=(1,0,0;3.14159rad)
  backlash = 0
  beta = 12
  clearance = 0.1
  height = 16
  module = 0.1
  numpoints = 6
  pitch_angle = 72.71
  pressure_angle = 21
  reset_origin = true
  teeth = 36
  version = 0.0.3
FEATURE [Part::Cylinder] Cylinder1815  label="Válec1815"
  Angle = 360
  AttacherType = Attacher::AttachEngine3D
  Height = 30
  Placement = pos=(0,72,232) rot=(0,0,1;0rad)
  Radius = 1.5
FEATURE [Part::Cylinder] Cylinder1816  label="Válec1816"
  Angle = 360
  AttacherType = Attacher::AttachEngine3D
  Height = 30
  Placement = pos=(11,83,232) rot=(0,0,1;0rad)
  Radius = 1.5
FEATURE [Part::Cylinder] Cylinder1817  label="Válec1817"
  Angle = 360
  AttacherType = Attacher::AttachEngine3D
  Height = 3
  Placement = pos=(0,72,232) rot=(0,0,1;0rad)
  Radius = 3
FEATURE [Part::Cylinder] Cylinder1818  label="Válec1818"
  Angle = 360
  AttacherType = Attacher::AttachEngine3D
  Height = 30
  Placement = pos=(0,94,232) rot=(0,0,1;0rad)
  Radius = 1.5
FEATURE [Part::Cylinder] Cylinder1819  label="Válec1819"
  Angle = 360
  AttacherType = Attacher::AttachEngine3D
  Height = 3
  Placement = pos=(-11,83,232) rot=(0,0,1;0rad)
  Radius = 3
FEATURE [Part::Cylinder] Cylinder1820  label="Válec1820"
  Angle = 360
  AttacherType = Attacher::AttachEngine3D
  Height = 3
  Placement = pos=(11,83,232) rot=(0,0,1;0rad)
  Radius = 3
FEATURE [Part::Cylinder] Cylinder1821  label="Válec1821"
  Angle = 360
  AttacherType = Attacher::AttachEngine3D
  Height = 30
  Placement = pos=(-11,83,232) rot=(0,0,1;0rad)
  Radius = 1.5
FEATURE [Part::Cylinder] Cylinder1822  label="Válec1822"
  Angle = 360
  AttacherType = Attacher::AttachEngine3D
  Height = 10
  Placement = pos=(0,83,242) rot=(0,0,1;0rad)
  Radius = 15.1
FEATURE [Sketcher::SketchObject] Sketch015
  FullyConstrained = false
  MapMode = 5
  Placement = pos=(0,0,0) rot=(1,0,0;1.5708rad)
  Support = -> [XZ_Plane016]
  sketch-geometry (29):
    g0: LineSegment StartX=0 StartY=-63.1814 StartZ=0 EndX=22.5 EndY=-63.1814 EndZ=0
    g1: LineSegment StartX=22.5 StartY=-63.1814 StartZ=0 EndX=22.5 EndY=-67.1814 EndZ=0
    g2: LineSegment StartX=22.5 StartY=-67.1814 StartZ=0 EndX=0 EndY=-67.1814 EndZ=0
    g3: LineSegment StartX=0 StartY=-67.1814 StartZ=0 EndX=0 EndY=-63.1814 EndZ=0
    g4: LineSegment StartX=22.5 StartY=-63.1814 StartZ=0 EndX=26.5 EndY=-63.1814 EndZ=0
    g5: LineSegment StartX=26.5 StartY=-63.1814 StartZ=0 EndX=26.5 EndY=-58.1814 EndZ=0
    g6: LineSegment StartX=26.5 StartY=-58.1814 StartZ=0 EndX=22.5 EndY=-58.1814 EndZ=0
    g7: LineSegment StartX=22.5 StartY=-58.1814 StartZ=0 EndX=22.5 EndY=-63.1814 EndZ=0
    g8: LineSegment StartX=22.5 StartY=-63.1814 StartZ=0 EndX=0 EndY=-63.1814 EndZ=0
    g9: LineSegment StartX=0 StartY=-63.1814 StartZ=0 EndX=0 EndY=-56.1814 EndZ=0
    g10: LineSegment StartX=0 StartY=-56.1814 StartZ=0 EndX=22.5 EndY=-56.1814 EndZ=0
    g11: LineSegment StartX=22.5 StartY=-56.1814 StartZ=0 EndX=22.5 EndY=-63.1814 EndZ=0
    g12: LineSegment StartX=0 StartY=-56.1814 StartZ=0 EndX=22.5 EndY=-63.1814 EndZ=0
    g13: LineSegment StartX=22.5 StartY=-63.1814 StartZ=0 EndX=21.9059 EndY=-65.0911 EndZ=0
    g14: LineSegment StartX=22.5 StartY=-63.1814 StartZ=0 EndX=23.0941 EndY=-61.2717 EndZ=0
    g15: LineSegment StartX=23.0941 StartY=-61.2717 StartZ=0 EndX=0 EndY=-56.1814 EndZ=0
    g16: LineSegment StartX=21.9059 StartY=-65.0911 StartZ=0 EndX=0 EndY=-56.1814 EndZ=0
    g17: LineSegment StartX=23.0941 StartY=-61.2717 StartZ=0 EndX=15.2817 EndY=-59.5497 EndZ=0
    g18: LineSegment StartX=15.2817 StartY=-59.5497 StartZ=0 EndX=14.1518 EndY=-63.1814 EndZ=0
    g19: LineSegment StartX=15.2817 StartY=-56.1814 StartZ=0 EndX=15.2817 EndY=-59.5497 EndZ=0
    g20: LineSegment StartX=21.9059 StartY=-65.0911 StartZ=0 EndX=21.9059 EndY=-67.1814 EndZ=0
    g21: LineSegment StartX=23.0941 StartY=-61.2717 StartZ=0 EndX=26.5 EndY=-61.2717 EndZ=0
    g22: LineSegment StartX=21.9059 StartY=-67.1814 StartZ=0 EndX=21.9059 EndY=-65.0911 EndZ=0
    g23: LineSegment StartX=21.9059 StartY=-65.0911 StartZ=0 EndX=23.0941 EndY=-61.2717 EndZ=0
    g24: LineSegment StartX=23.0941 StartY=-61.2717 StartZ=0 EndX=15.2817 EndY=-59.5497 EndZ=0
    g25: LineSegment StartX=15.2817 StartY=-59.5497 StartZ=0 EndX=14.1518 EndY=-63.1814 EndZ=0
    g26: LineSegment StartX=14.1518 StartY=-63.1814 StartZ=0 EndX=0 EndY=-63.1814 EndZ=0
    g27: LineSegment StartX=0 StartY=-63.1814 StartZ=0 EndX=0 EndY=-67.1814 EndZ=0
    g28: LineSegment StartX=0 StartY=-67.1814 StartZ=0 EndX=21.9059 EndY=-67.1814 EndZ=0
  constraints (77):
    c: Coincident(g0,g1)
    c: Coincident(g1,g2)
    c: Coincident(g2,g3)
    c: Coincident(g3,g0)
    c: Horizontal(g0)
    c: Horizontal(g2)
    c: Vertical(g1)
    c: Vertical(g3)
    c: PointOnObject(g0,g-2)
    c: Distance(g0) = 22.5
    c: Distance(g1) = 4
    c: Coincident(g4,g5)
    c: Coincident(g5,g6)
    c: Coincident(g6,g7)
    c: Coincident(g7,g4)
    c: Horizontal(g4)
    c: Horizontal(g6)
    c: Vertical(g5)
    c: Vertical(g7)
    c: Coincident(g4,g0)
    c: Distance(g7) = 5
    c: Distance(g6) = 4
    c: Coincident(g8,g9)
    c: Coincident(g9,g10)
    c: Coincident(g10,g11)
    c: Coincident(g11,g8)
    c: Horizontal(g8)
    c: Horizontal(g10)
    c: Vertical(g9)
    c: Vertical(g11)
    c: Coincident(g8,g0)
    c: PointOnObject(g9,g-2)
    c: Distance(g9) = 7
    c: Coincident(g12,g9)
    c: Coincident(g12,g0)
    c: Coincident(g13,g0)
    c: Perpendicular(g13,g12)
    c: Distance(g13) = 2
    c: Coincident(g14,g0)
    c: Distance(g14) = 2
    c: Perpendicular(g14,g12)
    c: Coincident(g15,g14)
    c: Coincident(g15,g9)
    c: Coincident(g16,g13)
    c: Coincident(g16,g9)
    c: Coincident(g17,g14)
    c: PointOnObject(g17,g15)
    c: Distance(g17) = 8
    c: Coincident(g18,g17)
    c: PointOnObject(g18,g0)
    c: Perpendicular(g18,g12)
    c: PointOnObject(g19,g10)
    c: Coincident(g19,g17)
    c: Vertical(g19)
    c: Coincident(g20,g13)
    c: PointOnObject(g20,g2)
    c: Vertical(g20)
    c: Coincident(g21,g14)
    c: PointOnObject(g21,g5)
    c: Horizontal(g21)
    c: Angle(g15,g10) = 0.216946
    c: Angle(g12,g10) = 0.301619
    c: Angle(g9,g12) = 1.26918
    c: Coincident(g22,g20)
    c: Coincident(g22,g13)
    c: Coincident(g22,g23)
    c: Coincident(g23,g14)
    c: Coincident(g23,g24)
    c: Coincident(g24,g17)
    c: Coincident(g24,g25)
    c: Coincident(g25,g18)
    c: Coincident(g26,g25)
    c: Coincident(g26,g0)
    c: Coincident(g27,g26)
    c: Coincident(g27,g2)
    c: Coincident(g28,g27)
    c: Coincident(g28,g22)
FEATURE [Part::Cylinder] Cylinder1823  label="Válec1823"
  Angle = 360
  AttacherType = Attacher::AttachEngine3D
  Height = 30
  Placement = pos=(11,83,232) rot=(0,0,1;0rad)
  Radius = 1.5
FEATURE [Part::Cylinder] Cylinder1824  label="Válec1824"
  Angle = 360
  AttacherType = Attacher::AttachEngine3D
  Height = 30
  Placement = pos=(0,83,232) rot=(0,0,1;0rad)
  Radius = 2.65
FEATURE [Part::Cylinder] Cylinder1825  label="Válec1825"
  Angle = 360
  AttacherType = Attacher::AttachEngine3D
  Height = 30
  Placement = pos=(0,72,232) rot=(0,0,1;0rad)
  Radius = 1.5
FEATURE [Part::Cylinder] Cylinder1826  label="Válec1826"
  Angle = 360
  AttacherType = Attacher::AttachEngine3D
  Height = 30
  Placement = pos=(-11,83,232) rot=(0,0,1;0rad)
  Radius = 1.5
FEATURE [Part::Cylinder] Cylinder1827  label="Válec1827"
  Angle = 360
  AttacherType = Attacher::AttachEngine3D
  Height = 30
  Placement = pos=(0,94,232) rot=(0,0,1;0rad)
  Radius = 1.5
FEATURE [Part::Compound] Compound917
  Links = -> [Cylinder1821,Cylinder1823,Cylinder1825,Cylinder1827]
FEATURE [Part::Cylinder] Cylinder1828  label="Válec1828"
  Angle = 360
  AttacherType = Attacher::AttachEngine3D
  Height = 40
  Placement = pos=(0,83,232) rot=(0,0,1;0rad)
  Radius = 2.65
FEATURE [Part::Cylinder] Cylinder1829  label="Válec1829"
  Angle = 360
  AttacherType = Attacher::AttachEngine3D
  Height = 17
  Placement = pos=(0,83,252) rot=(0,0,1;0rad)
  Radius = 8
FEATURE [Part::Cylinder] Cylinder1830  label="Válec1830"
  Angle = 360
  AttacherType = Attacher::AttachEngine3D
  Height = 3
  Placement = pos=(0,94,232) rot=(0,0,1;0rad)
  Radius = 3
FEATURE [Part::Cut] Cut559
  Base = -> Cylinder1829
  Tool = -> Cylinder1828
FEATURE [Part::Cut] Cut560
  Base = -> Cylinder1822
  Tool = -> Compound917
FEATURE [PartDesign::Revolution] Revolution015
  Angle = 360
  Axis = (0,-9e-16,4)
  Base = (0,1.49e-14,-67.1814)
  Placement = pos=(0,0,0) rot=(1,0,0;1.5708rad)
  Profile = -> Sketch015
  ReferenceAxis = -> Sketch015 [Axis3]
  Reversed = true
FEATURE [PartDesign::Body] Body014
  Group = -> [Revolution015,Sketch015]
  Origin = -> Origin014
  Placement = pos=(0,0,-199.6) rot=(0,0,1;0rad)
  Tip = -> Revolution015
FEATURE [Part::Common] Common001
  Base = -> Body014
  Placement = pos=(0,83,507) rot=(0,0,1;0rad)
  Tool = -> bevelgear012
FEATURE [Part::Compound] Compound918
  Links = -> [Cylinder1826,Cylinder1816,Cylinder1815,Cylinder1818]
FEATURE [Part::Cut] Cut561
  Base = -> Common001
  Tool = -> Compound918
FEATURE [Part::Compound] Compound919
  Links = -> [Cylinder1819,Cylinder1820,Cylinder1817,Cylinder1830]
  Placement = pos=(0,0,17) rot=(0,0,1;0rad)
FEATURE [Part::Cut] Cut558
  Base = -> Cut560
  Tool = -> Compound919
FEATURE [Part::Cut] Cut562
  Base = -> Cut558
  Tool = -> Cylinder1824
FEATURE [Part::Compound] Compound920  label="Base_rear-gear-large-old"
  Links = -> [Cut561,Cut562,Cut559]
  Placement = pos=(0,0,-200.2) rot=(0,0,1;0rad)
FEATURE [Sketcher::SketchObject] Sketch016
  FullyConstrained = false
  MapMode = 5
  Placement = pos=(0,0,0) rot=(1,0,0;1.5708rad)
  Support = -> [XZ_Plane017]
  sketch-geometry (29):
    g0: LineSegment StartX=0 StartY=-63.1814 StartZ=0 EndX=22.5 EndY=-63.1814 EndZ=0
    g1: LineSegment StartX=22.5 StartY=-63.1814 StartZ=0 EndX=22.5 EndY=-67.1814 EndZ=0
    g2: LineSegment StartX=22.5 StartY=-67.1814 StartZ=0 EndX=0 EndY=-67.1814 EndZ=0
    g3: LineSegment StartX=0 StartY=-67.1814 StartZ=0 EndX=0 EndY=-63.1814 EndZ=0
    g4: LineSegment StartX=22.5 StartY=-63.1814 StartZ=0 EndX=26.5 EndY=-63.1814 EndZ=0
    g5: LineSegment StartX=26.5 StartY=-63.1814 StartZ=0 EndX=26.5 EndY=-58.1814 EndZ=0
    g6: LineSegment StartX=26.5 StartY=-58.1814 StartZ=0 EndX=22.5 EndY=-58.1814 EndZ=0
    g7: LineSegment StartX=22.5 StartY=-58.1814 StartZ=0 EndX=22.5 EndY=-63.1814 EndZ=0
    g8: LineSegment StartX=22.5 StartY=-63.1814 StartZ=0 EndX=0 EndY=-63.1814 EndZ=0
    g9: LineSegment StartX=0 StartY=-63.1814 StartZ=0 EndX=0 EndY=-56.1814 EndZ=0
    g10: LineSegment StartX=0 StartY=-56.1814 StartZ=0 EndX=22.5 EndY=-56.1814 EndZ=0
    g11: LineSegment StartX=22.5 StartY=-56.1814 StartZ=0 EndX=22.5 EndY=-63.1814 EndZ=0
    g12: LineSegment StartX=0 StartY=-56.1814 StartZ=0 EndX=22.5 EndY=-63.1814 EndZ=0
    g13: LineSegment StartX=22.5 StartY=-63.1814 StartZ=0 EndX=21.9059 EndY=-65.0911 EndZ=0
    g14: LineSegment StartX=22.5 StartY=-63.1814 StartZ=0 EndX=23.0941 EndY=-61.2717 EndZ=0
    g15: LineSegment StartX=23.0941 StartY=-61.2717 StartZ=0 EndX=0 EndY=-56.1814 EndZ=0
    g16: LineSegment StartX=21.9059 StartY=-65.0911 StartZ=0 EndX=0 EndY=-56.1814 EndZ=0
    g17: LineSegment StartX=23.0941 StartY=-61.2717 StartZ=0 EndX=15.2817 EndY=-59.5497 EndZ=0
    g18: LineSegment StartX=15.2817 StartY=-59.5497 StartZ=0 EndX=14.1518 EndY=-63.1814 EndZ=0
    g19: LineSegment StartX=15.2817 StartY=-56.1814 StartZ=0 EndX=15.2817 EndY=-59.5497 EndZ=0
    g20: LineSegment StartX=21.9059 StartY=-65.0911 StartZ=0 EndX=21.9059 EndY=-67.1814 EndZ=0
    g21: LineSegment StartX=23.0941 StartY=-61.2717 StartZ=0 EndX=26.5 EndY=-61.2717 EndZ=0
    g22: LineSegment StartX=21.9059 StartY=-67.1814 StartZ=0 EndX=21.9059 EndY=-65.0911 EndZ=0
    g23: LineSegment StartX=21.9059 StartY=-65.0911 StartZ=0 EndX=23.0941 EndY=-61.2717 EndZ=0
    g24: LineSegment StartX=23.0941 StartY=-61.2717 StartZ=0 EndX=15.2817 EndY=-59.5497 EndZ=0
    g25: LineSegment StartX=15.2817 StartY=-59.5497 StartZ=0 EndX=14.1518 EndY=-63.1814 EndZ=0
    g26: LineSegment StartX=14.1518 StartY=-63.1814 StartZ=0 EndX=0 EndY=-63.1814 EndZ=0
    g27: LineSegment StartX=0 StartY=-63.1814 StartZ=0 EndX=0 EndY=-67.1814 EndZ=0
    g28: LineSegment StartX=0 StartY=-67.1814 StartZ=0 EndX=21.9059 EndY=-67.1814 EndZ=0
  constraints (77):
    c: Coincident(g0,g1)
    c: Coincident(g1,g2)
    c: Coincident(g2,g3)
    c: Coincident(g3,g0)
    c: Horizontal(g0)
    c: Horizontal(g2)
    c: Vertical(g1)
    c: Vertical(g3)
    c: PointOnObject(g0,g-2)
    c: Distance(g0) = 22.5
    c: Distance(g1) = 4
    c: Coincident(g4,g5)
    c: Coincident(g5,g6)
    c: Coincident(g6,g7)
    c: Coincident(g7,g4)
    c: Horizontal(g4)
    c: Horizontal(g6)
    c: Vertical(g5)
    c: Vertical(g7)
    c: Coincident(g4,g0)
    c: Distance(g7) = 5
    c: Distance(g6) = 4
    c: Coincident(g8,g9)
    c: Coincident(g9,g10)
    c: Coincident(g10,g11)
    c: Coincident(g11,g8)
    c: Horizontal(g8)
    c: Horizontal(g10)
    c: Vertical(g9)
    c: Vertical(g11)
    c: Coincident(g8,g0)
    c: PointOnObject(g9,g-2)
    c: Distance(g9) = 7
    c: Coincident(g12,g9)
    c: Coincident(g12,g0)
    c: Coincident(g13,g0)
    c: Perpendicular(g13,g12)
    c: Distance(g13) = 2
    c: Coincident(g14,g0)
    c: Distance(g14) = 2
    c: Perpendicular(g14,g12)
    c: Coincident(g15,g14)
    c: Coincident(g15,g9)
    c: Coincident(g16,g13)
    c: Coincident(g16,g9)
    c: Coincident(g17,g14)
    c: PointOnObject(g17,g15)
    c: Distance(g17) = 8
    c: Coincident(g18,g17)
    c: PointOnObject(g18,g0)
    c: Perpendicular(g18,g12)
    c: PointOnObject(g19,g10)
    c: Coincident(g19,g17)
    c: Vertical(g19)
    c: Coincident(g20,g13)
    c: PointOnObject(g20,g2)
    c: Vertical(g20)
    c: Coincident(g21,g14)
    c: PointOnObject(g21,g5)
    c: Horizontal(g21)
    c: Angle(g15,g10) = 0.216946
    c: Angle(g12,g10) = 0.301619
    c: Angle(g9,g12) = 1.26918
    c: Coincident(g22,g20)
    c: Coincident(g22,g13)
    c: Coincident(g22,g23)
    c: Coincident(g23,g14)
    c: Coincident(g23,g24)
    c: Coincident(g24,g17)
    c: Coincident(g24,g25)
    c: Coincident(g25,g18)
    c: Coincident(g26,g25)
    c: Coincident(g26,g0)
    c: Coincident(g27,g26)
    c: Coincident(g27,g2)
    c: Coincident(g28,g27)
    c: Coincident(g28,g22)
FEATURE [Part::Cylinder] Cylinder600  label="Válec600"
  Angle = 360
  AttacherType = Attacher::AttachEngine3D
  Height = 30
  Placement = pos=(0,72,15) rot=(0,0,1;0rad)
  Radius = 1.5
FEATURE [Part::Box] Box762  label="Krychle762"
  AttacherType = Attacher::AttachEngine3D
  Height = 20
  Length = 6
  Placement = pos=(8,80,38) rot=(0,0,1;0rad)
  Width = 6
FEATURE [Part::FeaturePython] wormgear028  # WARN: FeaturePython — macro-defined, semantics opaque (R4)
  AttacherType = Attacher::AttachEngine3D
  Placement = pos=(0,83,32) rot=(0,0,1;0.069813rad)
  beta = 33.1113
  clearance = 0.25
  diameter = 46
  head = 0
  height = 5
  module = 1
  pressure_angle = 20
  reverse_pitch = false
  teeth = 30
  version = 0.0.3
FEATURE [Part::FeaturePython] bevelgear013  # WARN: FeaturePython — macro-defined, semantics opaque (R4)
  AttacherType = Attacher::AttachEngine3D
  Placement = pos=(0,0,-254.4) rot=(1,0,0;3.14159rad)
  backlash = 0
  beta = 12
  clearance = 0.1
  height = 16
  module = 0.1
  numpoints = 6
  pitch_angle = 72.71
  pressure_angle = 21
  reset_origin = true
  teeth = 36
  version = 0.0.3
FEATURE [Part::FeaturePython] wormgear029  # WARN: FeaturePython — macro-defined, semantics opaque (R4)
  AttacherType = Attacher::AttachEngine3D
  Placement = pos=(0,83,37) rot=(0,0,1;0.191986rad)
  beta = 33.1113
  clearance = 0.25
  diameter = 46
  head = 0
  height = 5
  module = 1
  pressure_angle = 20
  reverse_pitch = true
  teeth = 30
  version = 0.0.3
FEATURE [Part::Cylinder] Cylinder660  label="Válec660"
  Angle = 360
  AttacherType = Attacher::AttachEngine3D
  Height = 30
  Placement = pos=(11,83,232) rot=(0,0,1;0rad)
  Radius = 1.5
FEATURE [Part::Cylinder] Cylinder661  label="Válec661"
  Angle = 360
  AttacherType = Attacher::AttachEngine3D
  Height = 3
  Placement = pos=(0,72,232) rot=(0,0,1;0rad)
  Radius = 3
FEATURE [Part::Cylinder] Cylinder597  label="Válec597"
  Angle = 360
  AttacherType = Attacher::AttachEngine3D
  Height = 40
  Placement = pos=(0,83,15) rot=(0,0,1;0rad)
  Radius = 2.65
FEATURE [Part::Cylinder] Cylinder1831  label="Válec1831"
  Angle = 360
  AttacherType = Attacher::AttachEngine3D
  Height = 30
  Placement = pos=(11,83,15) rot=(0,0,1;0rad)
  Radius = 1.5
FEATURE [Part::Cylinder] Cylinder658  label="Válec658"
  Angle = 360
  AttacherType = Attacher::AttachEngine3D
  Height = 30
  Placement = pos=(0,72,232) rot=(0,0,1;0rad)
  Radius = 1.5
FEATURE [Part::Box] Box763  label="Krychle763"
  AttacherType = Attacher::AttachEngine3D
  Height = 20
  Length = 6
  Placement = pos=(-14,80,38) rot=(0,0,1;0rad)
  Width = 6
FEATURE [Part::Cylinder] Cylinder1832  label="Válec1832"
  Angle = 360
  AttacherType = Attacher::AttachEngine3D
  Height = 40
  Placement = pos=(0,83,15) rot=(0,0,1;0rad)
  Radius = 2.65
FEATURE [Part::Cylinder] Cylinder659  label="Válec659"
  Angle = 360
  AttacherType = Attacher::AttachEngine3D
  Height = 30
  Placement = pos=(-11,83,232) rot=(0,0,1;0rad)
  Radius = 1.5
FEATURE [Part::Cylinder] Cylinder1833  label="Válec1833"
  Angle = 360
  AttacherType = Attacher::AttachEngine3D
  Height = 30
  Placement = pos=(0,94,15) rot=(0,0,1;0rad)
  Radius = 1.5
FEATURE [Part::Cylinder] Cylinder1834  label="Válec1834"
  Angle = 360
  AttacherType = Attacher::AttachEngine3D
  Height = 30
  Placement = pos=(11,83,15) rot=(0,0,1;0rad)
  Radius = 1.5
FEATURE [Part::Cylinder] Cylinder1835  label="Válec1835"
  Angle = 360
  AttacherType = Attacher::AttachEngine3D
  Height = 30
  Placement = pos=(-11,83,15) rot=(0,0,1;0rad)
  Radius = 1.5
FEATURE [Part::Cylinder] Cylinder599  label="Válec599"
  Angle = 360
  AttacherType = Attacher::AttachEngine3D
  Height = 30
  Placement = pos=(0,94,15) rot=(0,0,1;0rad)
  Radius = 1.5
FEATURE [Part::Box] Box764  label="Krychle764"
  AttacherType = Attacher::AttachEngine3D
  Height = 20
  Length = 6
  Placement = pos=(-3,69,38) rot=(0,0,1;0rad)
  Width = 6
FEATURE [Part::Cylinder] Cylinder598  label="Válec598"
  Angle = 360
  AttacherType = Attacher::AttachEngine3D
  Height = 30
  Placement = pos=(0,72,15) rot=(0,0,1;0rad)
  Radius = 1.5
FEATURE [Part::Cylinder] Cylinder1836  label="Válec1836"
  Angle = 360
  AttacherType = Attacher::AttachEngine3D
  Height = 30
  Placement = pos=(-11,83,15) rot=(0,0,1;0rad)
  Radius = 1.5
FEATURE [Part::Box] Box765  label="Krychle765"
  AttacherType = Attacher::AttachEngine3D
  Height = 20
  Length = 6
  Placement = pos=(-3,91,38) rot=(0,0,1;0rad)
  Width = 6
FEATURE [Part::Compound] Compound364
  Links = -> [Box762,Box763,Box764,Box765]
FEATURE [Part::Compound] Compound367
  Links = -> [Cylinder1836,Cylinder1831,Cylinder600,Cylinder1833]
FEATURE [Part::Compound] Compound365
  Links = -> [Cylinder1835,Cylinder1834,Cylinder598,Cylinder599]
FEATURE [PartDesign::Revolution] Revolution016
  Angle = 360
  Axis = (0,-9e-16,4)
  Base = (0,1.49e-14,-67.1814)
  Placement = pos=(0,0,0) rot=(1,0,0;1.5708rad)
  Profile = -> Sketch016
  ReferenceAxis = -> Sketch016 [Axis3]
  Reversed = true
FEATURE [PartDesign::Body] Body015
  Group = -> [Revolution016,Sketch016]
  Origin = -> Origin015
  Placement = pos=(0,0,-199.6) rot=(0,0,1;0rad)
  Tip = -> Revolution016
FEATURE [Part::Common] Common002
  Base = -> Body015
  Placement = pos=(0,83,507) rot=(0,0,1;0rad)
  Tool = -> bevelgear013
FEATURE [Part::Cylinder] Cylinder1837  label="Válec1837"
  Angle = 360
  AttacherType = Attacher::AttachEngine3D
  Height = 30
  Placement = pos=(0,83,232) rot=(0,0,1;0rad)
  Radius = 2.65
FEATURE [Part::Cylinder] Cylinder1838  label="Válec1838"
  Angle = 360
  AttacherType = Attacher::AttachEngine3D
  Height = 17
  Placement = pos=(0,83,252) rot=(0,0,1;0rad)
  Radius = 8
FEATURE [Part::Cylinder] Cylinder1839  label="Válec1839"
  Angle = 360
  AttacherType = Attacher::AttachEngine3D
  Height = 30
  Placement = pos=(11,83,232) rot=(0,0,1;0rad)
  Radius = 1.5
FEATURE [Part::Cylinder] Cylinder1840  label="Válec1840"
  Angle = 360
  AttacherType = Attacher::AttachEngine3D
  Height = 30
  Placement = pos=(0,94,232) rot=(0,0,1;0rad)
  Radius = 1.5
FEATURE [Part::Cylinder] Cylinder1841  label="Válec1841"
  Angle = 360
  AttacherType = Attacher::AttachEngine3D
  Height = 40
  Placement = pos=(0,83,232) rot=(0,0,1;0rad)
  Radius = 2.65
FEATURE [Part::Cylinder] Cylinder664  label="Válec664"
  Angle = 360
  AttacherType = Attacher::AttachEngine3D
  Height = 3
  Placement = pos=(11,83,232) rot=(0,0,1;0rad)
  Radius = 3
FEATURE [Part::Cylinder] Cylinder1842  label="Válec1842"
  Angle = 360
  AttacherType = Attacher::AttachEngine3D
  Height = 3
  Placement = pos=(0,94,232) rot=(0,0,1;0rad)
  Radius = 3
FEATURE [Part::Cylinder] Cylinder  label="Válec"
  Angle = 360
  AttacherType = Attacher::AttachEngine3D
  Height = 10
  Placement = pos=(0,83,232) rot=(0,0,1;0rad)
  Radius = 25
FEATURE [Part::Cylinder] Cylinder663  label="Válec663"
  Angle = 360
  AttacherType = Attacher::AttachEngine3D
  Height = 30
  Placement = pos=(0,94,232) rot=(0,0,1;0rad)
  Radius = 1.5
FEATURE [Part::Cylinder] Cylinder662  label="Válec662"
  Angle = 360
  AttacherType = Attacher::AttachEngine3D
  Height = 30
  Placement = pos=(0,72,232) rot=(0,0,1;0rad)
  Radius = 1.5
FEATURE [Part::Compound] Compound921
  Links = -> [Cylinder659,Cylinder660,Cylinder662,Cylinder663]
FEATURE [Part::Cylinder] Cylinder1843  label="Válec1843"
  Angle = 360
  AttacherType = Attacher::AttachEngine3D
  Height = 3
  Placement = pos=(-11,83,232) rot=(0,0,1;0rad)
  Radius = 3
FEATURE [Part::Compound] Compound923
  Links = -> [Cylinder1843,Cylinder664,Cylinder661,Cylinder1842]
  Placement = pos=(0,0,17) rot=(0,0,1;0rad)
FEATURE [Part::Cylinder] Cylinder1844  label="Válec1844"
  Angle = 360
  AttacherType = Attacher::AttachEngine3D
  Height = 10
  Placement = pos=(0,83,242) rot=(0,0,1;0rad)
  Radius = 15.1
FEATURE [Part::Cylinder] Cylinder1845  label="Válec1845"
  Angle = 360
  AttacherType = Attacher::AttachEngine3D
  Height = 30
  Placement = pos=(-11,83,232) rot=(0,0,1;0rad)
  Radius = 1.5
FEATURE [Part::Compound] Compound922
  Links = -> [Cylinder1845,Cylinder1839,Cylinder658,Cylinder1840]
FEATURE [Part::Cut] Cut565
  Base = -> wormgear029
  Tool = -> Compound367
FEATURE [Part::Cut] Cut232
  Base = -> Cut565
  Tool = -> Cylinder597
FEATURE [Part::Cut] Cut233
  Base = -> Cut232
  Tool = -> Compound364
FEATURE [Part::Cut] Cut566
  Base = -> Cylinder1838
  Tool = -> Cylinder1841
FEATURE [Part::Cut] Cut568
  Base = -> wormgear028
  Tool = -> Compound365
FEATURE [Part::Cut] Cut231
  Base = -> Cut568
  Tool = -> Cylinder1832
FEATURE [Part::Compound] Compound368  label="bazovina-prevod-B001"
  Links = -> [Cut231,Cut233]
  Placement = pos=(0,0,200) rot=(0,0,1;0rad)
FEATURE [Part::Cut] Cut569
  Base = -> Cylinder1844
  Tool = -> Compound922
FEATURE [Part::Cut] Cut567
  Base = -> Cut569
  Tool = -> Compound923
FEATURE [Part::Cut] Cut563
  Base = -> Cut567
  Tool = -> Cylinder1837
FEATURE [Part::Cut] Cut570
  Base = -> Common002
  Tool = -> Compound921
FEATURE [Part::Cut] Cut564
  Base = -> Cut570
  Tool = -> Cylinder
FEATURE [Part::Compound] Compound369
  Links = -> [Cut564,Cut563,Cut566]
FEATURE [Part::Compound] Compound366  label="Base_rear-gear-large"
  Links = -> [Compound369,Compound368]
  Placement = pos=(0,0,-202) rot=(0,0,1;0rad)
FEATURE [Part::Box] Box766  label="Krychle766"
  AttacherType = Attacher::AttachEngine3D
  Height = 6
  Length = 8
  Placement = pos=(-19,116,46) rot=(0,0,1;0rad)
  Width = 2
FEATURE [Part::Cylinder] Cylinder1846  label="Válec1846"
  Angle = 360
  AttacherType = Attacher::AttachEngine3D
  Height = 20
  Placement = pos=(0,124,51) rot=(1,0,0;1.5708rad)
  Radius = 12
FEATURE [Part::Cylinder] Cylinder1847  label="Válec1847"
  Angle = 360
  AttacherType = Attacher::AttachEngine3D
  Height = 40
  Placement = pos=(0,140,65) rot=(1,0,0;1.5708rad)
  Radius = 1.5
FEATURE [Part::Cylinder] Cylinder1848  label="Válec1848"
  Angle = 360
  AttacherType = Attacher::AttachEngine3D
  Height = 40
  Placement = pos=(16,140,49) rot=(1,0,0;1.5708rad)
  Radius = 1.5
FEATURE [Part::Box] Box767  label="Krychle767"
  AttacherType = Attacher::AttachEngine3D
  Height = 49
  Length = 56
  Placement = pos=(-28,114,29) rot=(0,0,1;0rad)
  Width = 8
FEATURE [Part::Box] Box768  label="Krychle768"
  AttacherType = Attacher::AttachEngine3D
  Height = 6
  Length = 8
  Placement = pos=(11,116,46) rot=(0,0,1;0rad)
  Width = 2
FEATURE [Part::Cylinder] Cylinder1849  label="Válec1849"
  Angle = 360
  AttacherType = Attacher::AttachEngine3D
  Height = 40
  Placement = pos=(0,140,33) rot=(1,0,0;1.5708rad)
  Radius = 1.5
FEATURE [Part::Cylinder] Cylinder1850  label="Válec1850"
  Angle = 360
  AttacherType = Attacher::AttachEngine3D
  Height = 40
  Placement = pos=(-16,140,49) rot=(1,0,0;1.5708rad)
  Radius = 1.5
FEATURE [Part::Compound] Compound925
  Links = -> [Cylinder1847,Cylinder1848,Cylinder1850,Cylinder1849]
  Placement = pos=(-34.65,0,16.35) rot=(0,1,0;0.785398rad)
FEATURE [Part::Cut] Cut571
  Base = -> Box767
  Tool = -> Compound925
FEATURE [Part::Cut] Cut573
  Base = -> Cut571
  Tool = -> Cylinder1846
FEATURE [Part::Box] Box769  label="Krychle769"
  AttacherType = Attacher::AttachEngine3D
  Height = 8
  Length = 6
  Placement = pos=(-3,116,60) rot=(0,0,1;0rad)
  Width = 2
FEATURE [Part::Box] Box770  label="Krychle770"
  AttacherType = Attacher::AttachEngine3D
  Height = 8
  Length = 6
  Placement = pos=(-3,116,30) rot=(0,0,1;0rad)
  Width = 2
FEATURE [Part::Compound] Compound924
  Links = -> [Box769,Box770,Box766,Box768]
  Placement = pos=(-34.65,0,16.35) rot=(0,1,0;0.785398rad)
FEATURE [Part::Cut] Cut572
  Base = -> Cut573
  Placement = pos=(0,18,0) rot=(0,0,1;0rad)
  Tool = -> Compound924
FEATURE [Part::Cylinder] Cylinder1851  label="Válec1851"
  Angle = 360
  AttacherType = Attacher::AttachEngine3D
  Height = 50
  Placement = pos=(-31,92,0) rot=(0,0,1;0.785398rad)
  Radius = 1.5
FEATURE [Part::Box] Box771  label="Krychle771"
  AttacherType = Attacher::AttachEngine3D
  Height = 2
  Length = 6
  Placement = pos=(-27,89,39) rot=(0,0,1;1.5708rad)
  Width = 8
FEATURE [Part::Compound] Compound926
  Links = -> [Box771]
FEATURE [Part::Compound] Compound927
  Links = -> [Cylinder1851]
FEATURE [Part::Box] Box772  label="Krychle772"
  AttacherType = Attacher::AttachEngine3D
  Height = 6
  Length = 49
  Placement = pos=(-34,83,78) rot=(0,1,0;1.5708rad)
  Width = 19
FEATURE [Part::Cut] Cut574
  Base = -> Box772
  Tool = -> Compound926
FEATURE [Part::Cut] Cut575
  Base = -> Cut574
  Placement = pos=(0,39,0) rot=(0,0,1;0rad)
  Tool = -> Compound927
FEATURE [Part::Box] Box773  label="Krychle773"
  AttacherType = Attacher::AttachEngine3D
  Height = 6
  Length = 49
  Placement = pos=(28,86,78) rot=(0,1,0;1.5708rad)
  Width = 19
FEATURE [Part::Box] Box774  label="Krychle774"
  AttacherType = Attacher::AttachEngine3D
  Height = 2
  Length = 6
  Placement = pos=(35,92,39) rot=(0,0,1;1.5708rad)
  Width = 8
FEATURE [Part::Compound] Compound928
  Links = -> [Box774]
FEATURE [Part::Cylinder] Cylinder1852  label="Válec1852"
  Angle = 360
  AttacherType = Attacher::AttachEngine3D
  Height = 50
  Placement = pos=(31,95,0) rot=(0,0,1;0.785398rad)
  Radius = 1.5
FEATURE [Part::Compound] Compound929
  Links = -> [Cylinder1852]
FEATURE [Part::Cut] Cut577
  Base = -> Box773
  Tool = -> Compound929
FEATURE [Part::Cut] Cut576
  Base = -> Cut577
  Placement = pos=(0,36,0) rot=(0,0,1;0rad)
  Tool = -> Compound928
FEATURE [Part::Cylinder] Cylinder1853  label="Válec1853"
  Angle = 360
  AttacherType = Attacher::AttachEngine3D
  Height = 50
  Placement = pos=(-31,150,48) rot=(1,0,0;1.5708rad)
  Radius = 1.5
FEATURE [Part::Cylinder] Cylinder1854  label="Válec1854"
  Angle = 360
  AttacherType = Attacher::AttachEngine3D
  Height = 50
  Placement = pos=(-31,150,72) rot=(1,0,0;1.5708rad)
  Radius = 1.5
FEATURE [Part::Cylinder] Cylinder1855  label="Válec1855"
  Angle = 360
  AttacherType = Attacher::AttachEngine3D
  Height = 50
  Placement = pos=(31,150,48) rot=(1,0,0;1.5708rad)
  Radius = 1.5
FEATURE [Part::Cylinder] Cylinder1856  label="Válec1856"
  Angle = 360
  AttacherType = Attacher::AttachEngine3D
  Height = 50
  Placement = pos=(31,150,72) rot=(1,0,0;1.5708rad)
  Radius = 1.5
FEATURE [Part::Compound] Compound930
  Links = -> [Cylinder1853,Cylinder1854,Cylinder1855,Cylinder1856]
FEATURE [Part::Cylinder] Cylinder1857  label="Válec1857"
  Angle = 360
  AttacherType = Attacher::AttachEngine3D
  Height = 50
  Placement = pos=(-31,150,48) rot=(1,0,0;1.5708rad)
  Radius = 1.5
FEATURE [Part::Cylinder] Cylinder1858  label="Válec1858"
  Angle = 360
  AttacherType = Attacher::AttachEngine3D
  Height = 50
  Placement = pos=(-31,150,72) rot=(1,0,0;1.5708rad)
  Radius = 1.5
FEATURE [Part::Cylinder] Cylinder1859  label="Válec1859"
  Angle = 360
  AttacherType = Attacher::AttachEngine3D
  Height = 50
  Placement = pos=(31,150,48) rot=(1,0,0;1.5708rad)
  Radius = 1.5
FEATURE [Part::Cylinder] Cylinder1860  label="Válec1860"
  Angle = 360
  AttacherType = Attacher::AttachEngine3D
  Height = 50
  Placement = pos=(31,150,72) rot=(1,0,0;1.5708rad)
  Radius = 1.5
FEATURE [Part::Compound] Compound931
  Links = -> [Cylinder1857,Cylinder1858,Cylinder1859,Cylinder1860]
FEATURE [Part::Cylinder] Cylinder1861  label="Válec1861"
  Angle = 360
  AttacherType = Attacher::AttachEngine3D
  Height = 3
  Placement = pos=(-31,150,72) rot=(1,0,0;1.5708rad)
  Radius = 3
FEATURE [Part::Cylinder] Cylinder1862  label="Válec1862"
  Angle = 360
  AttacherType = Attacher::AttachEngine3D
  Height = 3
  Placement = pos=(31,150,48) rot=(1,0,0;1.5708rad)
  Radius = 3
FEATURE [Part::Cylinder] Cylinder1863  label="Válec1863"
  Angle = 360
  AttacherType = Attacher::AttachEngine3D
  Height = 3
  Placement = pos=(-31,150,48) rot=(1,0,0;1.5708rad)
  Radius = 3
FEATURE [Part::Cylinder] Cylinder1864  label="Válec1864"
  Angle = 360
  AttacherType = Attacher::AttachEngine3D
  Height = 3
  Placement = pos=(31,150,72) rot=(1,0,0;1.5708rad)
  Radius = 3
FEATURE [Part::Compound] Compound932
  Links = -> [Cylinder1863,Cylinder1861,Cylinder1862,Cylinder1864]
  Placement = pos=(0,-9,0) rot=(0,0,1;0rad)
FEATURE [Part::Cylinder] Cylinder1865  label="Válec1865"
  Angle = 360
  AttacherType = Attacher::AttachEngine3D
  Height = 3
  Placement = pos=(31,150,48) rot=(1,0,0;1.5708rad)
  Radius = 3
FEATURE [Part::Cylinder] Cylinder1866  label="Válec1866"
  Angle = 360
  AttacherType = Attacher::AttachEngine3D
  Height = 3
  Placement = pos=(-31,150,72) rot=(1,0,0;1.5708rad)
  Radius = 3
FEATURE [Part::Cylinder] Cylinder1867  label="Válec1867"
  Angle = 360
  AttacherType = Attacher::AttachEngine3D
  Height = 3
  Placement = pos=(31,150,72) rot=(1,0,0;1.5708rad)
  Radius = 3
FEATURE [Part::Cylinder] Cylinder1868  label="Válec1868"
  Angle = 360
  AttacherType = Attacher::AttachEngine3D
  Height = 3
  Placement = pos=(-31,150,48) rot=(1,0,0;1.5708rad)
  Radius = 3
FEATURE [Part::Compound] Compound933
  Links = -> [Cylinder1868,Cylinder1866,Cylinder1865,Cylinder1867]
  Placement = pos=(0,-9,0) rot=(0,0,1;0rad)
FEATURE [Part::Cut] Cut578
  Base = -> Cut575
  Tool = -> Compound930
FEATURE [Part::Cut] Cut579
  Base = -> Cut578
  Tool = -> Compound933
FEATURE [Part::Cut] Cut580
  Base = -> Cut576
  Tool = -> Compound931
FEATURE [Part::Cut] Cut581
  Base = -> Cut580
  Tool = -> Compound932
FEATURE [Part::Cylinder] Cylinder1869  label="Válec1869"
  Angle = 360
  AttacherType = Attacher::AttachEngine3D
  Height = 50
  Placement = pos=(20,118,0) rot=(0,0,1;0.785398rad)
  Radius = 1.5
FEATURE [Part::Box] Box775  label="Krychle775"
  AttacherType = Attacher::AttachEngine3D
  Height = 2
  Length = 8
  Placement = pos=(-17,114,39) rot=(0,0,1;1.5708rad)
  Width = 6
FEATURE [Part::Box] Box776  label="Krychle776"
  AttacherType = Attacher::AttachEngine3D
  Height = 2
  Length = 8
  Placement = pos=(23,114,39) rot=(0,0,1;1.5708rad)
  Width = 6
FEATURE [Part::Compound] Compound934
  Links = -> [Box776,Box775]
  Placement = pos=(0,18,0) rot=(0,0,1;0rad)
FEATURE [Part::Cylinder] Cylinder1870  label="Válec1870"
  Angle = 360
  AttacherType = Attacher::AttachEngine3D
  Height = 50
  Placement = pos=(-20,118,0) rot=(0,0,1;0.785398rad)
  Radius = 1.5
FEATURE [Part::Compound] Compound935
  Links = -> [Cylinder1870,Cylinder1869]
  Placement = pos=(0,18,0) rot=(0,0,1;0rad)
FEATURE [Part::Cut] Cut582
  Base = -> Cut572
  Tool = -> Compound935
FEATURE [Part::Cut] Cut583
  Base = -> Cut582
  Placement = pos=(0,1,0) rot=(0,0,1;0rad)
  Tool = -> Compound934
FEATURE [Part::Box] Box777  label="Krychle777"
  AttacherType = Attacher::AttachEngine3D
  Height = 6
  Length = 68
  Placement = pos=(-34,122,78) rot=(0,0,1;0rad)
  Width = 19
FEATURE [Part::FeaturePython] Tube041  label="6003-2RS001"  # WARN: FeaturePython — macro-defined, semantics opaque (R4)
  AttacherType = Attacher::AttachEngine3D
  Height = 10
  InnerRadius = 17.5
  OuterRadius = 22
  Placement = pos=(0,132,51) rot=(1,0,0;1.5708rad)
FEATURE [Part::FeaturePython] Tube042  label="6003-2RS002"  # WARN: FeaturePython — macro-defined, semantics opaque (R4)
  AttacherType = Attacher::AttachEngine3D
  Height = 1
  InnerRadius = 16
  OuterRadius = 22
  Placement = pos=(0,133,51) rot=(1,0,0;1.5708rad)
FEATURE [Part::FeaturePython] Tube043  label="6003-2RS003"  # WARN: FeaturePython — macro-defined, semantics opaque (R4)
  AttacherType = Attacher::AttachEngine3D
  Height = 10
  InnerRadius = 17.5
  OuterRadius = 22
  Placement = pos=(0,132,51) rot=(1,0,0;1.5708rad)
FEATURE [Part::Chamfer] Chamfer063
  Base = -> Tube043
  Edges = 1 edges r=1: [Edge4]
FEATURE [Part::Compound] Compound936
  Links = -> [Chamfer063,Tube042]
FEATURE [Part::FeaturePython] Tube044  label="6003-2RS004"  # WARN: FeaturePython — macro-defined, semantics opaque (R4)
  AttacherType = Attacher::AttachEngine3D
  Height = 10
  InnerRadius = 8.5
  OuterRadius = 16
  Placement = pos=(0,131,51) rot=(1,0,0;1.5708rad)
FEATURE [Part::Cylinder] Cylinder1871  label="Válec1871"
  Angle = 360
  AttacherType = Attacher::AttachEngine3D
  Height = 50
  Placement = pos=(-31,101,0) rot=(0,0,1;0.785398rad)
  Radius = 1.5
FEATURE [Part::Box] Box778  label="Krychle778"
  AttacherType = Attacher::AttachEngine3D
  Height = 6
  Length = 49
  Placement = pos=(28,86,78) rot=(0,1,0;1.5708rad)
  Width = 36
FEATURE [Part::Box] Box779  label="Krychle779"
  AttacherType = Attacher::AttachEngine3D
  Height = 2
  Length = 6
  Placement = pos=(35,98,39) rot=(0,0,1;1.5708rad)
  Width = 8
FEATURE [Part::Box] Box780  label="Krychle780"
  AttacherType = Attacher::AttachEngine3D
  Height = 6
  Length = 8
  Placement = pos=(-19,116,46) rot=(0,0,1;0rad)
  Width = 2
FEATURE [Part::Box] Box781  label="Krychle781"
  AttacherType = Attacher::AttachEngine3D
  Height = 2
  Length = 6
  Placement = pos=(-27,98,39) rot=(0,0,1;1.5708rad)
  Width = 8
FEATURE [Part::Compound] Compound938
  Links = -> [Box781]
FEATURE [Part::Compound] Compound940
  Links = -> [Box779]
FEATURE [Part::Compound] Compound941
  Links = -> [Cylinder1871]
FEATURE [Part::Cylinder] Cylinder1872  label="Válec1872"
  Angle = 360
  AttacherType = Attacher::AttachEngine3D
  Height = 20
  Placement = pos=(0,124,51) rot=(1,0,0;1.5708rad)
  Radius = 12
FEATURE [Part::Cylinder] Cylinder1873  label="Válec1873"
  Angle = 360
  AttacherType = Attacher::AttachEngine3D
  Height = 40
  Placement = pos=(0,140,65) rot=(1,0,0;1.5708rad)
  Radius = 1.5
FEATURE [Part::Cylinder] Cylinder1874  label="Válec1874"
  Angle = 360
  AttacherType = Attacher::AttachEngine3D
  Height = 40
  Placement = pos=(16,140,49) rot=(1,0,0;1.5708rad)
  Radius = 1.5
FEATURE [Part::Box] Box782  label="Krychle782"
  AttacherType = Attacher::AttachEngine3D
  Height = 49
  Length = 56
  Placement = pos=(-28,114,29) rot=(0,0,1;0rad)
  Width = 8
FEATURE [Part::Box] Box783  label="Krychle783"
  AttacherType = Attacher::AttachEngine3D
  Height = 6
  Length = 8
  Placement = pos=(11,116,46) rot=(0,0,1;0rad)
  Width = 2
FEATURE [Part::Cylinder] Cylinder1875  label="Válec1875"
  Angle = 360
  AttacherType = Attacher::AttachEngine3D
  Height = 40
  Placement = pos=(0,140,33) rot=(1,0,0;1.5708rad)
  Radius = 1.5
FEATURE [Part::Box] Box784  label="Krychle784"
  AttacherType = Attacher::AttachEngine3D
  Height = 6
  Length = 49
  Placement = pos=(-34,86,78) rot=(0,1,0;1.5708rad)
  Width = 36
FEATURE [Part::Cut] Cut586
  Base = -> Box784
  Tool = -> Compound938
FEATURE [Part::Cut] Cut589
  Base = -> Cut586
  Tool = -> Compound941
FEATURE [Part::Cylinder] Cylinder1876  label="Válec1876"
  Angle = 360
  AttacherType = Attacher::AttachEngine3D
  Height = 40
  Placement = pos=(-16,140,49) rot=(1,0,0;1.5708rad)
  Radius = 1.5
FEATURE [Part::Compound] Compound942
  Links = -> [Cylinder1873,Cylinder1874,Cylinder1876,Cylinder1875]
  Placement = pos=(-34.65,0,16.35) rot=(0,1,0;0.785398rad)
FEATURE [Part::Cut] Cut584
  Base = -> Box782
  Tool = -> Compound942
FEATURE [Part::Cut] Cut590
  Base = -> Cut584
  Tool = -> Cylinder1872
FEATURE [Part::Box] Box785  label="Krychle785"
  AttacherType = Attacher::AttachEngine3D
  Height = 8
  Length = 6
  Placement = pos=(-3,116,60) rot=(0,0,1;0rad)
  Width = 2
FEATURE [Part::Cylinder] Cylinder1877  label="Válec1877"
  Angle = 360
  AttacherType = Attacher::AttachEngine3D
  Height = 50
  Placement = pos=(31,101,0) rot=(0,0,1;0.785398rad)
  Radius = 1.5
FEATURE [Part::Compound] Compound943
  Links = -> [Cylinder1877]
FEATURE [Part::Cut] Cut587
  Base = -> Box778
  Tool = -> Compound943
FEATURE [Part::Cut] Cut585
  Base = -> Cut587
  Tool = -> Compound940
FEATURE [Part::Box] Box786  label="Krychle786"
  AttacherType = Attacher::AttachEngine3D
  Height = 8
  Length = 6
  Placement = pos=(-3,116,30) rot=(0,0,1;0rad)
  Width = 2
FEATURE [Part::Compound] Compound939
  Links = -> [Box785,Box786,Box780,Box783]
  Placement = pos=(-34.65,0,16.35) rot=(0,1,0;0.785398rad)
FEATURE [Part::Cut] Cut588
  Base = -> Cut590
  Tool = -> Compound939
FEATURE [Part::Cylinder] Cylinder1878  label="Válec1878"
  Angle = 360
  AttacherType = Attacher::AttachEngine3D
  Height = 20
  Placement = pos=(0,124,51) rot=(1,0,0;1.5708rad)
  Radius = 12
FEATURE [Part::Box] Box787  label="Krychle787"
  AttacherType = Attacher::AttachEngine3D
  Height = 49
  Length = 56
  Placement = pos=(-28,114,29) rot=(0,0,1;0rad)
  Width = 8
FEATURE [Part::Cut] Cut591
  Base = -> Box787
  Tool = -> Cylinder1878
FEATURE [Part::Box] Box788  label="Krychle788"
  AttacherType = Attacher::AttachEngine3D
  Height = 6
  Length = 2
  Placement = pos=(-28,110,69) rot=(0,0,1;1.5708rad)
  Width = 6
FEATURE [Part::Cylinder] Cylinder1879  label="Válec1879"
  Angle = 360
  AttacherType = Attacher::AttachEngine3D
  Height = 50
  Placement = pos=(-31,150,48) rot=(1,0,0;1.5708rad)
  Radius = 1.5
FEATURE [Part::Cylinder] Cylinder1880  label="Válec1880"
  Angle = 360
  AttacherType = Attacher::AttachEngine3D
  Height = 50
  Placement = pos=(-31,150,72) rot=(1,0,0;1.5708rad)
  Radius = 1.5
FEATURE [Part::Box] Box789  label="Krychle789"
  AttacherType = Attacher::AttachEngine3D
  Height = 6
  Length = 2
  Placement = pos=(-28,110,45) rot=(0,0,1;1.5708rad)
  Width = 6
FEATURE [Part::Box] Box790  label="Krychle790"
  AttacherType = Attacher::AttachEngine3D
  Height = 6
  Length = 2
  Placement = pos=(34,110,69) rot=(0,0,1;1.5708rad)
  Width = 6
FEATURE [Part::Cylinder] Cylinder1881  label="Válec1881"
  Angle = 360
  AttacherType = Attacher::AttachEngine3D
  Height = 50
  Placement = pos=(31,150,48) rot=(1,0,0;1.5708rad)
  Radius = 1.5
FEATURE [Part::Cylinder] Cylinder1882  label="Válec1882"
  Angle = 360
  AttacherType = Attacher::AttachEngine3D
  Height = 50
  Placement = pos=(31,150,72) rot=(1,0,0;1.5708rad)
  Radius = 1.5
FEATURE [Part::Box] Box791  label="Krychle791"
  AttacherType = Attacher::AttachEngine3D
  Height = 6
  Length = 2
  Placement = pos=(34,110,45) rot=(0,0,1;1.5708rad)
  Width = 6
FEATURE [Part::Compound] Compound944
  Links = -> [Box789,Box788,Box791,Box790]
FEATURE [Part::Compound] Compound945
  Links = -> [Cylinder1879,Cylinder1880,Cylinder1881,Cylinder1882]
FEATURE [Part::Cylinder] Cylinder1883  label="Válec1883"
  Angle = 360
  AttacherType = Attacher::AttachEngine3D
  Height = 50
  Placement = pos=(22,118,0) rot=(0,0,1;0.785398rad)
  Radius = 1.5
FEATURE [Part::Box] Box792  label="Krychle792"
  AttacherType = Attacher::AttachEngine3D
  Height = 2
  Length = 8
  Placement = pos=(-19,114,39) rot=(0,0,1;1.5708rad)
  Width = 6
FEATURE [Part::Box] Box793  label="Krychle793"
  AttacherType = Attacher::AttachEngine3D
  Height = 2
  Length = 8
  Placement = pos=(25,114,39) rot=(0,0,1;1.5708rad)
  Width = 6
FEATURE [Part::Compound] Compound946
  Links = -> [Box793,Box792]
FEATURE [Part::Cylinder] Cylinder1884  label="Válec1884"
  Angle = 360
  AttacherType = Attacher::AttachEngine3D
  Height = 50
  Placement = pos=(-22,118,0) rot=(0,0,1;0.785398rad)
  Radius = 1.5
FEATURE [Part::Compound] Compound947
  Links = -> [Cylinder1884,Cylinder1883]
FEATURE [Part::Cut] Cut592
  Base = -> Cut591
  Tool = -> Compound946
FEATURE [Part::Cut] Cut593
  Base = -> Cut592
  Tool = -> Compound947
FEATURE [Part::Box] Box794  label="Krychle794"
  AttacherType = Attacher::AttachEngine3D
  Height = 6
  Length = 2
  Placement = pos=(-28,110,69) rot=(0,0,1;1.5708rad)
  Width = 6
FEATURE [Part::Box] Box795  label="Krychle795"
  AttacherType = Attacher::AttachEngine3D
  Height = 6
  Length = 2
  Placement = pos=(34,110,69) rot=(0,0,1;1.5708rad)
  Width = 6
FEATURE [Part::Box] Box796  label="Krychle796"
  AttacherType = Attacher::AttachEngine3D
  Height = 6
  Length = 2
  Placement = pos=(-28,110,45) rot=(0,0,1;1.5708rad)
  Width = 6
FEATURE [Part::Box] Box797  label="Krychle797"
  AttacherType = Attacher::AttachEngine3D
  Height = 6
  Length = 2
  Placement = pos=(34,110,45) rot=(0,0,1;1.5708rad)
  Width = 6
FEATURE [Part::Compound] Compound948
  Links = -> [Box796,Box794,Box797,Box795]
FEATURE [Part::Cylinder] Cylinder1885  label="Válec1885"
  Angle = 360
  AttacherType = Attacher::AttachEngine3D
  Height = 50
  Placement = pos=(-31,150,48) rot=(1,0,0;1.5708rad)
  Radius = 1.5
FEATURE [Part::Cylinder] Cylinder1886  label="Válec1886"
  Angle = 360
  AttacherType = Attacher::AttachEngine3D
  Height = 50
  Placement = pos=(-31,150,72) rot=(1,0,0;1.5708rad)
  Radius = 1.5
FEATURE [Part::Cylinder] Cylinder1887  label="Válec1887"
  Angle = 360
  AttacherType = Attacher::AttachEngine3D
  Height = 50
  Placement = pos=(31,150,72) rot=(1,0,0;1.5708rad)
  Radius = 1.5
FEATURE [Part::Cylinder] Cylinder1888  label="Válec1888"
  Angle = 360
  AttacherType = Attacher::AttachEngine3D
  Height = 50
  Placement = pos=(31,150,48) rot=(1,0,0;1.5708rad)
  Radius = 1.5
FEATURE [Part::Compound] Compound949
  Links = -> [Cylinder1885,Cylinder1886,Cylinder1888,Cylinder1887]
FEATURE [Part::Cut] Cut594
  Base = -> Cut589
  Tool = -> Compound948
FEATURE [Part::Cut] Cut595
  Base = -> Cut594
  Tool = -> Compound949
FEATURE [Part::Cut] Cut596
  Base = -> Cut585
  Tool = -> Compound944
FEATURE [Part::Cut] Cut597
  Base = -> Cut596
  Tool = -> Compound945
FEATURE [Part::Cut] Cut598
  Base = -> Cut593
  Tool = -> Tube044
FEATURE [Part::Compound] Compound950  label="Base_rear-bearing-box"
  Links = -> [Cut583,Compound936,Box777,Cut581,Cut579]
FEATURE [Part::Cylinder] Cylinder1889  label="Válec1889"
  Angle = 360
  AttacherType = Attacher::AttachEngine3D
  Height = 50
  Placement = pos=(54,59,0) rot=(0,0,1;0.785398rad)
  Radius = 1.5
FEATURE [Part::Cylinder] Cylinder1890  label="Válec1890"
  Angle = 360
  AttacherType = Attacher::AttachEngine3D
  Height = 50
  Placement = pos=(-54,59,0) rot=(0,0,1;0.785398rad)
  Radius = 1.5
FEATURE [Part::Compound] Compound951
  Links = -> [Cylinder1889,Cylinder1890]
FEATURE [Part::Box] Box798  label="Krychle798"
  AttacherType = Attacher::AttachEngine3D
  Height = 2
  Length = 6
  Placement = pos=(-57,56,29) rot=(0,0,1;0rad)
  Width = 12
FEATURE [Part::Box] Box799  label="Krychle799"
  AttacherType = Attacher::AttachEngine3D
  Height = 2
  Length = 6
  Placement = pos=(51,56,29) rot=(0,0,1;0rad)
  Width = 12
FEATURE [Part::Compound] Compound952
  Links = -> [Box798,Box799]
  Placement = pos=(0,-1,10) rot=(0,0,1;0rad)
FEATURE [Part::Cut] Cut599
  Base = -> Cut539
  Tool = -> Compound952
FEATURE [Part::Cut] Cut600
  Base = -> Cut599
  Tool = -> Compound951
FEATURE [Part::Box] Box800  label="Krychle800"
  AttacherType = Attacher::AttachEngine3D
  Height = 6
  Length = 68
  Placement = pos=(-34,86,25) rot=(0,0,1;0rad)
  Width = 36
FEATURE [Part::Cylinder] Cylinder1891  label="Válec1891"
  Angle = 360
  AttacherType = Attacher::AttachEngine3D
  Height = 50
  Placement = pos=(-71,80,24) rot=(1,0,0;1.5708rad)
  Radius = 1.5
FEATURE [Part::Box] Box801  label="Krychle801"
  AttacherType = Attacher::AttachEngine3D
  Height = 15
  Length = 148
  Placement = pos=(-74,48,16) rot=(0,0,1;0rad)
  Width = 38
FEATURE [Part::Cylinder] Cylinder1892  label="Válec1892"
  Angle = 360
  AttacherType = Attacher::AttachEngine3D
  Height = 36
  Placement = pos=(76.3,104,16) rot=(0,0,1;0rad)
  Radius = 46
FEATURE [Part::Cylinder] Cylinder1894  label="Válec1894"
  Angle = 360
  AttacherType = Attacher::AttachEngine3D
  Height = 15
  Placement = pos=(0,0,16) rot=(0,0,1;0rad)
  Radius = 74
FEATURE [Part::Cylinder] Cylinder1895  label="Válec1895"
  Angle = 360
  AttacherType = Attacher::AttachEngine3D
  Height = 36
  Placement = pos=(-76.3,104,16) rot=(0,0,1;0rad)
  Radius = 46
FEATURE [Part::Cut] Cut601
  Base = -> Box801
  Tool = -> Cylinder1895
FEATURE [Part::Cut] Cut602
  Base = -> Cut601
  Tool = -> Cylinder1892
FEATURE [Part::Cut] Cut608
  Base = -> Cut602
  Tool = -> Cylinder1894
FEATURE [Part::Cylinder] Cylinder1896  label="Válec1896"
  Angle = 360
  AttacherType = Attacher::AttachEngine3D
  Height = 50
  Placement = pos=(-31,101,0) rot=(0,0,1;0.785398rad)
  Radius = 1.5
FEATURE [Part::Cylinder] Cylinder1897  label="Válec1897"
  Angle = 360
  AttacherType = Attacher::AttachEngine3D
  Height = 50
  Placement = pos=(-71,106,24) rot=(1,0,0;1.5708rad)
  Radius = 3
FEATURE [Part::Cylinder] Cylinder1898  label="Válec1898"
  Angle = 360
  AttacherType = Attacher::AttachEngine3D
  Height = 50
  Placement = pos=(71,106,24) rot=(1,0,0;1.5708rad)
  Radius = 3
FEATURE [Part::Compound] Compound955
  Links = -> [Cylinder1898,Cylinder1897]
FEATURE [Part::Cylinder] Cylinder1899  label="Válec1899"
  Angle = 360
  AttacherType = Attacher::AttachEngine3D
  Height = 50
  Placement = pos=(71,80,24) rot=(1,0,0;1.5708rad)
  Radius = 1.5
FEATURE [Part::Compound] Compound953
  Links = -> [Cylinder1899,Cylinder1891]
FEATURE [Part::Cut] Cut607
  Base = -> Cut608
  Tool = -> Compound953
FEATURE [Part::Cut] Cut605
  Base = -> Cut607
  Tool = -> Compound955
FEATURE [Part::Cylinder] Cylinder1900  label="Válec1900"
  Angle = 360
  AttacherType = Attacher::AttachEngine3D
  Height = 50
  Placement = pos=(31,101,0) rot=(0,0,1;0.785398rad)
  Radius = 1.5
FEATURE [Part::Compound] Compound954
  Links = -> [Cylinder1896,Cylinder1900]
FEATURE [Part::Cut] Cut606
  Base = -> Box800
  Tool = -> Compound954
FEATURE [Part::Cylinder] Cylinder1901  label="Válec1901"
  Angle = 360
  AttacherType = Attacher::AttachEngine3D
  Height = 6
  Placement = pos=(0,83,25) rot=(0,0,1;0rad)
  Radius = 8
FEATURE [Part::Cut] Cut603
  Base = -> Cut606
  Tool = -> Cylinder1901
FEATURE [Part::Cylinder] Cylinder1902  label="Válec1902"
  Angle = 360
  AttacherType = Attacher::AttachEngine3D
  Height = 6
  Placement = pos=(0,83,25) rot=(0,0,1;0rad)
  Radius = 8
FEATURE [Part::Cut] Cut604
  Base = -> Cut605
  Tool = -> Cylinder1902
FEATURE [Part::Cylinder] Cylinder1904  label="Válec1904"
  Angle = 360
  AttacherType = Attacher::AttachEngine3D
  Height = 3
  Placement = pos=(-22,118,0) rot=(0,0,1;0.785398rad)
  Radius = 3
FEATURE [Part::Cylinder] Cylinder1905  label="Válec1905"
  Angle = 360
  AttacherType = Attacher::AttachEngine3D
  Height = 3
  Placement = pos=(22,118,0) rot=(0,0,1;0.785398rad)
  Radius = 3
FEATURE [Part::Cylinder] Cylinder1906  label="Válec1906"
  Angle = 360
  AttacherType = Attacher::AttachEngine3D
  Height = 50
  Placement = pos=(22,118,0) rot=(0,0,1;0.785398rad)
  Radius = 1.5
FEATURE [Part::Cylinder] Cylinder1907  label="Válec1907"
  Angle = 360
  AttacherType = Attacher::AttachEngine3D
  Height = 3
  Placement = pos=(31,101,0) rot=(0,0,1;0.785398rad)
  Radius = 3
FEATURE [Part::Cylinder] Cylinder1908  label="Válec1908"
  Angle = 360
  AttacherType = Attacher::AttachEngine3D
  Height = 50
  Placement = pos=(-22,118,0) rot=(0,0,1;0.785398rad)
  Radius = 1.5
FEATURE [Part::Cylinder] Cylinder1909  label="Válec1909"
  Angle = 360
  AttacherType = Attacher::AttachEngine3D
  Height = 3
  Placement = pos=(-31,101,0) rot=(0,0,1;0.785398rad)
  Radius = 3
FEATURE [Part::Compound] Compound956
  Links = -> [Cylinder1904,Cylinder1905]
  Placement = pos=(0,0,25) rot=(0,0,1;0rad)
FEATURE [Part::Compound] Compound957
  Links = -> [Cylinder1909,Cylinder1907]
  Placement = pos=(0,0,25) rot=(0,0,1;0rad)
FEATURE [Part::Compound] Compound958
  Links = -> [Cylinder1908,Cylinder1906]
FEATURE [Part::Cut] Cut609
  Base = -> Cut603
  Tool = -> Compound958
FEATURE [Part::Chamfer] Chamfer064
  Base = -> Cut604
  Edges = 1 edges r=2: [Edge24]
FEATURE [Part::Cut] Cut611
  Base = -> Cut609
  Tool = -> Compound957
FEATURE [Part::Cut] Cut610
  Base = -> Cut611
  Tool = -> Compound956
FEATURE [Part::Cylinder] Cylinder1910  label="Válec1910"
  Angle = 360
  AttacherType = Attacher::AttachEngine3D
  Height = 50
  Placement = pos=(-54,59,0) rot=(0,0,1;0.785398rad)
  Radius = 1.5
FEATURE [Part::Cylinder] Cylinder1911  label="Válec1911"
  Angle = 360
  AttacherType = Attacher::AttachEngine3D
  Height = 50
  Placement = pos=(54,59,0) rot=(0,0,1;0.785398rad)
  Radius = 1.5
FEATURE [Part::Compound] Compound959
  Links = -> [Cylinder1911,Cylinder1910]
FEATURE [Part::Cylinder] Cylinder1912  label="Válec1912"
  Angle = 360
  AttacherType = Attacher::AttachEngine3D
  Height = 50
  Placement = pos=(31,77,0) rot=(0,0,1;0.785398rad)
  Radius = 1.5
FEATURE [Part::Cylinder] Cylinder1913  label="Válec1913"
  Angle = 360
  AttacherType = Attacher::AttachEngine3D
  Height = 50
  Placement = pos=(-31,77,0) rot=(0,0,1;0.785398rad)
  Radius = 1.5
FEATURE [Part::Compound] Compound960
  Links = -> [Cylinder1912,Cylinder1913]
FEATURE [Part::Cylinder] Cylinder1914  label="Válec1914"
  Angle = 360
  AttacherType = Attacher::AttachEngine3D
  Height = 50
  Placement = pos=(20,137,0) rot=(0,0,1;0.785398rad)
  Radius = 1.5
FEATURE [Part::Cylinder] Cylinder1915  label="Válec1915"
  Angle = 360
  AttacherType = Attacher::AttachEngine3D
  Height = 50
  Placement = pos=(-20,137,0) rot=(0,0,1;0.785398rad)
  Radius = 1.5
FEATURE [Part::Compound] Compound961
  Links = -> [Cylinder1915,Cylinder1914]
FEATURE [Part::Cylinder] Cylinder1916  label="Válec1916"
  Angle = 360
  AttacherType = Attacher::AttachEngine3D
  Height = 3
  Placement = pos=(20,137,0) rot=(0,0,1;0.785398rad)
  Radius = 3
FEATURE [Part::Cylinder] Cylinder1917  label="Válec1917"
  Angle = 360
  AttacherType = Attacher::AttachEngine3D
  Height = 3
  Placement = pos=(-20,137,0) rot=(0,0,1;0.785398rad)
  Radius = 3
FEATURE [Part::Compound] Compound962
  Links = -> [Cylinder1917,Cylinder1916]
  Placement = pos=(0,0,25) rot=(0,0,1;0rad)
FEATURE [Part::Cylinder] Cylinder1918  label="Válec1918"
  Angle = 360
  AttacherType = Attacher::AttachEngine3D
  Height = 3
  Placement = pos=(31,131,0) rot=(0,0,1;0.785398rad)
  Radius = 3
FEATURE [Part::Cylinder] Cylinder1919  label="Válec1919"
  Angle = 360
  AttacherType = Attacher::AttachEngine3D
  Height = 3
  Placement = pos=(-31,131,0) rot=(0,0,1;0.785398rad)
  Radius = 3
FEATURE [Part::Compound] Compound963
  Links = -> [Cylinder1919,Cylinder1918]
  Placement = pos=(0,0,25) rot=(0,0,1;0rad)
FEATURE [Part::Cylinder] Cylinder1920  label="Válec1920"
  Angle = 360
  AttacherType = Attacher::AttachEngine3D
  Height = 50
  Placement = pos=(-31,131,0) rot=(0,0,1;0.785398rad)
  Radius = 1.5
FEATURE [Part::Cylinder] Cylinder1921  label="Válec1921"
  Angle = 360
  AttacherType = Attacher::AttachEngine3D
  Height = 50
  Placement = pos=(31,131,0) rot=(0,0,1;0.785398rad)
  Radius = 1.5
FEATURE [Part::Compound] Compound964
  Links = -> [Cylinder1920,Cylinder1921]
FEATURE [Part::Cylinder] Cylinder1922  label="Válec1922"
  Angle = 360
  AttacherType = Attacher::AttachEngine3D
  Height = 3
  Placement = pos=(31,77,0) rot=(0,0,1;0.785398rad)
  Radius = 3
FEATURE [Part::Cylinder] Cylinder1923  label="Válec1923"
  Angle = 360
  AttacherType = Attacher::AttachEngine3D
  Height = 3
  Placement = pos=(-31,77,0) rot=(0,0,1;0.785398rad)
  Radius = 3
FEATURE [Part::Compound] Compound966
  Links = -> [Cylinder1922,Cylinder1923]
FEATURE [Part::Cylinder] Cylinder1924  label="Válec1924"
  Angle = 360
  AttacherType = Attacher::AttachEngine3D
  Height = 3
  Placement = pos=(54,59,0) rot=(0,0,1;0.785398rad)
  Radius = 3
FEATURE [Part::Cylinder] Cylinder1925  label="Válec1925"
  Angle = 360
  AttacherType = Attacher::AttachEngine3D
  Height = 3
  Placement = pos=(-54,59,0) rot=(0,0,1;0.785398rad)
  Radius = 3
FEATURE [Part::Compound] Compound965
  Links = -> [Cylinder1924,Cylinder1925]
FEATURE [Part::Compound] Compound967
  Links = -> [Compound965,Compound966]
  Placement = pos=(0,0,16) rot=(0,0,1;0rad)
FEATURE [Part::Cut] Cut612
  Base = -> Chamfer064
  Tool = -> Compound967
FEATURE [Part::Compound] Compound968
  Links = -> [Compound959,Compound960]
FEATURE [Part::Cut] Cut613
  Base = -> Cut612
  Tool = -> Compound968
FEATURE [Part::Cylinder] Cylinder1926  label="Válec1926"
  Angle = 360
  AttacherType = Attacher::AttachEngine3D
  Height = 6
  Placement = pos=(0,83,25) rot=(0,0,1;0rad)
  Radius = 8
FEATURE [Part::Box] Box802  label="Krychle802"
  AttacherType = Attacher::AttachEngine3D
  Height = 6
  Length = 68
  Placement = pos=(-34,86,25) rot=(0,0,1;0rad)
  Width = 55
FEATURE [Part::Cut] Cut614
  Base = -> Box802
  Tool = -> Cylinder1926
FEATURE [Part::Cylinder] Cylinder1927  label="Válec1927"
  Angle = 360
  AttacherType = Attacher::AttachEngine3D
  Height = 3
  Placement = pos=(22,118,0) rot=(0,0,1;0.785398rad)
  Radius = 3
FEATURE [Part::Cylinder] Cylinder1928  label="Válec1928"
  Angle = 360
  AttacherType = Attacher::AttachEngine3D
  Height = 3
  Placement = pos=(31,101,0) rot=(0,0,1;0.785398rad)
  Radius = 3
FEATURE [Part::Cylinder] Cylinder1929  label="Válec1929"
  Angle = 360
  AttacherType = Attacher::AttachEngine3D
  Height = 50
  Placement = pos=(-31,101,0) rot=(0,0,1;0.785398rad)
  Radius = 1.5
FEATURE [Part::Cylinder] Cylinder1930  label="Válec1930"
  Angle = 360
  AttacherType = Attacher::AttachEngine3D
  Height = 50
  Placement = pos=(31,101,0) rot=(0,0,1;0.785398rad)
  Radius = 1.5
FEATURE [Part::Compound] Compound970
  Links = -> [Cylinder1929,Cylinder1930]
FEATURE [Part::Cylinder] Cylinder1931  label="Válec1931"
  Angle = 360
  AttacherType = Attacher::AttachEngine3D
  Height = 3
  Placement = pos=(-22,118,0) rot=(0,0,1;0.785398rad)
  Radius = 3
FEATURE [Part::Compound] Compound971
  Links = -> [Cylinder1931,Cylinder1927]
  Placement = pos=(0,0,25) rot=(0,0,1;0rad)
FEATURE [Part::Cylinder] Cylinder1932  label="Válec1932"
  Angle = 360
  AttacherType = Attacher::AttachEngine3D
  Height = 50
  Placement = pos=(22,118,0) rot=(0,0,1;0.785398rad)
  Radius = 1.5
FEATURE [Part::Cylinder] Cylinder1933  label="Válec1933"
  Angle = 360
  AttacherType = Attacher::AttachEngine3D
  Height = 50
  Placement = pos=(-22,118,0) rot=(0,0,1;0.785398rad)
  Radius = 1.5
FEATURE [Part::Compound] Compound972
  Links = -> [Cylinder1933,Cylinder1932]
FEATURE [Part::Cylinder] Cylinder1934  label="Válec1934"
  Angle = 360
  AttacherType = Attacher::AttachEngine3D
  Height = 3
  Placement = pos=(-31,101,0) rot=(0,0,1;0.785398rad)
  Radius = 3
FEATURE [Part::Compound] Compound969
  Links = -> [Cylinder1934,Cylinder1928]
  Placement = pos=(0,0,21) rot=(0,0,1;0rad)
FEATURE [Part::Compound] Compound973
  Links = -> [Compound962,Compound963,Compound969]
FEATURE [Part::Cylinder] Cylinder1935  label="Válec1935"
  Angle = 360
  AttacherType = Attacher::AttachEngine3D
  Height = 6
  Placement = pos=(0,101,21) rot=(0,0,1;0rad)
  Radius = 34
FEATURE [Part::Box] Box803  label="Krychle803"
  AttacherType = Attacher::AttachEngine3D
  Height = 40
  Length = 148
  Placement = pos=(-74,46,16) rot=(0,0,1;0rad)
  Width = 40
FEATURE [Part::Cut] Cut615
  Base = -> Cylinder1935
  Tool = -> Box803
FEATURE [Part::Cylinder] Cylinder1936  label="Válec1936"
  Angle = 360
  AttacherType = Attacher::AttachEngine3D
  Height = 6
  Placement = pos=(0,83,25) rot=(0,0,1;0rad)
  Radius = 8
FEATURE [Part::Cut] Cut616
  Base = -> Cut615
  Tool = -> Cylinder1936
FEATURE [Part::Box] Box804  label="Krychle804"
  AttacherType = Attacher::AttachEngine3D
  Height = 6
  Length = 68
  Placement = pos=(-34,86,21) rot=(0,0,1;0rad)
  Width = 15
FEATURE [Part::Cylinder] Cylinder1937  label="Válec1937"
  Angle = 360
  AttacherType = Attacher::AttachEngine3D
  Height = 6
  Placement = pos=(0,83,25) rot=(0,0,1;0rad)
  Radius = 8
FEATURE [Part::Cut] Cut617
  Base = -> Box804
  Tool = -> Cylinder1937
FEATURE [Part::Cylinder] Cylinder1938  label="Válec1938"
  Angle = 360
  AttacherType = Attacher::AttachEngine3D
  Height = 3
  Placement = pos=(31,131,0) rot=(0,0,1;0.785398rad)
  Radius = 3
FEATURE [Part::Cylinder] Cylinder1939  label="Válec1939"
  Angle = 360
  AttacherType = Attacher::AttachEngine3D
  Height = 3
  Placement = pos=(-31,131,0) rot=(0,0,1;0.785398rad)
  Radius = 3
FEATURE [Part::Compound] Compound975
  Links = -> [Cylinder1939,Cylinder1938]
  Placement = pos=(0,0,25) rot=(0,0,1;0rad)
FEATURE [Part::Cylinder] Cylinder1940  label="Válec1940"
  Angle = 360
  AttacherType = Attacher::AttachEngine3D
  Height = 3
  Placement = pos=(20,137,0) rot=(0,0,1;0.785398rad)
  Radius = 3
FEATURE [Part::Cylinder] Cylinder1941  label="Válec1941"
  Angle = 360
  AttacherType = Attacher::AttachEngine3D
  Height = 3
  Placement = pos=(-20,137,0) rot=(0,0,1;0.785398rad)
  Radius = 3
FEATURE [Part::Compound] Compound974
  Links = -> [Cylinder1941,Cylinder1940]
  Placement = pos=(0,0,25) rot=(0,0,1;0rad)
FEATURE [Part::Cylinder] Cylinder1942  label="Válec1942"
  Angle = 360
  AttacherType = Attacher::AttachEngine3D
  Height = 3
  Placement = pos=(31,101,0) rot=(0,0,1;0.785398rad)
  Radius = 3
FEATURE [Part::Cylinder] Cylinder1943  label="Válec1943"
  Angle = 360
  AttacherType = Attacher::AttachEngine3D
  Height = 3
  Placement = pos=(-31,101,0) rot=(0,0,1;0.785398rad)
  Radius = 3
FEATURE [Part::Compound] Compound976
  Links = -> [Cylinder1943,Cylinder1942]
  Placement = pos=(0,0,21) rot=(0,0,1;0rad)
FEATURE [Part::Compound] Compound977
  Links = -> [Compound974,Compound975,Compound976]
FEATURE [Part::Cut] Cut618
  Base = -> Cut617
  Tool = -> Compound977
FEATURE [Part::Cylinder] Cylinder1944  label="Válec1944"
  Angle = 360
  AttacherType = Attacher::AttachEngine3D
  Height = 3
  Placement = pos=(31,131,0) rot=(0,0,1;0.785398rad)
  Radius = 3
FEATURE [Part::Cylinder] Cylinder1945  label="Válec1945"
  Angle = 360
  AttacherType = Attacher::AttachEngine3D
  Height = 3
  Placement = pos=(-31,131,0) rot=(0,0,1;0.785398rad)
  Radius = 3
FEATURE [Part::Compound] Compound979
  Links = -> [Cylinder1945,Cylinder1944]
  Placement = pos=(0,0,25) rot=(0,0,1;0rad)
FEATURE [Part::Cylinder] Cylinder1946  label="Válec1946"
  Angle = 360
  AttacherType = Attacher::AttachEngine3D
  Height = 3
  Placement = pos=(20,137,0) rot=(0,0,1;0.785398rad)
  Radius = 3
FEATURE [Part::Cylinder] Cylinder1947  label="Válec1947"
  Angle = 360
  AttacherType = Attacher::AttachEngine3D
  Height = 3
  Placement = pos=(-20,137,0) rot=(0,0,1;0.785398rad)
  Radius = 3
FEATURE [Part::Compound] Compound978
  Links = -> [Cylinder1947,Cylinder1946]
  Placement = pos=(0,0,25) rot=(0,0,1;0rad)
FEATURE [Part::Cylinder] Cylinder1948  label="Válec1948"
  Angle = 360
  AttacherType = Attacher::AttachEngine3D
  Height = 3
  Placement = pos=(31,101,0) rot=(0,0,1;0.785398rad)
  Radius = 3
FEATURE [Part::Cylinder] Cylinder1949  label="Válec1949"
  Angle = 360
  AttacherType = Attacher::AttachEngine3D
  Height = 3
  Placement = pos=(-31,101,0) rot=(0,0,1;0.785398rad)
  Radius = 3
FEATURE [Part::Compound] Compound980
  Links = -> [Cylinder1949,Cylinder1948]
  Placement = pos=(0,0,21) rot=(0,0,1;0rad)
FEATURE [Part::Compound] Compound981
  Links = -> [Compound978,Compound979,Compound980]
FEATURE [Part::Chamfer] Chamfer065
  Base = -> Cut616
  Edges = 1 edges r=2: [Edge7]
FEATURE [Part::Chamfer] Chamfer066
  Base = -> Cut618
  Edges = 2 edges r=2: [Edge5,Edge25]
FEATURE [Part::Cylinder] Cylinder1950  label="Válec1950"
  Angle = 360
  AttacherType = Attacher::AttachEngine3D
  Height = 3
  Placement = pos=(20,137,0) rot=(0,0,1;0.785398rad)
  Radius = 3
FEATURE [Part::Cylinder] Cylinder1951  label="Válec1951"
  Angle = 360
  AttacherType = Attacher::AttachEngine3D
  Height = 3
  Placement = pos=(-20,137,0) rot=(0,0,1;0.785398rad)
  Radius = 3
FEATURE [Part::Compound] Compound983
  Links = -> [Cylinder1951,Cylinder1950]
  Placement = pos=(0,0,25) rot=(0,0,1;0rad)
FEATURE [Part::Cylinder] Cylinder1952  label="Válec1952"
  Angle = 360
  AttacherType = Attacher::AttachEngine3D
  Height = 3
  Placement = pos=(-31,101,0) rot=(0,0,1;0.785398rad)
  Radius = 3
FEATURE [Part::Cylinder] Cylinder1953  label="Válec1953"
  Angle = 360
  AttacherType = Attacher::AttachEngine3D
  Height = 3
  Placement = pos=(-31,131,0) rot=(0,0,1;0.785398rad)
  Radius = 3
FEATURE [Part::Cylinder] Cylinder1954  label="Válec1954"
  Angle = 360
  AttacherType = Attacher::AttachEngine3D
  Height = 3
  Placement = pos=(31,131,0) rot=(0,0,1;0.785398rad)
  Radius = 3
FEATURE [Part::Compound] Compound982
  Links = -> [Cylinder1953,Cylinder1954]
  Placement = pos=(0,0,25) rot=(0,0,1;0rad)
FEATURE [Part::Cylinder] Cylinder1955  label="Válec1955"
  Angle = 360
  AttacherType = Attacher::AttachEngine3D
  Height = 3
  Placement = pos=(31,101,0) rot=(0,0,1;0.785398rad)
  Radius = 3
FEATURE [Part::Compound] Compound984
  Links = -> [Cylinder1952,Cylinder1955]
  Placement = pos=(0,0,21) rot=(0,0,1;0rad)
FEATURE [Part::Compound] Compound985
  Links = -> [Compound983,Compound982,Compound984]
FEATURE [Part::Cut] Cut619
  Base = -> Chamfer065
  Tool = -> Compound985
FEATURE [Part::Cylinder] Cylinder1956  label="Válec1956"
  Angle = 360
  AttacherType = Attacher::AttachEngine3D
  Height = 3
  Placement = pos=(31,131,0) rot=(0,0,1;0.785398rad)
  Radius = 3
FEATURE [Part::Cylinder] Cylinder1957  label="Válec1957"
  Angle = 360
  AttacherType = Attacher::AttachEngine3D
  Height = 3
  Placement = pos=(-31,131,0) rot=(0,0,1;0.785398rad)
  Radius = 3
FEATURE [Part::Compound] Compound987
  Links = -> [Cylinder1957,Cylinder1956]
  Placement = pos=(0,0,25) rot=(0,0,1;0rad)
FEATURE [Part::Cylinder] Cylinder1958  label="Válec1958"
  Angle = 360
  AttacherType = Attacher::AttachEngine3D
  Height = 3
  Placement = pos=(20,137,0) rot=(0,0,1;0.785398rad)
  Radius = 3
FEATURE [Part::Cylinder] Cylinder1959  label="Válec1959"
  Angle = 360
  AttacherType = Attacher::AttachEngine3D
  Height = 3
  Placement = pos=(-20,137,0) rot=(0,0,1;0.785398rad)
  Radius = 3
FEATURE [Part::Compound] Compound986
  Links = -> [Cylinder1959,Cylinder1958]
  Placement = pos=(0,0,25) rot=(0,0,1;0rad)
FEATURE [Part::Cylinder] Cylinder1960  label="Válec1960"
  Angle = 360
  AttacherType = Attacher::AttachEngine3D
  Height = 3
  Placement = pos=(31,101,0) rot=(0,0,1;0.785398rad)
  Radius = 3
FEATURE [Part::Cylinder] Cylinder1961  label="Válec1961"
  Angle = 360
  AttacherType = Attacher::AttachEngine3D
  Height = 3
  Placement = pos=(-31,101,0) rot=(0,0,1;0.785398rad)
  Radius = 3
FEATURE [Part::Compound] Compound988
  Links = -> [Cylinder1961,Cylinder1960]
  Placement = pos=(0,0,21) rot=(0,0,1;0rad)
FEATURE [Part::Compound] Compound989
  Links = -> [Compound986,Compound987,Compound988]
FEATURE [Part::Cut] Cut620
  Base = -> Cut614
  Tool = -> Compound989
FEATURE [Part::Compound] Compound990
  Links = -> [Compound970,Compound961,Compound964]
FEATURE [Part::Cylinder] Cylinder1962  label="Válec1962"
  Angle = 360
  AttacherType = Attacher::AttachEngine3D
  Height = 50
  Placement = pos=(-31,131,0) rot=(0,0,1;0.785398rad)
  Radius = 1.5
FEATURE [Part::Cylinder] Cylinder1963  label="Válec1963"
  Angle = 360
  AttacherType = Attacher::AttachEngine3D
  Height = 50
  Placement = pos=(31,131,0) rot=(0,0,1;0.785398rad)
  Radius = 1.5
FEATURE [Part::Compound] Compound992
  Links = -> [Cylinder1962,Cylinder1963]
FEATURE [Part::Cylinder] Cylinder1964  label="Válec1964"
  Angle = 360
  AttacherType = Attacher::AttachEngine3D
  Height = 50
  Placement = pos=(20,137,0) rot=(0,0,1;0.785398rad)
  Radius = 1.5
FEATURE [Part::Cylinder] Cylinder1965  label="Válec1965"
  Angle = 360
  AttacherType = Attacher::AttachEngine3D
  Height = 50
  Placement = pos=(-20,137,0) rot=(0,0,1;0.785398rad)
  Radius = 1.5
FEATURE [Part::Compound] Compound991
  Links = -> [Cylinder1965,Cylinder1964]
FEATURE [Part::Cylinder] Cylinder1966  label="Válec1966"
  Angle = 360
  AttacherType = Attacher::AttachEngine3D
  Height = 50
  Placement = pos=(-31,101,0) rot=(0,0,1;0.785398rad)
  Radius = 1.5
FEATURE [Part::Cylinder] Cylinder1967  label="Válec1967"
  Angle = 360
  AttacherType = Attacher::AttachEngine3D
  Height = 50
  Placement = pos=(31,101,0) rot=(0,0,1;0.785398rad)
  Radius = 1.5
FEATURE [Part::Compound] Compound993
  Links = -> [Cylinder1966,Cylinder1967]
FEATURE [Part::Compound] Compound994
  Links = -> [Compound993,Compound991,Compound992]
FEATURE [Part::Cut] Cut621
  Base = -> Cut620
  Tool = -> Compound990
FEATURE [Part::Cylinder] Cylinder1968  label="Válec1968"
  Angle = 360
  AttacherType = Attacher::AttachEngine3D
  Height = 50
  Placement = pos=(-20,137,0) rot=(0,0,1;0.785398rad)
  Radius = 1.5
FEATURE [Part::Cylinder] Cylinder1969  label="Válec1969"
  Angle = 360
  AttacherType = Attacher::AttachEngine3D
  Height = 50
  Placement = pos=(-31,131,0) rot=(0,0,1;0.785398rad)
  Radius = 1.5
FEATURE [Part::Cylinder] Cylinder1970  label="Válec1970"
  Angle = 360
  AttacherType = Attacher::AttachEngine3D
  Height = 50
  Placement = pos=(31,131,0) rot=(0,0,1;0.785398rad)
  Radius = 1.5
FEATURE [Part::Compound] Compound998
  Links = -> [Cylinder1969,Cylinder1970]
FEATURE [Part::Cylinder] Cylinder1971  label="Válec1971"
  Angle = 360
  AttacherType = Attacher::AttachEngine3D
  Height = 50
  Placement = pos=(20,137,0) rot=(0,0,1;0.785398rad)
  Radius = 1.5
FEATURE [Part::Compound] Compound997
  Links = -> [Cylinder1968,Cylinder1971]
FEATURE [Part::Cylinder] Cylinder1972  label="Válec1972"
  Angle = 360
  AttacherType = Attacher::AttachEngine3D
  Height = 50
  Placement = pos=(-31,101,0) rot=(0,0,1;0.785398rad)
  Radius = 1.5
FEATURE [Part::Cylinder] Cylinder1973  label="Válec1973"
  Angle = 360
  AttacherType = Attacher::AttachEngine3D
  Height = 50
  Placement = pos=(31,101,0) rot=(0,0,1;0.785398rad)
  Radius = 1.5
FEATURE [Part::Compound] Compound995
  Links = -> [Cylinder1972,Cylinder1973]
FEATURE [Part::Compound] Compound996
  Links = -> [Compound995,Compound997,Compound998]
FEATURE [Part::Cut] Cut622
  Base = -> Cut619
  Tool = -> Compound994
FEATURE [Part::Cut] Cut623
  Base = -> Chamfer066
  Tool = -> Compound996
FEATURE [Part::Box] Box805  label="Krychle805"
  AttacherType = Attacher::AttachEngine3D
  Height = 40
  Length = 148
  Placement = pos=(-74,42,16) rot=(0,0,1;0rad)
  Width = 40
FEATURE [Part::Cylinder] Cylinder1974  label="Válec1974"
  Angle = 360
  AttacherType = Attacher::AttachEngine3D
  Height = 6
  Placement = pos=(0,86,16) rot=(0,0,1;0rad)
  Radius = 16
FEATURE [Part::Cut] Cut624
  Base = -> Cylinder1974
  Tool = -> Box805
FEATURE [Part::Chamfer] Chamfer067
  Base = -> Cut624
  Edges = 1 edges r=2: [Edge7]
FEATURE [Part::Compound] Compound999  label="Base_rear-gearbox-cover"
  Links = -> [Cut621,Cut622,Cut623,Chamfer067,Cut613]
  Placement = pos=(0,0,-2) rot=(0,0,1;0rad)
FEATURE [Part::Compound] Compound1000  label="Base_rear-gearbox"
  Links = -> [Cut600,Cut598,Cut597,Cut595,Compound910,mirror004,Box,Box751,Box730,Compound900]
FEATURE [Part::Box] Box322  label="Krychle322"
  AttacherType = Attacher::AttachEngine3D
  Height = 61
  Length = 32
  Placement = pos=(-16,28.25,-83) rot=(0,0,1;0rad)
  Width = 6
FEATURE [Part::Box] Box315  label="Krychle315"
  AttacherType = Attacher::AttachEngine3D
  Height = 20
  Length = 28.8
  Placement = pos=(-14.4,-8,34) rot=(0,0,1;0rad)
  Width = 43.38
FEATURE [Part::Box] Box316  label="Krychle316"
  AttacherType = Attacher::AttachEngine3D
  Height = 9
  Length = 64
  Placement = pos=(-32,-34,32) rot=(0,0,1;0rad)
  Width = 68
FEATURE [Part::Box] Box314  label="Krychle314"
  AttacherType = Attacher::AttachEngine3D
  Height = 40
  Length = 56.5
  Placement = pos=(-28.25,-28.25,32) rot=(0,0,1;0rad)
  Width = 56.5
FEATURE [Part::Cut] Cut304
  Base = -> Box316
  Tool = -> Box314
FEATURE [Part::Compound] Compound1003  label="hrubo_holder020"
  Links = -> [Cut304]
FEATURE [Part::Compound] Compound1002  label="hrubo_holder019"
  Links = -> [Compound1003]
FEATURE [Part::Cut] Cut305
  Base = -> Compound1002
  Placement = pos=(-29,18,30) rot=(0,0,1;0rad)
  Tool = -> Box315
FEATURE [Part::Compound] Compound1004
  Links = -> [Cut305]
  Placement = pos=(18,-29,32) rot=(0.707107,-0.707107,0;3.14159rad)
FEATURE [Part::Cylinder] Cylinder778  label="Válec778"
  Angle = 360
  AttacherType = Attacher::AttachEngine3D
  Height = 20
  Placement = pos=(0,0,-39) rot=(0,0,1;0rad)
  Radius = 12
FEATURE [Part::Box] Box320  label="Krychle320"
  AttacherType = Attacher::AttachEngine3D
  Height = 8
  Length = 68
  Placement = pos=(-34,-32,-30) rot=(0,0,1;0rad)
  Width = 64
FEATURE [Part::Box] Box318  label="Krychle318"
  AttacherType = Attacher::AttachEngine3D
  Height = 3
  Length = 20
  Placement = pos=(17.55,19.55,-28) rot=(0,0,1;0rad)
  Width = 8
FEATURE [Part::Box] Box317  label="Krychle317"
  AttacherType = Attacher::AttachEngine3D
  Height = 3
  Length = 20
  Placement = pos=(17.55,-27.55,-28) rot=(0,0,1;0rad)
  Width = 8
FEATURE [Part::Box] Box319  label="Krychle319"
  AttacherType = Attacher::AttachEngine3D
  Height = 3
  Length = 20
  Placement = pos=(-37.45,19.55,-28) rot=(0,0,1;0rad)
  Width = 8
FEATURE [Part::Box] Box321  label="Krychle321"
  AttacherType = Attacher::AttachEngine3D
  Height = 3
  Length = 20
  Placement = pos=(-37.45,-27.55,-28) rot=(0,0,1;0rad)
  Width = 8
FEATURE [Part::Compound] Compound1009
  Links = -> [Box318,Box317,Box319,Box321]
FEATURE [Part::Cut] Cut309
  Base = -> Box320
  Tool = -> Compound1009
FEATURE [Part::Cylinder] Cylinder773  label="Válec773"
  Angle = 360
  AttacherType = Attacher::AttachEngine3D
  Height = 20
  Placement = pos=(23.55,23.55,-34) rot=(0,0,1;0rad)
  Radius = 2.5
FEATURE [Part::Cylinder] Cylinder760  label="Válec760"
  Angle = 360
  AttacherType = Attacher::AttachEngine3D
  Height = 20
  Placement = pos=(-23.55,23.55,-34) rot=(0,0,1;0rad)
  Radius = 2.5
FEATURE [Part::Cylinder] Cylinder774  label="Válec774"
  Angle = 360
  AttacherType = Attacher::AttachEngine3D
  Height = 20
  Placement = pos=(-23.55,-23.55,-34) rot=(0,0,1;0rad)
  Radius = 2.5
FEATURE [Part::Cylinder] Cylinder759  label="Válec759"
  Angle = 360
  AttacherType = Attacher::AttachEngine3D
  Height = 20
  Placement = pos=(23.55,-23.55,-34) rot=(0,0,1;0rad)
  Radius = 2.5
FEATURE [Part::Compound] Compound1008
  Links = -> [Cylinder773,Cylinder760,Cylinder774,Cylinder759]
FEATURE [Part::Cut] Cut310
  Base = -> Cut309
  Tool = -> Compound1008
FEATURE [Part::Cut] Cut303
  Base = -> Cut310
  Tool = -> Cylinder778
FEATURE [Part::Cylinder] Cylinder1982  label="Válec1982"
  Angle = 360
  AttacherType = Attacher::AttachEngine3D
  Height = 40
  Placement = pos=(0,140,65) rot=(1,0,0;1.5708rad)
  Radius = 1.5
FEATURE [Part::Cylinder] Cylinder1983  label="Válec1983"
  Angle = 360
  AttacherType = Attacher::AttachEngine3D
  Height = 40
  Placement = pos=(16,140,49) rot=(1,0,0;1.5708rad)
  Radius = 1.5
FEATURE [Part::Cylinder] Cylinder1984  label="Válec1984"
  Angle = 360
  AttacherType = Attacher::AttachEngine3D
  Height = 40
  Placement = pos=(-16,140,49) rot=(1,0,0;1.5708rad)
  Radius = 1.5
FEATURE [Part::Cylinder] Cylinder1985  label="Válec1985"
  Angle = 360
  AttacherType = Attacher::AttachEngine3D
  Height = 40
  Placement = pos=(0,140,33) rot=(1,0,0;1.5708rad)
  Radius = 1.5
FEATURE [Part::Compound] Compound1001
  Links = -> [Cylinder1982,Cylinder1983,Cylinder1984,Cylinder1985]
  Placement = pos=(-34.65,34.65,-144) rot=(0.862856,0.357407,0.357407;1.71777rad)
FEATURE [Part::Cut] Cut625
  Base = -> Cut303
  Tool = -> Compound1001
FEATURE [Part::Cylinder] Cylinder1986  label="Válec1986"
  Angle = 360
  AttacherType = Attacher::AttachEngine3D
  Height = 3
  Placement = pos=(0,140,65) rot=(1,0,0;1.5708rad)
  Radius = 3
FEATURE [Part::Cylinder] Cylinder1988  label="Válec1988"
  Angle = 360
  AttacherType = Attacher::AttachEngine3D
  Height = 3
  Placement = pos=(16,140,49) rot=(1,0,0;1.5708rad)
  Radius = 3
FEATURE [Part::Cylinder] Cylinder1987  label="Válec1987"
  Angle = 360
  AttacherType = Attacher::AttachEngine3D
  Height = 3
  Placement = pos=(-16,140,49) rot=(1,0,0;1.5708rad)
  Radius = 3
FEATURE [Part::Cylinder] Cylinder1989  label="Válec1989"
  Angle = 360
  AttacherType = Attacher::AttachEngine3D
  Height = 3
  Placement = pos=(0,140,33) rot=(1,0,0;1.5708rad)
  Radius = 3
FEATURE [Part::Compound] Compound1010
  Links = -> [Cylinder1986,Cylinder1988,Cylinder1987,Cylinder1989]
  Placement = pos=(-34.65,34.65,-167) rot=(0.862856,0.357407,0.357407;1.71777rad)
FEATURE [Part::Cut] Cut311
  Base = -> Cut625
  Tool = -> Compound1010
FEATURE [Part::Cylinder] Cylinder1979  label="Válec1979"
  Angle = 360
  AttacherType = Attacher::AttachEngine3D
  Height = 1
  Placement = pos=(23.55,23.55,-34) rot=(0,0,1;0rad)
  Radius = 7
FEATURE [Part::Cylinder] Cylinder1980  label="Válec1980"
  Angle = 360
  AttacherType = Attacher::AttachEngine3D
  Height = 1
  Placement = pos=(-23.55,23.55,-34) rot=(0,0,1;0rad)
  Radius = 7
FEATURE [Part::Cylinder] Cylinder1978  label="Válec1978"
  Angle = 360
  AttacherType = Attacher::AttachEngine3D
  Height = 1
  Placement = pos=(-23.55,-23.55,-34) rot=(0,0,1;0rad)
  Radius = 7
FEATURE [Part::Cylinder] Cylinder1990  label="Válec1990"
  Angle = 360
  AttacherType = Attacher::AttachEngine3D
  Height = 1
  Placement = pos=(23.55,-23.55,-34) rot=(0,0,1;0rad)
  Radius = 7
FEATURE [Part::Compound] Compound1005
  Links = -> [Cylinder1979,Cylinder1980,Cylinder1978,Cylinder1990]
FEATURE [Part::Cylinder] Cylinder1977  label="Válec1977"
  Angle = 360
  AttacherType = Attacher::AttachEngine3D
  Height = 20
  Placement = pos=(23.55,23.55,-34) rot=(0,0,1;0rad)
  Radius = 2.5
FEATURE [Part::Cylinder] Cylinder1976  label="Válec1976"
  Angle = 360
  AttacherType = Attacher::AttachEngine3D
  Height = 20
  Placement = pos=(-23.55,23.55,-34) rot=(0,0,1;0rad)
  Radius = 2.5
FEATURE [Part::Cylinder] Cylinder1975  label="Válec1975"
  Angle = 360
  AttacherType = Attacher::AttachEngine3D
  Height = 20
  Placement = pos=(-23.55,-23.55,-34) rot=(0,0,1;0rad)
  Radius = 2.5
FEATURE [Part::Cylinder] Cylinder1981  label="Válec1981"
  Angle = 360
  AttacherType = Attacher::AttachEngine3D
  Height = 20
  Placement = pos=(23.55,-23.55,-34) rot=(0,0,1;0rad)
  Radius = 2.5
FEATURE [Part::Compound] Compound1007
  Links = -> [Cylinder1977,Cylinder1976,Cylinder1975,Cylinder1981]
  Placement = pos=(0,0,-8) rot=(0,0,1;0rad)
FEATURE [Part::Cut] Cut312
  Base = -> Compound1005
  Placement = pos=(0,0,3) rot=(0,0,1;0rad)
  Tool = -> Compound1007
FEATURE [Part::Compound] Compound1006
  Links = -> [Box322,Compound1004,Cut311,Cut312]
  Placement = pos=(0,119,51) rot=(1,0,0;1.5708rad)
FEATURE [Mesh::Feature] Mesh001  label="Base_rear-gearbox (Meshed)001"
FEATURE [Mesh::Feature] Mesh002  label="Base_rear-bearing-box (Meshed)"
FEATURE [Part::Cylinder] Cylinder1991  label="Válec1991"
  Angle = 360
  AttacherType = Attacher::AttachEngine3D
  Height = 3
  Placement = pos=(-43,105,25) rot=(0,0,1;0rad)
  Radius = 3
FEATURE [Part::Cylinder] Cylinder1992  label="Válec1992"
  Angle = 360
  AttacherType = Attacher::AttachEngine3D
  Height = 16
  Placement = pos=(-64,117,25) rot=(0,0,1;0rad)
  Radius = 1.5
FEATURE [Part::Cylinder] Cylinder1993  label="Válec1993"
  Angle = 360
  AttacherType = Attacher::AttachEngine3D
  Height = 3
  Placement = pos=(-43,117,25) rot=(0,0,1;0rad)
  Radius = 3
FEATURE [Part::Cylinder] Cylinder1994  label="Válec1994"
  Angle = 360
  AttacherType = Attacher::AttachEngine3D
  Height = 16
  Placement = pos=(-64,105,25) rot=(0,0,1;0rad)
  Radius = 1.5
FEATURE [Part::Cylinder] Cylinder1995  label="Válec1995"
  Angle = 360
  AttacherType = Attacher::AttachEngine3D
  Height = 16
  Placement = pos=(-43,117,25) rot=(0,0,1;0rad)
  Radius = 1.5
FEATURE [Part::Cylinder] Cylinder979  label="Válec979"
  Angle = 360
  AttacherType = Attacher::AttachEngine3D
  Height = 16
  Placement = pos=(-43,105,25) rot=(0,0,1;0rad)
  Radius = 1.5
FEATURE [Part::Box] Box806  label="Krychle806"
  AttacherType = Attacher::AttachEngine3D
  Height = 4
  Length = 35
  Placement = pos=(-67,98,27) rot=(0,0,1;0rad)
  Width = 24
FEATURE [Part::Cylinder] Cylinder1996  label="Válec1996"
  Angle = 360
  AttacherType = Attacher::AttachEngine3D
  Height = 3
  Placement = pos=(-64,105,25) rot=(0,0,1;0rad)
  Radius = 3
FEATURE [Part::Cylinder] Cylinder993  label="Válec993"
  Angle = 360
  AttacherType = Attacher::AttachEngine3D
  Height = 20
  Placement = pos=(-53,111,20) rot=(0,0,1;0rad)
  Radius = 2
FEATURE [Part::Cylinder] Cylinder1997  label="Válec1997"
  Angle = 360
  AttacherType = Attacher::AttachEngine3D
  Height = 3
  Placement = pos=(-64,117,25) rot=(0,0,1;0rad)
  Radius = 3
FEATURE [Part::Cylinder] Cylinder994  label="Válec994"
  Angle = 360
  AttacherType = Attacher::AttachEngine3D
  Height = 3
  Placement = pos=(-53,111,26) rot=(0,0,1;0rad)
  Radius = 4
FEATURE [Part::Compound] Compound1011
  Links = -> [Cylinder1995,Cylinder979,Cylinder1992,Cylinder1994]
FEATURE [Part::Compound] Compound1012
  Links = -> [Cylinder1993,Cylinder1991,Cylinder1997,Cylinder1996]
  Placement = pos=(0,0,1) rot=(0,0,1;0rad)
FEATURE [Part::Cut] Cut627
  Base = -> Box806
  Tool = -> Compound1012
FEATURE [Part::Cut] Cut626  label="stabilo_back_cavo_left1"
  Base = -> Cut627
  Tool = -> Compound1011
FEATURE [Part::Cut] Cut456
  Base = -> Cut626
  Tool = -> Cylinder993
FEATURE [Part::Cut] Cut457  label="Base_rear-gearbox_cover-left"
  Base = -> Cut456
  Placement = pos=(-2,0,4) rot=(0,0,1;0rad)
  Tool = -> Cylinder994
FEATURE [Part::Cylinder] Cylinder995  label="Válec995"
  Angle = 360
  AttacherType = Attacher::AttachEngine3D
  Height = 3
  Placement = pos=(-43,117,25) rot=(0,0,1;0rad)
  Radius = 3
FEATURE [Part::Cylinder] Cylinder999  label="Válec999"
  Angle = 360
  AttacherType = Attacher::AttachEngine3D
  Height = 16
  Placement = pos=(-43,105,25) rot=(0,0,1;0rad)
  Radius = 1.5
FEATURE [Part::Cylinder] Cylinder1001  label="Válec1001"
  Angle = 360
  AttacherType = Attacher::AttachEngine3D
  Height = 3
  Placement = pos=(-43,105,25) rot=(0,0,1;0rad)
  Radius = 3
FEATURE [Part::Cylinder] Cylinder996  label="Válec996"
  Angle = 360
  AttacherType = Attacher::AttachEngine3D
  Height = 3
  Placement = pos=(-64,105,25) rot=(0,0,1;0rad)
  Radius = 3
FEATURE [Part::Cylinder] Cylinder998  label="Válec998"
  Angle = 360
  AttacherType = Attacher::AttachEngine3D
  Height = 16
  Placement = pos=(-64,117,25) rot=(0,0,1;0rad)
  Radius = 1.5
FEATURE [Part::Cylinder] Cylinder1002  label="Válec1002"
  Angle = 360
  AttacherType = Attacher::AttachEngine3D
  Height = 3
  Placement = pos=(-64,117,25) rot=(0,0,1;0rad)
  Radius = 3
FEATURE [Part::Cylinder] Cylinder1004  label="Válec1004"
  Angle = 360
  AttacherType = Attacher::AttachEngine3D
  Height = 20
  Placement = pos=(-53,111,20) rot=(0,0,1;0rad)
  Radius = 2
FEATURE [Part::Box] Box807  label="Krychle807"
  AttacherType = Attacher::AttachEngine3D
  Height = 4
  Length = 35
  Placement = pos=(-67,98,27) rot=(0,0,1;0rad)
  Width = 24
FEATURE [Part::Cylinder] Cylinder1003  label="Válec1003"
  Angle = 360
  AttacherType = Attacher::AttachEngine3D
  Height = 3
  Placement = pos=(-53,111,26) rot=(0,0,1;0rad)
  Radius = 4
FEATURE [Part::Cylinder] Cylinder997  label="Válec997"
  Angle = 360
  AttacherType = Attacher::AttachEngine3D
  Height = 16
  Placement = pos=(-43,117,25) rot=(0,0,1;0rad)
  Radius = 1.5
FEATURE [Part::Cylinder] Cylinder1000  label="Válec1000"
  Angle = 360
  AttacherType = Attacher::AttachEngine3D
  Height = 16
  Placement = pos=(-64,105,25) rot=(0,0,1;0rad)
  Radius = 1.5
FEATURE [Part::Compound] Compound1013
  Links = -> [Cylinder997,Cylinder999,Cylinder998,Cylinder1000]
FEATURE [Part::Compound] Compound1014
  Links = -> [Cylinder995,Cylinder1001,Cylinder1002,Cylinder996]
  Placement = pos=(0,0,1) rot=(0,0,1;0rad)
FEATURE [Part::Cut] Cut459
  Base = -> Box807
  Tool = -> Compound1014
FEATURE [Part::Cut] Cut458  label="stabilo_back_cavo_left002"
  Base = -> Cut459
  Tool = -> Compound1013
FEATURE [Part::Cut] Cut460
  Base = -> Cut458
  Tool = -> Cylinder1004
FEATURE [Part::Cut] Cut461  label="stabilo_back_cavo_left003"
  Base = -> Cut460
  Tool = -> Cylinder1003
FEATURE [Part::Mirroring] mirror001  label="Base_rear_gearbox_cover-right"
  Base = (0,0,0)
  Normal = (1,0,0)
  Placement = pos=(2,0,4) rot=(0,0,1;0rad)
  Source = -> Cut461
FEATURE [Mesh::Feature] Mesh003  label="Base_rear-gearbox_cover-left (Meshed)"
FEATURE [Mesh::Feature] Mesh004  label="Base_rear_gearbox_cover-right (Meshed)"
